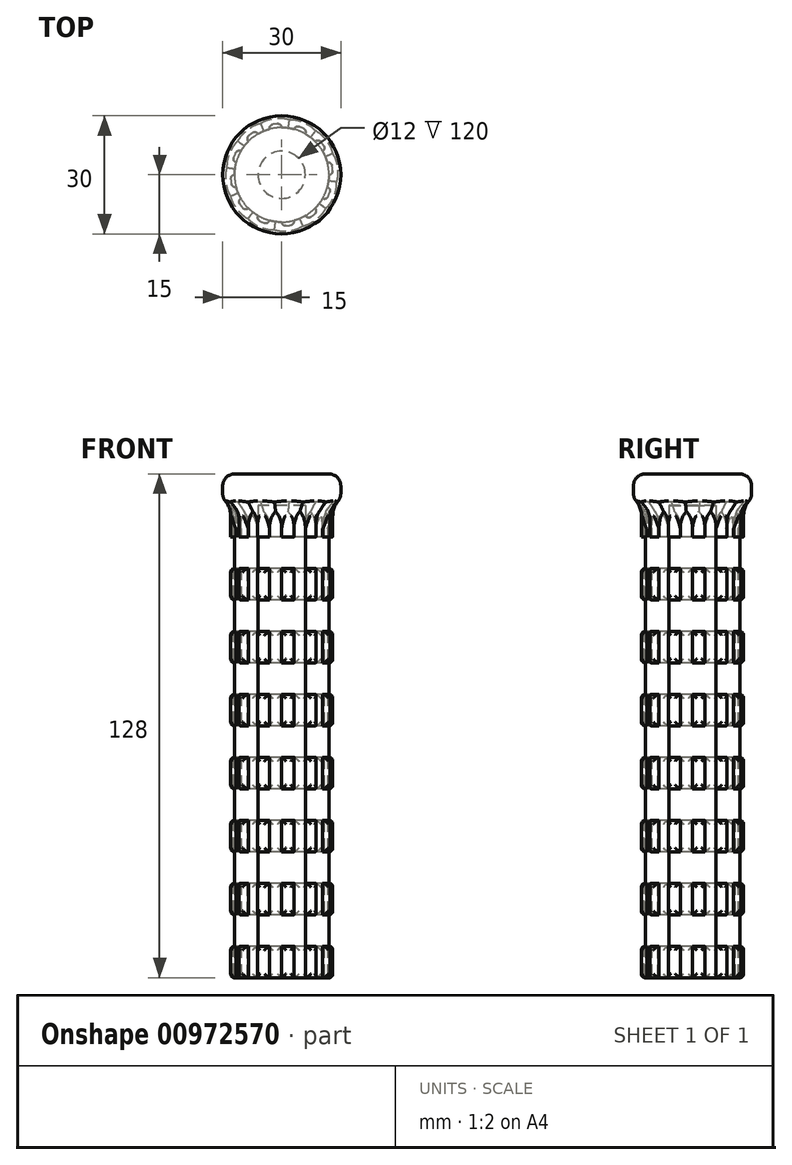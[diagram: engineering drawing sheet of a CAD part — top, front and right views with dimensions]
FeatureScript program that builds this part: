
annotation { "Feature Type Name" : "Feature", "Feature Type Description" : "" }
export const myFeature = defineFeature(function(context is Context, id is Id, definition is map)
    precondition{}
    {
        {
            var Q0;
            Q0=qCreatedBy(makeId("Top.planeOp"),FACE);
            var sketch = newSketch(context, id + "F0", { "sketchPlane" : qUnion([Q0])});
            skCircle(sketch, "E0", {"center": v(0, 0) * mm, "radius": 6 * mm});
            skCircle(sketch, "E1", {"center": v(0, 0) * mm, "radius": 12 * mm});
            skCircle(sketch, "E2", {"center": v(0, 0) * mm, "radius": 13 * mm});
            skLineSegment(sketch, "E3", {"start": v(0, 12) * mm, "end": v(0, 13) * mm});
            skLineSegment(sketch, "E4", {"start": v(-12, 0) * mm, "end": v(-13, 0) * mm, "construction": true});
            skLineSegment(sketch, "E5", {"start": v(-11.6, 3.1) * mm, "end": v(-12.56, 3.36) * mm});
            skLineSegment(sketch, "E6", {"start": v(-10.4, 6) * mm, "end": v(-11.26, 6.5) * mm});
            skLineSegment(sketch, "E7", {"start": v(-8.49, 8.49) * mm, "end": v(-9.2, 9.2) * mm});
            skLineSegment(sketch, "E8", {"start": v(-6, 10.4) * mm, "end": v(-6.5, 11.26) * mm});
            skLineSegment(sketch, "E9", {"start": v(-3.1, 11.6) * mm, "end": v(-3.36, 12.56) * mm});
            skLineSegment(sketch, "E10", {"start": v(-12, 0) * mm, "end": v(-13, 0) * mm});
            skLineSegment(sketch, "E11.MirrorCS", {"start": v(3.1, 11.6) * mm, "end": v(3.36, 12.56) * mm});
            skLineSegment(sketch, "E12.MirrorCS", {"start": v(6, 10.4) * mm, "end": v(6.5, 11.26) * mm});
            skLineSegment(sketch, "E13.MirrorCS", {"start": v(8.49, 8.49) * mm, "end": v(9.2, 9.2) * mm});
            skLineSegment(sketch, "E14.MirrorCS", {"start": v(10.4, 6) * mm, "end": v(11.26, 6.5) * mm});
            skLineSegment(sketch, "E15.MirrorCS", {"start": v(11.6, 3.1) * mm, "end": v(12.56, 3.36) * mm});
            skLineSegment(sketch, "E16.MirrorCS", {"start": v(12, 0) * mm, "end": v(13, 0) * mm, "construction": true});
            skLineSegment(sketch, "E17.MirrorCS", {"start": v(11.6, -3.1) * mm, "end": v(12.56, -3.36) * mm});
            skLineSegment(sketch, "E18.MirrorCS", {"start": v(10.4, -6) * mm, "end": v(11.26, -6.5) * mm});
            skLineSegment(sketch, "E19.MirrorCS", {"start": v(8.49, -8.49) * mm, "end": v(9.2, -9.2) * mm});
            skLineSegment(sketch, "E20.MirrorCS", {"start": v(6, -10.4) * mm, "end": v(6.5, -11.26) * mm});
            skLineSegment(sketch, "E21.MirrorCS", {"start": v(3.1, -11.6) * mm, "end": v(3.36, -12.56) * mm});
            skLineSegment(sketch, "E22.MirrorCS", {"start": v(0, -12) * mm, "end": v(0, -13) * mm});
            skLineSegment(sketch, "E23.MirrorCS", {"start": v(-3.1, -11.6) * mm, "end": v(-3.36, -12.56) * mm});
            skLineSegment(sketch, "E24.MirrorCS", {"start": v(-6, -10.4) * mm, "end": v(-6.5, -11.26) * mm});
            skLineSegment(sketch, "E25.MirrorCS", {"start": v(-8.49, -8.49) * mm, "end": v(-9.2, -9.2) * mm});
            skLineSegment(sketch, "E26.MirrorCS", {"start": v(-10.4, -6) * mm, "end": v(-11.26, -6.5) * mm});
            skLineSegment(sketch, "E27.MirrorCS", {"start": v(-11.6, -3.1) * mm, "end": v(-12.56, -3.36) * mm});
            skLineSegment(sketch, "E28", {"start": v(12, 0) * mm, "end": v(13, 0) * mm});
            skSolve(sketch);
        }
        {
            var Q0;
            Q0=makeQuery(id+"F0.imprint","IMPRINT",FACE,{"disambiguationData":[TD([[makeQuery(id+"F0.imprint","IMPRINT",EDGE,{"derivedFrom":sQuery(id+"F0.wireOp",EDGE,"E0")}),-1.0]])]});
            var Q1;
            {var subQ0=sQuery(id+"F0.wireOp",EDGE,"E3");Q1=makeQuery(id+"F0.imprint","IMPRINT",FACE,{"disambiguationData":[TD([[makeQuery(id+"F0.imprint","IMPRINT",EDGE,{"derivedFrom":subQ0}),1.0]])]});}
            var Q2;
            {var subQ0=sQuery(id+"F0.wireOp",EDGE,"E11.MirrorCS");Q2=makeQuery(id+"F0.imprint","IMPRINT",FACE,{"disambiguationData":[TD([[makeQuery(id+"F0.imprint","IMPRINT",EDGE,{"derivedFrom":subQ0}),-1.0]])]});}
            var Q3;
            {var subQ0=sQuery(id+"F0.wireOp",EDGE,"E13.MirrorCS");Q3=makeQuery(id+"F0.imprint","IMPRINT",FACE,{"disambiguationData":[TD([[makeQuery(id+"F0.imprint","IMPRINT",EDGE,{"derivedFrom":subQ0}),-1.0]])]});}
            var Q4;
            {var subQ0=sQuery(id+"F0.wireOp",EDGE,"E15.MirrorCS");Q4=makeQuery(id+"F0.imprint","IMPRINT",FACE,{"disambiguationData":[TD([[makeQuery(id+"F0.imprint","IMPRINT",EDGE,{"derivedFrom":subQ0}),-1.0]])]});}
            var Q5;
            {var subQ0=sQuery(id+"F0.wireOp",EDGE,"E17.MirrorCS");Q5=makeQuery(id+"F0.imprint","IMPRINT",FACE,{"disambiguationData":[TD([[makeQuery(id+"F0.imprint","IMPRINT",EDGE,{"derivedFrom":subQ0}),-1.0]])]});}
            var Q6;
            {var subQ0=sQuery(id+"F0.wireOp",EDGE,"E19.MirrorCS");Q6=makeQuery(id+"F0.imprint","IMPRINT",FACE,{"disambiguationData":[TD([[makeQuery(id+"F0.imprint","IMPRINT",EDGE,{"derivedFrom":subQ0}),-1.0]])]});}
            var Q7;
            {var subQ0=sQuery(id+"F0.wireOp",EDGE,"E21.MirrorCS");Q7=makeQuery(id+"F0.imprint","IMPRINT",FACE,{"disambiguationData":[TD([[makeQuery(id+"F0.imprint","IMPRINT",EDGE,{"derivedFrom":subQ0}),-1.0]])]});}
            var Q8;
            {var subQ0=sQuery(id+"F0.wireOp",EDGE,"E23.MirrorCS");Q8=makeQuery(id+"F0.imprint","IMPRINT",FACE,{"disambiguationData":[TD([[makeQuery(id+"F0.imprint","IMPRINT",EDGE,{"derivedFrom":subQ0}),-1.0]])]});}
            var Q9;
            {var subQ0=sQuery(id+"F0.wireOp",EDGE,"E25.MirrorCS");Q9=makeQuery(id+"F0.imprint","IMPRINT",FACE,{"disambiguationData":[TD([[makeQuery(id+"F0.imprint","IMPRINT",EDGE,{"derivedFrom":subQ0}),-1.0]])]});}
            var Q10;
            {var subQ0=sQuery(id+"F0.wireOp",EDGE,"E10");Q10=makeQuery(id+"F0.imprint","IMPRINT",FACE,{"disambiguationData":[TD([[makeQuery(id+"F0.imprint","IMPRINT",EDGE,{"derivedFrom":subQ0}),1.0]])]});}
            var Q11;
            {var subQ0=sQuery(id+"F0.wireOp",EDGE,"E5");Q11=makeQuery(id+"F0.imprint","IMPRINT",FACE,{"disambiguationData":[TD([[makeQuery(id+"F0.imprint","IMPRINT",EDGE,{"derivedFrom":subQ0}),-1.0]])]});}
            var Q12;
            {var subQ0=sQuery(id+"F0.wireOp",EDGE,"E7");Q12=makeQuery(id+"F0.imprint","IMPRINT",FACE,{"disambiguationData":[TD([[makeQuery(id+"F0.imprint","IMPRINT",EDGE,{"derivedFrom":subQ0}),-1.0]])]});}
            extrude(context, id + "F1", {"entities" : qUnion([Q0, Q1, Q2, Q3, Q4, Q5, Q6, Q7, Q8, Q9, Q10, Q11, Q12]), "depth" : 120 * mm, "offsetDistance" : 25 * mm});
        }
        {
            var Q0;
            Q0=makeQuery(id+"F1.opExtrude","CAP_FACE",FACE,{"disambiguationData":[OSD([sQuery(id+"F0.wireOp",EDGE,"E0"),sQuery(id+"F0.wireOp",EDGE,"E1"),sQuery(id+"F0.wireOp",EDGE,"E2"),sQuery(id+"F0.wireOp",EDGE,"E3"),sQuery(id+"F0.wireOp",EDGE,"E5"),sQuery(id+"F0.wireOp",EDGE,"E6"),sQuery(id+"F0.wireOp",EDGE,"E7"),sQuery(id+"F0.wireOp",EDGE,"E8"),sQuery(id+"F0.wireOp",EDGE,"E9"),sQuery(id+"F0.wireOp",EDGE,"E10"),sQuery(id+"F0.wireOp",EDGE,"E11.MirrorCS"),sQuery(id+"F0.wireOp",EDGE,"E12.MirrorCS"),sQuery(id+"F0.wireOp",EDGE,"E13.MirrorCS"),sQuery(id+"F0.wireOp",EDGE,"E14.MirrorCS"),sQuery(id+"F0.wireOp",EDGE,"E15.MirrorCS"),sQuery(id+"F0.wireOp",EDGE,"E17.MirrorCS"),sQuery(id+"F0.wireOp",EDGE,"E18.MirrorCS"),sQuery(id+"F0.wireOp",EDGE,"E19.MirrorCS"),sQuery(id+"F0.wireOp",EDGE,"E20.MirrorCS"),sQuery(id+"F0.wireOp",EDGE,"E21.MirrorCS"),sQuery(id+"F0.wireOp",EDGE,"E22.MirrorCS"),sQuery(id+"F0.wireOp",EDGE,"E23.MirrorCS"),sQuery(id+"F0.wireOp",EDGE,"E24.MirrorCS"),sQuery(id+"F0.wireOp",EDGE,"E25.MirrorCS"),sQuery(id+"F0.wireOp",EDGE,"E26.MirrorCS"),sQuery(id+"F0.wireOp",EDGE,"E27.MirrorCS"),sQuery(id+"F0.wireOp",EDGE,"E28")])],"isStart":false});
            var sketch = newSketch(context, id + "F2", { "sketchPlane" : qUnion([Q0])});
            skCircle(sketch, "E29", {"center": v(0, 0) * mm, "radius": 15 * mm});
            skSolve(sketch);
        }
        {
            var Q0;
            Q0 = qSketchRegion(id + "F2", true);
            extrude(context, id + "F3", {"entities" : qUnion([Q0]), "operationType" : NewBodyOperationType.ADD, "depth" : 8 * mm, "offsetDistance" : 25 * mm});
        }
        {
            var Q0;
            Q0=makeQuery(id+"F1.opExtrude","SWEPT_FACE",FACE,{"disambiguationData":[OSD([sQuery(id+"F0.wireOp",EDGE,"E27.MirrorCS")])]});
            var sketch = newSketch(context, id + "F4", { "sketchPlane" : qUnion([Q0])});
            skLineSegment(sketch, "E30", {"start": v(-12, 8) * mm, "end": v(-13, 8) * mm});
            skLineSegment(sketch, "E31", {"start": v(-13, 16) * mm, "end": v(-12, 16) * mm});
            skLineSegment(sketch, "E32.MirrorCS", {"start": v(-12, 24) * mm, "end": v(-13, 24) * mm});
            skLineSegment(sketch, "E33.MirrorCS", {"start": v(-13, 32) * mm, "end": v(-12, 32) * mm});
            skLineSegment(sketch, "E34.MirrorCS", {"start": v(-12, 40) * mm, "end": v(-13, 40) * mm});
            skLineSegment(sketch, "E35.MirrorCS", {"start": v(-13, 48) * mm, "end": v(-12, 48) * mm});
            skLineSegment(sketch, "E36.MirrorCS", {"start": v(-12, 56) * mm, "end": v(-13, 56) * mm});
            skLineSegment(sketch, "E37.MirrorCS", {"start": v(-13, 64) * mm, "end": v(-12, 64) * mm});
            skLineSegment(sketch, "E38.MirrorCS", {"start": v(-12, 72) * mm, "end": v(-13, 72) * mm});
            skLineSegment(sketch, "E39.MirrorCS", {"start": v(-13, 80) * mm, "end": v(-12, 80) * mm});
            skLineSegment(sketch, "E40.MirrorCS", {"start": v(-12, 88) * mm, "end": v(-13, 88) * mm});
            skLineSegment(sketch, "E41.MirrorCS", {"start": v(-13, 96) * mm, "end": v(-12, 96) * mm});
            skLineSegment(sketch, "E42.MirrorCS", {"start": v(-12, 104) * mm, "end": v(-13, 104) * mm});
            skLineSegment(sketch, "E43.MirrorCS", {"start": v(-13, 112) * mm, "end": v(-12, 112) * mm});
            skSolve(sketch);
        }
        {
            var Q0;
            {var subQ0=sQuery(id+"F4.wireOp",EDGE,"E30");Q0=makeQuery(id+"F4.imprint","IMPRINT",FACE,{"disambiguationData":[TD([[makeQuery(id+"F4.imprint","IMPRINT",EDGE,{"derivedFrom":subQ0}),-1.0]])]});}
            var Q1;
            {var subQ0=sQuery(id+"F4.wireOp",EDGE,"E32.MirrorCS");Q1=makeQuery(id+"F4.imprint","IMPRINT",FACE,{"disambiguationData":[TD([[makeQuery(id+"F4.imprint","IMPRINT",EDGE,{"derivedFrom":subQ0}),-1.0]])]});}
            var Q2;
            {var subQ0=sQuery(id+"F4.wireOp",EDGE,"E34.MirrorCS");Q2=makeQuery(id+"F4.imprint","IMPRINT",FACE,{"disambiguationData":[TD([[makeQuery(id+"F4.imprint","IMPRINT",EDGE,{"derivedFrom":subQ0}),-1.0]])]});}
            var Q3;
            {var subQ0=sQuery(id+"F4.wireOp",EDGE,"E36.MirrorCS");Q3=makeQuery(id+"F4.imprint","IMPRINT",FACE,{"disambiguationData":[TD([[makeQuery(id+"F4.imprint","IMPRINT",EDGE,{"derivedFrom":subQ0}),-1.0]])]});}
            var Q4;
            {var subQ0=sQuery(id+"F4.wireOp",EDGE,"E38.MirrorCS");Q4=makeQuery(id+"F4.imprint","IMPRINT",FACE,{"disambiguationData":[TD([[makeQuery(id+"F4.imprint","IMPRINT",EDGE,{"derivedFrom":subQ0}),-1.0]])]});}
            var Q5;
            {var subQ0=sQuery(id+"F4.wireOp",EDGE,"E40.MirrorCS");Q5=makeQuery(id+"F4.imprint","IMPRINT",FACE,{"disambiguationData":[TD([[makeQuery(id+"F4.imprint","IMPRINT",EDGE,{"derivedFrom":subQ0}),-1.0]])]});}
            var Q6;
            {var subQ0=sQuery(id+"F4.wireOp",EDGE,"E42.MirrorCS");Q6=makeQuery(id+"F4.imprint","IMPRINT",FACE,{"disambiguationData":[TD([[makeQuery(id+"F4.imprint","IMPRINT",EDGE,{"derivedFrom":subQ0}),-1.0]])]});}
            var Q7;
            Q7=makeQuery(id+"F1.opExtrude","CAP_EDGE",EDGE,{"disambiguationData":[OSD([sQuery(id+"F0.wireOp",EDGE,"E0")])],"isStart":true});
            sweep(context, id + "F5", {"operationType" : NewBodyOperationType.REMOVE, "profiles" : qUnion([Q0, Q1, Q2, Q3, Q4, Q5, Q6]), "path" : qUnion([Q7])});
        }
        {
            var Q0;
            {var subQ1=sQuery(id+"F0.wireOp",EDGE,"E15.MirrorCS");var subQ2=sQuery(id+"F0.wireOp",EDGE,"E2");var subQ3=sQuery(id+"F0.wireOp",EDGE,"E0");Q0=makeQuery(id+"F5.boolean.opBoolean","SPLIT",FACE,{"disambiguationData":[TD([makeQuery(id+"F5.opSweep","SWEPT_FACE",FACE,{"disambiguationData":[OSD([subQ3,sQuery(id+"F4.wireOp",EDGE,"E30")])]})])],"derivedFrom":makeQuery(id+"F1.opExtrude","SWEPT_FACE",FACE,{"disambiguationData":[OSD([subQ2]),TDD([makeQuery(id+"F0.imprint","IMPRINT",EDGE,{"disambiguationData":[TD([[makeQuery(id+"F0.imprint","INTERSECT",VERTEX,{"derivedFrom":[subQ2,subQ1]}),1.0]])],"derivedFrom":subQ2})])]})});}
            var Q1;
            {var subQ0=sQuery(id+"F0.wireOp",EDGE,"E15.MirrorCS");var subQ2=sQuery(id+"F0.wireOp",EDGE,"E0");var subQ3=sQuery(id+"F0.wireOp",EDGE,"E2");Q1=makeQuery(id+"F5.boolean.opBoolean","SPLIT",FACE,{"disambiguationData":[TD([makeQuery(id+"F5.opSweep","SWEPT_FACE",FACE,{"disambiguationData":[OSD([subQ2,sQuery(id+"F4.wireOp",EDGE,"E31")])]})])],"derivedFrom":makeQuery(id+"F1.opExtrude","SWEPT_FACE",FACE,{"disambiguationData":[OSD([subQ3]),TDD([makeQuery(id+"F0.imprint","IMPRINT",EDGE,{"disambiguationData":[TD([[makeQuery(id+"F0.imprint","INTERSECT",VERTEX,{"derivedFrom":[subQ3,subQ0]}),1.0]])],"derivedFrom":subQ3})])]})});}
            var Q2;
            {var subQ0=sQuery(id+"F0.wireOp",EDGE,"E15.MirrorCS");var subQ2=sQuery(id+"F0.wireOp",EDGE,"E0");var subQ3=sQuery(id+"F0.wireOp",EDGE,"E2");Q2=makeQuery(id+"F5.boolean.opBoolean","SPLIT",FACE,{"disambiguationData":[TD([makeQuery(id+"F5.opSweep","SWEPT_FACE",FACE,{"disambiguationData":[OSD([subQ2,sQuery(id+"F4.wireOp",EDGE,"E33.MirrorCS")])]})])],"derivedFrom":makeQuery(id+"F1.opExtrude","SWEPT_FACE",FACE,{"disambiguationData":[OSD([subQ3]),TDD([makeQuery(id+"F0.imprint","IMPRINT",EDGE,{"disambiguationData":[TD([[makeQuery(id+"F0.imprint","INTERSECT",VERTEX,{"derivedFrom":[subQ3,subQ0]}),1.0]])],"derivedFrom":subQ3})])]})});}
            var Q3;
            {var subQ0=sQuery(id+"F0.wireOp",EDGE,"E15.MirrorCS");var subQ1=sQuery(id+"F0.wireOp",EDGE,"E0");var subQ3=sQuery(id+"F0.wireOp",EDGE,"E2");Q3=makeQuery(id+"F5.boolean.opBoolean","SPLIT",FACE,{"disambiguationData":[TD([makeQuery(id+"F5.opSweep","SWEPT_FACE",FACE,{"disambiguationData":[OSD([subQ1,sQuery(id+"F4.wireOp",EDGE,"E35.MirrorCS")])]})])],"derivedFrom":makeQuery(id+"F1.opExtrude","SWEPT_FACE",FACE,{"disambiguationData":[OSD([subQ3]),TDD([makeQuery(id+"F0.imprint","IMPRINT",EDGE,{"disambiguationData":[TD([[makeQuery(id+"F0.imprint","INTERSECT",VERTEX,{"derivedFrom":[subQ3,subQ0]}),1.0]])],"derivedFrom":subQ3})])]})});}
            var Q4;
            {var subQ0=sQuery(id+"F0.wireOp",EDGE,"E15.MirrorCS");var subQ2=sQuery(id+"F0.wireOp",EDGE,"E0");var subQ3=sQuery(id+"F0.wireOp",EDGE,"E2");Q4=makeQuery(id+"F5.boolean.opBoolean","SPLIT",FACE,{"disambiguationData":[TD([makeQuery(id+"F5.opSweep","SWEPT_FACE",FACE,{"disambiguationData":[OSD([subQ2,sQuery(id+"F4.wireOp",EDGE,"E37.MirrorCS")])]})])],"derivedFrom":makeQuery(id+"F1.opExtrude","SWEPT_FACE",FACE,{"disambiguationData":[OSD([subQ3]),TDD([makeQuery(id+"F0.imprint","IMPRINT",EDGE,{"disambiguationData":[TD([[makeQuery(id+"F0.imprint","INTERSECT",VERTEX,{"derivedFrom":[subQ3,subQ0]}),1.0]])],"derivedFrom":subQ3})])]})});}
            var Q5;
            {var subQ0=sQuery(id+"F0.wireOp",EDGE,"E15.MirrorCS");var subQ1=sQuery(id+"F0.wireOp",EDGE,"E0");var subQ3=sQuery(id+"F0.wireOp",EDGE,"E2");Q5=makeQuery(id+"F5.boolean.opBoolean","SPLIT",FACE,{"disambiguationData":[TD([makeQuery(id+"F5.opSweep","SWEPT_FACE",FACE,{"disambiguationData":[OSD([subQ1,sQuery(id+"F4.wireOp",EDGE,"E39.MirrorCS")])]})])],"derivedFrom":makeQuery(id+"F1.opExtrude","SWEPT_FACE",FACE,{"disambiguationData":[OSD([subQ3]),TDD([makeQuery(id+"F0.imprint","IMPRINT",EDGE,{"disambiguationData":[TD([[makeQuery(id+"F0.imprint","INTERSECT",VERTEX,{"derivedFrom":[subQ3,subQ0]}),1.0]])],"derivedFrom":subQ3})])]})});}
            var Q6;
            {var subQ0=sQuery(id+"F0.wireOp",EDGE,"E15.MirrorCS");var subQ2=sQuery(id+"F0.wireOp",EDGE,"E0");var subQ3=sQuery(id+"F0.wireOp",EDGE,"E2");Q6=makeQuery(id+"F5.boolean.opBoolean","SPLIT",FACE,{"disambiguationData":[TD([makeQuery(id+"F5.opSweep","SWEPT_FACE",FACE,{"disambiguationData":[OSD([subQ2,sQuery(id+"F4.wireOp",EDGE,"E41.MirrorCS")])]})])],"derivedFrom":makeQuery(id+"F1.opExtrude","SWEPT_FACE",FACE,{"disambiguationData":[OSD([subQ3]),TDD([makeQuery(id+"F0.imprint","IMPRINT",EDGE,{"disambiguationData":[TD([[makeQuery(id+"F0.imprint","INTERSECT",VERTEX,{"derivedFrom":[subQ3,subQ0]}),1.0]])],"derivedFrom":subQ3})])]})});}
            var Q7;
            {var subQ0=sQuery(id+"F0.wireOp",EDGE,"E13.MirrorCS");var subQ2=sQuery(id+"F0.wireOp",EDGE,"E0");var subQ3=sQuery(id+"F0.wireOp",EDGE,"E2");Q7=makeQuery(id+"F5.boolean.opBoolean","SPLIT",FACE,{"disambiguationData":[TD([makeQuery(id+"F5.opSweep","SWEPT_FACE",FACE,{"disambiguationData":[OSD([subQ2,sQuery(id+"F4.wireOp",EDGE,"E41.MirrorCS")])]})])],"derivedFrom":makeQuery(id+"F1.opExtrude","SWEPT_FACE",FACE,{"disambiguationData":[OSD([subQ3]),TDD([makeQuery(id+"F0.imprint","IMPRINT",EDGE,{"disambiguationData":[TD([[makeQuery(id+"F0.imprint","INTERSECT",VERTEX,{"derivedFrom":[subQ3,subQ0]}),1.0]])],"derivedFrom":subQ3})])]})});}
            var Q8;
            {var subQ0=sQuery(id+"F0.wireOp",EDGE,"E13.MirrorCS");var subQ2=sQuery(id+"F0.wireOp",EDGE,"E0");var subQ3=sQuery(id+"F0.wireOp",EDGE,"E2");Q8=makeQuery(id+"F5.boolean.opBoolean","SPLIT",FACE,{"disambiguationData":[TD([makeQuery(id+"F5.opSweep","SWEPT_FACE",FACE,{"disambiguationData":[OSD([subQ2,sQuery(id+"F4.wireOp",EDGE,"E39.MirrorCS")])]})])],"derivedFrom":makeQuery(id+"F1.opExtrude","SWEPT_FACE",FACE,{"disambiguationData":[OSD([subQ3]),TDD([makeQuery(id+"F0.imprint","IMPRINT",EDGE,{"disambiguationData":[TD([[makeQuery(id+"F0.imprint","INTERSECT",VERTEX,{"derivedFrom":[subQ3,subQ0]}),1.0]])],"derivedFrom":subQ3})])]})});}
            var Q9;
            {var subQ0=sQuery(id+"F0.wireOp",EDGE,"E13.MirrorCS");var subQ1=sQuery(id+"F0.wireOp",EDGE,"E0");var subQ3=sQuery(id+"F0.wireOp",EDGE,"E2");Q9=makeQuery(id+"F5.boolean.opBoolean","SPLIT",FACE,{"disambiguationData":[TD([makeQuery(id+"F5.opSweep","SWEPT_FACE",FACE,{"disambiguationData":[OSD([subQ1,sQuery(id+"F4.wireOp",EDGE,"E37.MirrorCS")])]})])],"derivedFrom":makeQuery(id+"F1.opExtrude","SWEPT_FACE",FACE,{"disambiguationData":[OSD([subQ3]),TDD([makeQuery(id+"F0.imprint","IMPRINT",EDGE,{"disambiguationData":[TD([[makeQuery(id+"F0.imprint","INTERSECT",VERTEX,{"derivedFrom":[subQ3,subQ0]}),1.0]])],"derivedFrom":subQ3})])]})});}
            var Q10;
            {var subQ0=sQuery(id+"F0.wireOp",EDGE,"E13.MirrorCS");var subQ2=sQuery(id+"F0.wireOp",EDGE,"E0");var subQ3=sQuery(id+"F0.wireOp",EDGE,"E2");Q10=makeQuery(id+"F5.boolean.opBoolean","SPLIT",FACE,{"disambiguationData":[TD([makeQuery(id+"F5.opSweep","SWEPT_FACE",FACE,{"disambiguationData":[OSD([subQ2,sQuery(id+"F4.wireOp",EDGE,"E35.MirrorCS")])]})])],"derivedFrom":makeQuery(id+"F1.opExtrude","SWEPT_FACE",FACE,{"disambiguationData":[OSD([subQ3]),TDD([makeQuery(id+"F0.imprint","IMPRINT",EDGE,{"disambiguationData":[TD([[makeQuery(id+"F0.imprint","INTERSECT",VERTEX,{"derivedFrom":[subQ3,subQ0]}),1.0]])],"derivedFrom":subQ3})])]})});}
            var Q11;
            {var subQ0=sQuery(id+"F0.wireOp",EDGE,"E13.MirrorCS");var subQ1=sQuery(id+"F0.wireOp",EDGE,"E0");var subQ3=sQuery(id+"F0.wireOp",EDGE,"E2");Q11=makeQuery(id+"F5.boolean.opBoolean","SPLIT",FACE,{"disambiguationData":[TD([makeQuery(id+"F5.opSweep","SWEPT_FACE",FACE,{"disambiguationData":[OSD([subQ1,sQuery(id+"F4.wireOp",EDGE,"E33.MirrorCS")])]})])],"derivedFrom":makeQuery(id+"F1.opExtrude","SWEPT_FACE",FACE,{"disambiguationData":[OSD([subQ3]),TDD([makeQuery(id+"F0.imprint","IMPRINT",EDGE,{"disambiguationData":[TD([[makeQuery(id+"F0.imprint","INTERSECT",VERTEX,{"derivedFrom":[subQ3,subQ0]}),1.0]])],"derivedFrom":subQ3})])]})});}
            var Q12;
            {var subQ0=sQuery(id+"F0.wireOp",EDGE,"E13.MirrorCS");var subQ2=sQuery(id+"F0.wireOp",EDGE,"E0");var subQ3=sQuery(id+"F0.wireOp",EDGE,"E2");Q12=makeQuery(id+"F5.boolean.opBoolean","SPLIT",FACE,{"disambiguationData":[TD([makeQuery(id+"F5.opSweep","SWEPT_FACE",FACE,{"disambiguationData":[OSD([subQ2,sQuery(id+"F4.wireOp",EDGE,"E31")])]})])],"derivedFrom":makeQuery(id+"F1.opExtrude","SWEPT_FACE",FACE,{"disambiguationData":[OSD([subQ3]),TDD([makeQuery(id+"F0.imprint","IMPRINT",EDGE,{"disambiguationData":[TD([[makeQuery(id+"F0.imprint","INTERSECT",VERTEX,{"derivedFrom":[subQ3,subQ0]}),1.0]])],"derivedFrom":subQ3})])]})});}
            var Q13;
            {var subQ1=sQuery(id+"F0.wireOp",EDGE,"E13.MirrorCS");var subQ2=sQuery(id+"F0.wireOp",EDGE,"E2");var subQ3=sQuery(id+"F0.wireOp",EDGE,"E0");Q13=makeQuery(id+"F5.boolean.opBoolean","SPLIT",FACE,{"disambiguationData":[TD([makeQuery(id+"F5.opSweep","SWEPT_FACE",FACE,{"disambiguationData":[OSD([subQ3,sQuery(id+"F4.wireOp",EDGE,"E30")])]})])],"derivedFrom":makeQuery(id+"F1.opExtrude","SWEPT_FACE",FACE,{"disambiguationData":[OSD([subQ2]),TDD([makeQuery(id+"F0.imprint","IMPRINT",EDGE,{"disambiguationData":[TD([[makeQuery(id+"F0.imprint","INTERSECT",VERTEX,{"derivedFrom":[subQ2,subQ1]}),1.0]])],"derivedFrom":subQ2})])]})});}
            var Q14;
            {var subQ1=sQuery(id+"F0.wireOp",EDGE,"E11.MirrorCS");var subQ2=sQuery(id+"F0.wireOp",EDGE,"E2");var subQ3=sQuery(id+"F0.wireOp",EDGE,"E0");Q14=makeQuery(id+"F5.boolean.opBoolean","SPLIT",FACE,{"disambiguationData":[TD([makeQuery(id+"F5.opSweep","SWEPT_FACE",FACE,{"disambiguationData":[OSD([subQ3,sQuery(id+"F4.wireOp",EDGE,"E30")])]})])],"derivedFrom":makeQuery(id+"F1.opExtrude","SWEPT_FACE",FACE,{"disambiguationData":[OSD([subQ2]),TDD([makeQuery(id+"F0.imprint","IMPRINT",EDGE,{"disambiguationData":[TD([[makeQuery(id+"F0.imprint","INTERSECT",VERTEX,{"derivedFrom":[subQ2,subQ1]}),1.0]])],"derivedFrom":subQ2})])]})});}
            var Q15;
            {var subQ0=sQuery(id+"F0.wireOp",EDGE,"E11.MirrorCS");var subQ1=sQuery(id+"F0.wireOp",EDGE,"E0");var subQ3=sQuery(id+"F0.wireOp",EDGE,"E2");Q15=makeQuery(id+"F5.boolean.opBoolean","SPLIT",FACE,{"disambiguationData":[TD([makeQuery(id+"F5.opSweep","SWEPT_FACE",FACE,{"disambiguationData":[OSD([subQ1,sQuery(id+"F4.wireOp",EDGE,"E31")])]})])],"derivedFrom":makeQuery(id+"F1.opExtrude","SWEPT_FACE",FACE,{"disambiguationData":[OSD([subQ3]),TDD([makeQuery(id+"F0.imprint","IMPRINT",EDGE,{"disambiguationData":[TD([[makeQuery(id+"F0.imprint","INTERSECT",VERTEX,{"derivedFrom":[subQ3,subQ0]}),1.0]])],"derivedFrom":subQ3})])]})});}
            var Q16;
            {var subQ0=sQuery(id+"F0.wireOp",EDGE,"E11.MirrorCS");var subQ2=sQuery(id+"F0.wireOp",EDGE,"E0");var subQ3=sQuery(id+"F0.wireOp",EDGE,"E2");Q16=makeQuery(id+"F5.boolean.opBoolean","SPLIT",FACE,{"disambiguationData":[TD([makeQuery(id+"F5.opSweep","SWEPT_FACE",FACE,{"disambiguationData":[OSD([subQ2,sQuery(id+"F4.wireOp",EDGE,"E33.MirrorCS")])]})])],"derivedFrom":makeQuery(id+"F1.opExtrude","SWEPT_FACE",FACE,{"disambiguationData":[OSD([subQ3]),TDD([makeQuery(id+"F0.imprint","IMPRINT",EDGE,{"disambiguationData":[TD([[makeQuery(id+"F0.imprint","INTERSECT",VERTEX,{"derivedFrom":[subQ3,subQ0]}),1.0]])],"derivedFrom":subQ3})])]})});}
            var Q17;
            {var subQ0=sQuery(id+"F0.wireOp",EDGE,"E11.MirrorCS");var subQ1=sQuery(id+"F0.wireOp",EDGE,"E0");var subQ3=sQuery(id+"F0.wireOp",EDGE,"E2");Q17=makeQuery(id+"F5.boolean.opBoolean","SPLIT",FACE,{"disambiguationData":[TD([makeQuery(id+"F5.opSweep","SWEPT_FACE",FACE,{"disambiguationData":[OSD([subQ1,sQuery(id+"F4.wireOp",EDGE,"E35.MirrorCS")])]})])],"derivedFrom":makeQuery(id+"F1.opExtrude","SWEPT_FACE",FACE,{"disambiguationData":[OSD([subQ3]),TDD([makeQuery(id+"F0.imprint","IMPRINT",EDGE,{"disambiguationData":[TD([[makeQuery(id+"F0.imprint","INTERSECT",VERTEX,{"derivedFrom":[subQ3,subQ0]}),1.0]])],"derivedFrom":subQ3})])]})});}
            var Q18;
            {var subQ0=sQuery(id+"F0.wireOp",EDGE,"E11.MirrorCS");var subQ2=sQuery(id+"F0.wireOp",EDGE,"E0");var subQ3=sQuery(id+"F0.wireOp",EDGE,"E2");Q18=makeQuery(id+"F5.boolean.opBoolean","SPLIT",FACE,{"disambiguationData":[TD([makeQuery(id+"F5.opSweep","SWEPT_FACE",FACE,{"disambiguationData":[OSD([subQ2,sQuery(id+"F4.wireOp",EDGE,"E37.MirrorCS")])]})])],"derivedFrom":makeQuery(id+"F1.opExtrude","SWEPT_FACE",FACE,{"disambiguationData":[OSD([subQ3]),TDD([makeQuery(id+"F0.imprint","IMPRINT",EDGE,{"disambiguationData":[TD([[makeQuery(id+"F0.imprint","INTERSECT",VERTEX,{"derivedFrom":[subQ3,subQ0]}),1.0]])],"derivedFrom":subQ3})])]})});}
            var Q19;
            {var subQ0=sQuery(id+"F0.wireOp",EDGE,"E11.MirrorCS");var subQ2=sQuery(id+"F0.wireOp",EDGE,"E0");var subQ3=sQuery(id+"F0.wireOp",EDGE,"E2");Q19=makeQuery(id+"F5.boolean.opBoolean","SPLIT",FACE,{"disambiguationData":[TD([makeQuery(id+"F5.opSweep","SWEPT_FACE",FACE,{"disambiguationData":[OSD([subQ2,sQuery(id+"F4.wireOp",EDGE,"E39.MirrorCS")])]})])],"derivedFrom":makeQuery(id+"F1.opExtrude","SWEPT_FACE",FACE,{"disambiguationData":[OSD([subQ3]),TDD([makeQuery(id+"F0.imprint","IMPRINT",EDGE,{"disambiguationData":[TD([[makeQuery(id+"F0.imprint","INTERSECT",VERTEX,{"derivedFrom":[subQ3,subQ0]}),1.0]])],"derivedFrom":subQ3})])]})});}
            var Q20;
            {var subQ0=sQuery(id+"F0.wireOp",EDGE,"E11.MirrorCS");var subQ1=sQuery(id+"F0.wireOp",EDGE,"E0");var subQ3=sQuery(id+"F0.wireOp",EDGE,"E2");Q20=makeQuery(id+"F5.boolean.opBoolean","SPLIT",FACE,{"disambiguationData":[TD([makeQuery(id+"F5.opSweep","SWEPT_FACE",FACE,{"disambiguationData":[OSD([subQ1,sQuery(id+"F4.wireOp",EDGE,"E41.MirrorCS")])]})])],"derivedFrom":makeQuery(id+"F1.opExtrude","SWEPT_FACE",FACE,{"disambiguationData":[OSD([subQ3]),TDD([makeQuery(id+"F0.imprint","IMPRINT",EDGE,{"disambiguationData":[TD([[makeQuery(id+"F0.imprint","INTERSECT",VERTEX,{"derivedFrom":[subQ3,subQ0]}),1.0]])],"derivedFrom":subQ3})])]})});}
            var Q21;
            {var subQ0=sQuery(id+"F0.wireOp",EDGE,"E17.MirrorCS");var subQ1=sQuery(id+"F0.wireOp",EDGE,"E0");var subQ3=sQuery(id+"F0.wireOp",EDGE,"E2");Q21=makeQuery(id+"F5.boolean.opBoolean","SPLIT",FACE,{"disambiguationData":[TD([makeQuery(id+"F5.opSweep","SWEPT_FACE",FACE,{"disambiguationData":[OSD([subQ1,sQuery(id+"F4.wireOp",EDGE,"E41.MirrorCS")])]})])],"derivedFrom":makeQuery(id+"F1.opExtrude","SWEPT_FACE",FACE,{"disambiguationData":[OSD([subQ3]),TDD([makeQuery(id+"F0.imprint","IMPRINT",EDGE,{"disambiguationData":[TD([[makeQuery(id+"F0.imprint","INTERSECT",VERTEX,{"derivedFrom":[subQ3,subQ0]}),1.0]])],"derivedFrom":subQ3})])]})});}
            var Q22;
            {var subQ0=sQuery(id+"F0.wireOp",EDGE,"E17.MirrorCS");var subQ2=sQuery(id+"F0.wireOp",EDGE,"E0");var subQ3=sQuery(id+"F0.wireOp",EDGE,"E2");Q22=makeQuery(id+"F5.boolean.opBoolean","SPLIT",FACE,{"disambiguationData":[TD([makeQuery(id+"F5.opSweep","SWEPT_FACE",FACE,{"disambiguationData":[OSD([subQ2,sQuery(id+"F4.wireOp",EDGE,"E39.MirrorCS")])]})])],"derivedFrom":makeQuery(id+"F1.opExtrude","SWEPT_FACE",FACE,{"disambiguationData":[OSD([subQ3]),TDD([makeQuery(id+"F0.imprint","IMPRINT",EDGE,{"disambiguationData":[TD([[makeQuery(id+"F0.imprint","INTERSECT",VERTEX,{"derivedFrom":[subQ3,subQ0]}),1.0]])],"derivedFrom":subQ3})])]})});}
            var Q23;
            {var subQ0=sQuery(id+"F0.wireOp",EDGE,"E17.MirrorCS");var subQ2=sQuery(id+"F0.wireOp",EDGE,"E0");var subQ3=sQuery(id+"F0.wireOp",EDGE,"E2");Q23=makeQuery(id+"F5.boolean.opBoolean","SPLIT",FACE,{"disambiguationData":[TD([makeQuery(id+"F5.opSweep","SWEPT_FACE",FACE,{"disambiguationData":[OSD([subQ2,sQuery(id+"F4.wireOp",EDGE,"E37.MirrorCS")])]})])],"derivedFrom":makeQuery(id+"F1.opExtrude","SWEPT_FACE",FACE,{"disambiguationData":[OSD([subQ3]),TDD([makeQuery(id+"F0.imprint","IMPRINT",EDGE,{"disambiguationData":[TD([[makeQuery(id+"F0.imprint","INTERSECT",VERTEX,{"derivedFrom":[subQ3,subQ0]}),1.0]])],"derivedFrom":subQ3})])]})});}
            var Q24;
            {var subQ0=sQuery(id+"F0.wireOp",EDGE,"E17.MirrorCS");var subQ1=sQuery(id+"F0.wireOp",EDGE,"E0");var subQ3=sQuery(id+"F0.wireOp",EDGE,"E2");Q24=makeQuery(id+"F5.boolean.opBoolean","SPLIT",FACE,{"disambiguationData":[TD([makeQuery(id+"F5.opSweep","SWEPT_FACE",FACE,{"disambiguationData":[OSD([subQ1,sQuery(id+"F4.wireOp",EDGE,"E35.MirrorCS")])]})])],"derivedFrom":makeQuery(id+"F1.opExtrude","SWEPT_FACE",FACE,{"disambiguationData":[OSD([subQ3]),TDD([makeQuery(id+"F0.imprint","IMPRINT",EDGE,{"disambiguationData":[TD([[makeQuery(id+"F0.imprint","INTERSECT",VERTEX,{"derivedFrom":[subQ3,subQ0]}),1.0]])],"derivedFrom":subQ3})])]})});}
            var Q25;
            {var subQ0=sQuery(id+"F0.wireOp",EDGE,"E17.MirrorCS");var subQ2=sQuery(id+"F0.wireOp",EDGE,"E0");var subQ3=sQuery(id+"F0.wireOp",EDGE,"E2");Q25=makeQuery(id+"F5.boolean.opBoolean","SPLIT",FACE,{"disambiguationData":[TD([makeQuery(id+"F5.opSweep","SWEPT_FACE",FACE,{"disambiguationData":[OSD([subQ2,sQuery(id+"F4.wireOp",EDGE,"E33.MirrorCS")])]})])],"derivedFrom":makeQuery(id+"F1.opExtrude","SWEPT_FACE",FACE,{"disambiguationData":[OSD([subQ3]),TDD([makeQuery(id+"F0.imprint","IMPRINT",EDGE,{"disambiguationData":[TD([[makeQuery(id+"F0.imprint","INTERSECT",VERTEX,{"derivedFrom":[subQ3,subQ0]}),1.0]])],"derivedFrom":subQ3})])]})});}
            var Q26;
            {var subQ0=sQuery(id+"F0.wireOp",EDGE,"E17.MirrorCS");var subQ1=sQuery(id+"F0.wireOp",EDGE,"E0");var subQ3=sQuery(id+"F0.wireOp",EDGE,"E2");Q26=makeQuery(id+"F5.boolean.opBoolean","SPLIT",FACE,{"disambiguationData":[TD([makeQuery(id+"F5.opSweep","SWEPT_FACE",FACE,{"disambiguationData":[OSD([subQ1,sQuery(id+"F4.wireOp",EDGE,"E31")])]})])],"derivedFrom":makeQuery(id+"F1.opExtrude","SWEPT_FACE",FACE,{"disambiguationData":[OSD([subQ3]),TDD([makeQuery(id+"F0.imprint","IMPRINT",EDGE,{"disambiguationData":[TD([[makeQuery(id+"F0.imprint","INTERSECT",VERTEX,{"derivedFrom":[subQ3,subQ0]}),1.0]])],"derivedFrom":subQ3})])]})});}
            var Q27;
            {var subQ1=sQuery(id+"F0.wireOp",EDGE,"E17.MirrorCS");var subQ2=sQuery(id+"F0.wireOp",EDGE,"E2");var subQ3=sQuery(id+"F0.wireOp",EDGE,"E0");Q27=makeQuery(id+"F5.boolean.opBoolean","SPLIT",FACE,{"disambiguationData":[TD([makeQuery(id+"F5.opSweep","SWEPT_FACE",FACE,{"disambiguationData":[OSD([subQ3,sQuery(id+"F4.wireOp",EDGE,"E30")])]})])],"derivedFrom":makeQuery(id+"F1.opExtrude","SWEPT_FACE",FACE,{"disambiguationData":[OSD([subQ2]),TDD([makeQuery(id+"F0.imprint","IMPRINT",EDGE,{"disambiguationData":[TD([[makeQuery(id+"F0.imprint","INTERSECT",VERTEX,{"derivedFrom":[subQ2,subQ1]}),1.0]])],"derivedFrom":subQ2})])]})});}
            var Q28;
            {var subQ1=sQuery(id+"F0.wireOp",EDGE,"E19.MirrorCS");var subQ2=sQuery(id+"F0.wireOp",EDGE,"E2");var subQ3=sQuery(id+"F0.wireOp",EDGE,"E0");Q28=makeQuery(id+"F5.boolean.opBoolean","SPLIT",FACE,{"disambiguationData":[TD([makeQuery(id+"F5.opSweep","SWEPT_FACE",FACE,{"disambiguationData":[OSD([subQ3,sQuery(id+"F4.wireOp",EDGE,"E30")])]})])],"derivedFrom":makeQuery(id+"F1.opExtrude","SWEPT_FACE",FACE,{"disambiguationData":[OSD([subQ2]),TDD([makeQuery(id+"F0.imprint","IMPRINT",EDGE,{"disambiguationData":[TD([[makeQuery(id+"F0.imprint","INTERSECT",VERTEX,{"derivedFrom":[subQ2,subQ1]}),1.0]])],"derivedFrom":subQ2})])]})});}
            var Q29;
            {var subQ0=sQuery(id+"F0.wireOp",EDGE,"E19.MirrorCS");var subQ2=sQuery(id+"F0.wireOp",EDGE,"E0");var subQ3=sQuery(id+"F0.wireOp",EDGE,"E2");Q29=makeQuery(id+"F5.boolean.opBoolean","SPLIT",FACE,{"disambiguationData":[TD([makeQuery(id+"F5.opSweep","SWEPT_FACE",FACE,{"disambiguationData":[OSD([subQ2,sQuery(id+"F4.wireOp",EDGE,"E31")])]})])],"derivedFrom":makeQuery(id+"F1.opExtrude","SWEPT_FACE",FACE,{"disambiguationData":[OSD([subQ3]),TDD([makeQuery(id+"F0.imprint","IMPRINT",EDGE,{"disambiguationData":[TD([[makeQuery(id+"F0.imprint","INTERSECT",VERTEX,{"derivedFrom":[subQ3,subQ0]}),1.0]])],"derivedFrom":subQ3})])]})});}
            var Q30;
            {var subQ0=sQuery(id+"F0.wireOp",EDGE,"E19.MirrorCS");var subQ1=sQuery(id+"F0.wireOp",EDGE,"E0");var subQ3=sQuery(id+"F0.wireOp",EDGE,"E2");Q30=makeQuery(id+"F5.boolean.opBoolean","SPLIT",FACE,{"disambiguationData":[TD([makeQuery(id+"F5.opSweep","SWEPT_FACE",FACE,{"disambiguationData":[OSD([subQ1,sQuery(id+"F4.wireOp",EDGE,"E33.MirrorCS")])]})])],"derivedFrom":makeQuery(id+"F1.opExtrude","SWEPT_FACE",FACE,{"disambiguationData":[OSD([subQ3]),TDD([makeQuery(id+"F0.imprint","IMPRINT",EDGE,{"disambiguationData":[TD([[makeQuery(id+"F0.imprint","INTERSECT",VERTEX,{"derivedFrom":[subQ3,subQ0]}),1.0]])],"derivedFrom":subQ3})])]})});}
            var Q31;
            {var subQ0=sQuery(id+"F0.wireOp",EDGE,"E19.MirrorCS");var subQ2=sQuery(id+"F0.wireOp",EDGE,"E0");var subQ3=sQuery(id+"F0.wireOp",EDGE,"E2");Q31=makeQuery(id+"F5.boolean.opBoolean","SPLIT",FACE,{"disambiguationData":[TD([makeQuery(id+"F5.opSweep","SWEPT_FACE",FACE,{"disambiguationData":[OSD([subQ2,sQuery(id+"F4.wireOp",EDGE,"E35.MirrorCS")])]})])],"derivedFrom":makeQuery(id+"F1.opExtrude","SWEPT_FACE",FACE,{"disambiguationData":[OSD([subQ3]),TDD([makeQuery(id+"F0.imprint","IMPRINT",EDGE,{"disambiguationData":[TD([[makeQuery(id+"F0.imprint","INTERSECT",VERTEX,{"derivedFrom":[subQ3,subQ0]}),1.0]])],"derivedFrom":subQ3})])]})});}
            var Q32;
            {var subQ0=sQuery(id+"F0.wireOp",EDGE,"E19.MirrorCS");var subQ1=sQuery(id+"F0.wireOp",EDGE,"E0");var subQ3=sQuery(id+"F0.wireOp",EDGE,"E2");Q32=makeQuery(id+"F5.boolean.opBoolean","SPLIT",FACE,{"disambiguationData":[TD([makeQuery(id+"F5.opSweep","SWEPT_FACE",FACE,{"disambiguationData":[OSD([subQ1,sQuery(id+"F4.wireOp",EDGE,"E37.MirrorCS")])]})])],"derivedFrom":makeQuery(id+"F1.opExtrude","SWEPT_FACE",FACE,{"disambiguationData":[OSD([subQ3]),TDD([makeQuery(id+"F0.imprint","IMPRINT",EDGE,{"disambiguationData":[TD([[makeQuery(id+"F0.imprint","INTERSECT",VERTEX,{"derivedFrom":[subQ3,subQ0]}),1.0]])],"derivedFrom":subQ3})])]})});}
            var Q33;
            {var subQ0=sQuery(id+"F0.wireOp",EDGE,"E19.MirrorCS");var subQ2=sQuery(id+"F0.wireOp",EDGE,"E0");var subQ3=sQuery(id+"F0.wireOp",EDGE,"E2");Q33=makeQuery(id+"F5.boolean.opBoolean","SPLIT",FACE,{"disambiguationData":[TD([makeQuery(id+"F5.opSweep","SWEPT_FACE",FACE,{"disambiguationData":[OSD([subQ2,sQuery(id+"F4.wireOp",EDGE,"E39.MirrorCS")])]})])],"derivedFrom":makeQuery(id+"F1.opExtrude","SWEPT_FACE",FACE,{"disambiguationData":[OSD([subQ3]),TDD([makeQuery(id+"F0.imprint","IMPRINT",EDGE,{"disambiguationData":[TD([[makeQuery(id+"F0.imprint","INTERSECT",VERTEX,{"derivedFrom":[subQ3,subQ0]}),1.0]])],"derivedFrom":subQ3})])]})});}
            var Q34;
            {var subQ0=sQuery(id+"F0.wireOp",EDGE,"E19.MirrorCS");var subQ2=sQuery(id+"F0.wireOp",EDGE,"E0");var subQ3=sQuery(id+"F0.wireOp",EDGE,"E2");Q34=makeQuery(id+"F5.boolean.opBoolean","SPLIT",FACE,{"disambiguationData":[TD([makeQuery(id+"F5.opSweep","SWEPT_FACE",FACE,{"disambiguationData":[OSD([subQ2,sQuery(id+"F4.wireOp",EDGE,"E41.MirrorCS")])]})])],"derivedFrom":makeQuery(id+"F1.opExtrude","SWEPT_FACE",FACE,{"disambiguationData":[OSD([subQ3]),TDD([makeQuery(id+"F0.imprint","IMPRINT",EDGE,{"disambiguationData":[TD([[makeQuery(id+"F0.imprint","INTERSECT",VERTEX,{"derivedFrom":[subQ3,subQ0]}),1.0]])],"derivedFrom":subQ3})])]})});}
            var Q35;
            {var subQ0=sQuery(id+"F0.wireOp",EDGE,"E21.MirrorCS");var subQ2=sQuery(id+"F0.wireOp",EDGE,"E0");var subQ3=sQuery(id+"F0.wireOp",EDGE,"E2");Q35=makeQuery(id+"F5.boolean.opBoolean","SPLIT",FACE,{"disambiguationData":[TD([makeQuery(id+"F5.opSweep","SWEPT_FACE",FACE,{"disambiguationData":[OSD([subQ2,sQuery(id+"F4.wireOp",EDGE,"E41.MirrorCS")])]})])],"derivedFrom":makeQuery(id+"F1.opExtrude","SWEPT_FACE",FACE,{"disambiguationData":[OSD([subQ3]),TDD([makeQuery(id+"F0.imprint","IMPRINT",EDGE,{"disambiguationData":[TD([[makeQuery(id+"F0.imprint","INTERSECT",VERTEX,{"derivedFrom":[subQ3,subQ0]}),1.0]])],"derivedFrom":subQ3})])]})});}
            var Q36;
            {var subQ0=sQuery(id+"F0.wireOp",EDGE,"E21.MirrorCS");var subQ1=sQuery(id+"F0.wireOp",EDGE,"E0");var subQ3=sQuery(id+"F0.wireOp",EDGE,"E2");Q36=makeQuery(id+"F5.boolean.opBoolean","SPLIT",FACE,{"disambiguationData":[TD([makeQuery(id+"F5.opSweep","SWEPT_FACE",FACE,{"disambiguationData":[OSD([subQ1,sQuery(id+"F4.wireOp",EDGE,"E39.MirrorCS")])]})])],"derivedFrom":makeQuery(id+"F1.opExtrude","SWEPT_FACE",FACE,{"disambiguationData":[OSD([subQ3]),TDD([makeQuery(id+"F0.imprint","IMPRINT",EDGE,{"disambiguationData":[TD([[makeQuery(id+"F0.imprint","INTERSECT",VERTEX,{"derivedFrom":[subQ3,subQ0]}),1.0]])],"derivedFrom":subQ3})])]})});}
            var Q37;
            {var subQ0=sQuery(id+"F0.wireOp",EDGE,"E21.MirrorCS");var subQ2=sQuery(id+"F0.wireOp",EDGE,"E0");var subQ3=sQuery(id+"F0.wireOp",EDGE,"E2");Q37=makeQuery(id+"F5.boolean.opBoolean","SPLIT",FACE,{"disambiguationData":[TD([makeQuery(id+"F5.opSweep","SWEPT_FACE",FACE,{"disambiguationData":[OSD([subQ2,sQuery(id+"F4.wireOp",EDGE,"E37.MirrorCS")])]})])],"derivedFrom":makeQuery(id+"F1.opExtrude","SWEPT_FACE",FACE,{"disambiguationData":[OSD([subQ3]),TDD([makeQuery(id+"F0.imprint","IMPRINT",EDGE,{"disambiguationData":[TD([[makeQuery(id+"F0.imprint","INTERSECT",VERTEX,{"derivedFrom":[subQ3,subQ0]}),1.0]])],"derivedFrom":subQ3})])]})});}
            var Q38;
            {var subQ0=sQuery(id+"F0.wireOp",EDGE,"E21.MirrorCS");var subQ1=sQuery(id+"F0.wireOp",EDGE,"E0");var subQ3=sQuery(id+"F0.wireOp",EDGE,"E2");Q38=makeQuery(id+"F5.boolean.opBoolean","SPLIT",FACE,{"disambiguationData":[TD([makeQuery(id+"F5.opSweep","SWEPT_FACE",FACE,{"disambiguationData":[OSD([subQ1,sQuery(id+"F4.wireOp",EDGE,"E35.MirrorCS")])]})])],"derivedFrom":makeQuery(id+"F1.opExtrude","SWEPT_FACE",FACE,{"disambiguationData":[OSD([subQ3]),TDD([makeQuery(id+"F0.imprint","IMPRINT",EDGE,{"disambiguationData":[TD([[makeQuery(id+"F0.imprint","INTERSECT",VERTEX,{"derivedFrom":[subQ3,subQ0]}),1.0]])],"derivedFrom":subQ3})])]})});}
            var Q39;
            {var subQ0=sQuery(id+"F0.wireOp",EDGE,"E21.MirrorCS");var subQ2=sQuery(id+"F0.wireOp",EDGE,"E0");var subQ3=sQuery(id+"F0.wireOp",EDGE,"E2");Q39=makeQuery(id+"F5.boolean.opBoolean","SPLIT",FACE,{"disambiguationData":[TD([makeQuery(id+"F5.opSweep","SWEPT_FACE",FACE,{"disambiguationData":[OSD([subQ2,sQuery(id+"F4.wireOp",EDGE,"E33.MirrorCS")])]})])],"derivedFrom":makeQuery(id+"F1.opExtrude","SWEPT_FACE",FACE,{"disambiguationData":[OSD([subQ3]),TDD([makeQuery(id+"F0.imprint","IMPRINT",EDGE,{"disambiguationData":[TD([[makeQuery(id+"F0.imprint","INTERSECT",VERTEX,{"derivedFrom":[subQ3,subQ0]}),1.0]])],"derivedFrom":subQ3})])]})});}
            var Q40;
            {var subQ0=sQuery(id+"F0.wireOp",EDGE,"E21.MirrorCS");var subQ2=sQuery(id+"F0.wireOp",EDGE,"E0");var subQ3=sQuery(id+"F0.wireOp",EDGE,"E2");Q40=makeQuery(id+"F5.boolean.opBoolean","SPLIT",FACE,{"disambiguationData":[TD([makeQuery(id+"F5.opSweep","SWEPT_FACE",FACE,{"disambiguationData":[OSD([subQ2,sQuery(id+"F4.wireOp",EDGE,"E31")])]})])],"derivedFrom":makeQuery(id+"F1.opExtrude","SWEPT_FACE",FACE,{"disambiguationData":[OSD([subQ3]),TDD([makeQuery(id+"F0.imprint","IMPRINT",EDGE,{"disambiguationData":[TD([[makeQuery(id+"F0.imprint","INTERSECT",VERTEX,{"derivedFrom":[subQ3,subQ0]}),1.0]])],"derivedFrom":subQ3})])]})});}
            var Q41;
            {var subQ1=sQuery(id+"F0.wireOp",EDGE,"E21.MirrorCS");var subQ2=sQuery(id+"F0.wireOp",EDGE,"E2");var subQ3=sQuery(id+"F0.wireOp",EDGE,"E0");Q41=makeQuery(id+"F5.boolean.opBoolean","SPLIT",FACE,{"disambiguationData":[TD([makeQuery(id+"F5.opSweep","SWEPT_FACE",FACE,{"disambiguationData":[OSD([subQ3,sQuery(id+"F4.wireOp",EDGE,"E30")])]})])],"derivedFrom":makeQuery(id+"F1.opExtrude","SWEPT_FACE",FACE,{"disambiguationData":[OSD([subQ2]),TDD([makeQuery(id+"F0.imprint","IMPRINT",EDGE,{"disambiguationData":[TD([[makeQuery(id+"F0.imprint","INTERSECT",VERTEX,{"derivedFrom":[subQ2,subQ1]}),1.0]])],"derivedFrom":subQ2})])]})});}
            var Q42;
            {var subQ1=sQuery(id+"F0.wireOp",EDGE,"E23.MirrorCS");var subQ2=sQuery(id+"F0.wireOp",EDGE,"E2");var subQ3=sQuery(id+"F0.wireOp",EDGE,"E0");Q42=makeQuery(id+"F5.boolean.opBoolean","SPLIT",FACE,{"disambiguationData":[TD([makeQuery(id+"F5.opSweep","SWEPT_FACE",FACE,{"disambiguationData":[OSD([subQ3,sQuery(id+"F4.wireOp",EDGE,"E30")])]})])],"derivedFrom":makeQuery(id+"F1.opExtrude","SWEPT_FACE",FACE,{"disambiguationData":[OSD([subQ2]),TDD([makeQuery(id+"F0.imprint","IMPRINT",EDGE,{"disambiguationData":[TD([[makeQuery(id+"F0.imprint","INTERSECT",VERTEX,{"derivedFrom":[subQ2,subQ1]}),1.0]])],"derivedFrom":subQ2})])]})});}
            var Q43;
            {var subQ0=sQuery(id+"F0.wireOp",EDGE,"E23.MirrorCS");var subQ1=sQuery(id+"F0.wireOp",EDGE,"E0");var subQ3=sQuery(id+"F0.wireOp",EDGE,"E2");Q43=makeQuery(id+"F5.boolean.opBoolean","SPLIT",FACE,{"disambiguationData":[TD([makeQuery(id+"F5.opSweep","SWEPT_FACE",FACE,{"disambiguationData":[OSD([subQ1,sQuery(id+"F4.wireOp",EDGE,"E31")])]})])],"derivedFrom":makeQuery(id+"F1.opExtrude","SWEPT_FACE",FACE,{"disambiguationData":[OSD([subQ3]),TDD([makeQuery(id+"F0.imprint","IMPRINT",EDGE,{"disambiguationData":[TD([[makeQuery(id+"F0.imprint","INTERSECT",VERTEX,{"derivedFrom":[subQ3,subQ0]}),1.0]])],"derivedFrom":subQ3})])]})});}
            var Q44;
            {var subQ0=sQuery(id+"F0.wireOp",EDGE,"E23.MirrorCS");var subQ2=sQuery(id+"F0.wireOp",EDGE,"E0");var subQ3=sQuery(id+"F0.wireOp",EDGE,"E2");Q44=makeQuery(id+"F5.boolean.opBoolean","SPLIT",FACE,{"disambiguationData":[TD([makeQuery(id+"F5.opSweep","SWEPT_FACE",FACE,{"disambiguationData":[OSD([subQ2,sQuery(id+"F4.wireOp",EDGE,"E33.MirrorCS")])]})])],"derivedFrom":makeQuery(id+"F1.opExtrude","SWEPT_FACE",FACE,{"disambiguationData":[OSD([subQ3]),TDD([makeQuery(id+"F0.imprint","IMPRINT",EDGE,{"disambiguationData":[TD([[makeQuery(id+"F0.imprint","INTERSECT",VERTEX,{"derivedFrom":[subQ3,subQ0]}),1.0]])],"derivedFrom":subQ3})])]})});}
            var Q45;
            {var subQ0=sQuery(id+"F0.wireOp",EDGE,"E23.MirrorCS");var subQ2=sQuery(id+"F0.wireOp",EDGE,"E0");var subQ3=sQuery(id+"F0.wireOp",EDGE,"E2");Q45=makeQuery(id+"F5.boolean.opBoolean","SPLIT",FACE,{"disambiguationData":[TD([makeQuery(id+"F5.opSweep","SWEPT_FACE",FACE,{"disambiguationData":[OSD([subQ2,sQuery(id+"F4.wireOp",EDGE,"E35.MirrorCS")])]})])],"derivedFrom":makeQuery(id+"F1.opExtrude","SWEPT_FACE",FACE,{"disambiguationData":[OSD([subQ3]),TDD([makeQuery(id+"F0.imprint","IMPRINT",EDGE,{"disambiguationData":[TD([[makeQuery(id+"F0.imprint","INTERSECT",VERTEX,{"derivedFrom":[subQ3,subQ0]}),1.0]])],"derivedFrom":subQ3})])]})});}
            var Q46;
            {var subQ0=sQuery(id+"F0.wireOp",EDGE,"E23.MirrorCS");var subQ1=sQuery(id+"F0.wireOp",EDGE,"E0");var subQ3=sQuery(id+"F0.wireOp",EDGE,"E2");Q46=makeQuery(id+"F5.boolean.opBoolean","SPLIT",FACE,{"disambiguationData":[TD([makeQuery(id+"F5.opSweep","SWEPT_FACE",FACE,{"disambiguationData":[OSD([subQ1,sQuery(id+"F4.wireOp",EDGE,"E37.MirrorCS")])]})])],"derivedFrom":makeQuery(id+"F1.opExtrude","SWEPT_FACE",FACE,{"disambiguationData":[OSD([subQ3]),TDD([makeQuery(id+"F0.imprint","IMPRINT",EDGE,{"disambiguationData":[TD([[makeQuery(id+"F0.imprint","INTERSECT",VERTEX,{"derivedFrom":[subQ3,subQ0]}),1.0]])],"derivedFrom":subQ3})])]})});}
            var Q47;
            {var subQ0=sQuery(id+"F0.wireOp",EDGE,"E23.MirrorCS");var subQ2=sQuery(id+"F0.wireOp",EDGE,"E0");var subQ3=sQuery(id+"F0.wireOp",EDGE,"E2");Q47=makeQuery(id+"F5.boolean.opBoolean","SPLIT",FACE,{"disambiguationData":[TD([makeQuery(id+"F5.opSweep","SWEPT_FACE",FACE,{"disambiguationData":[OSD([subQ2,sQuery(id+"F4.wireOp",EDGE,"E39.MirrorCS")])]})])],"derivedFrom":makeQuery(id+"F1.opExtrude","SWEPT_FACE",FACE,{"disambiguationData":[OSD([subQ3]),TDD([makeQuery(id+"F0.imprint","IMPRINT",EDGE,{"disambiguationData":[TD([[makeQuery(id+"F0.imprint","INTERSECT",VERTEX,{"derivedFrom":[subQ3,subQ0]}),1.0]])],"derivedFrom":subQ3})])]})});}
            var Q48;
            {var subQ0=sQuery(id+"F0.wireOp",EDGE,"E23.MirrorCS");var subQ1=sQuery(id+"F0.wireOp",EDGE,"E0");var subQ3=sQuery(id+"F0.wireOp",EDGE,"E2");Q48=makeQuery(id+"F5.boolean.opBoolean","SPLIT",FACE,{"disambiguationData":[TD([makeQuery(id+"F5.opSweep","SWEPT_FACE",FACE,{"disambiguationData":[OSD([subQ1,sQuery(id+"F4.wireOp",EDGE,"E41.MirrorCS")])]})])],"derivedFrom":makeQuery(id+"F1.opExtrude","SWEPT_FACE",FACE,{"disambiguationData":[OSD([subQ3]),TDD([makeQuery(id+"F0.imprint","IMPRINT",EDGE,{"disambiguationData":[TD([[makeQuery(id+"F0.imprint","INTERSECT",VERTEX,{"derivedFrom":[subQ3,subQ0]}),1.0]])],"derivedFrom":subQ3})])]})});}
            var Q49;
            {var subQ0=sQuery(id+"F0.wireOp",EDGE,"E25.MirrorCS");var subQ2=sQuery(id+"F0.wireOp",EDGE,"E0");var subQ3=sQuery(id+"F0.wireOp",EDGE,"E2");Q49=makeQuery(id+"F5.boolean.opBoolean","SPLIT",FACE,{"disambiguationData":[TD([makeQuery(id+"F5.opSweep","SWEPT_FACE",FACE,{"disambiguationData":[OSD([subQ2,sQuery(id+"F4.wireOp",EDGE,"E41.MirrorCS")])]})])],"derivedFrom":makeQuery(id+"F1.opExtrude","SWEPT_FACE",FACE,{"disambiguationData":[OSD([subQ3]),TDD([makeQuery(id+"F0.imprint","IMPRINT",EDGE,{"disambiguationData":[TD([[makeQuery(id+"F0.imprint","INTERSECT",VERTEX,{"derivedFrom":[subQ3,subQ0]}),1.0]])],"derivedFrom":subQ3})])]})});}
            var Q50;
            {var subQ0=sQuery(id+"F0.wireOp",EDGE,"E25.MirrorCS");var subQ1=sQuery(id+"F0.wireOp",EDGE,"E0");var subQ3=sQuery(id+"F0.wireOp",EDGE,"E2");Q50=makeQuery(id+"F5.boolean.opBoolean","SPLIT",FACE,{"disambiguationData":[TD([makeQuery(id+"F5.opSweep","SWEPT_FACE",FACE,{"disambiguationData":[OSD([subQ1,sQuery(id+"F4.wireOp",EDGE,"E39.MirrorCS")])]})])],"derivedFrom":makeQuery(id+"F1.opExtrude","SWEPT_FACE",FACE,{"disambiguationData":[OSD([subQ3]),TDD([makeQuery(id+"F0.imprint","IMPRINT",EDGE,{"disambiguationData":[TD([[makeQuery(id+"F0.imprint","INTERSECT",VERTEX,{"derivedFrom":[subQ3,subQ0]}),1.0]])],"derivedFrom":subQ3})])]})});}
            var Q51;
            {var subQ0=sQuery(id+"F0.wireOp",EDGE,"E25.MirrorCS");var subQ2=sQuery(id+"F0.wireOp",EDGE,"E0");var subQ3=sQuery(id+"F0.wireOp",EDGE,"E2");Q51=makeQuery(id+"F5.boolean.opBoolean","SPLIT",FACE,{"disambiguationData":[TD([makeQuery(id+"F5.opSweep","SWEPT_FACE",FACE,{"disambiguationData":[OSD([subQ2,sQuery(id+"F4.wireOp",EDGE,"E37.MirrorCS")])]})])],"derivedFrom":makeQuery(id+"F1.opExtrude","SWEPT_FACE",FACE,{"disambiguationData":[OSD([subQ3]),TDD([makeQuery(id+"F0.imprint","IMPRINT",EDGE,{"disambiguationData":[TD([[makeQuery(id+"F0.imprint","INTERSECT",VERTEX,{"derivedFrom":[subQ3,subQ0]}),1.0]])],"derivedFrom":subQ3})])]})});}
            var Q52;
            {var subQ0=sQuery(id+"F0.wireOp",EDGE,"E25.MirrorCS");var subQ2=sQuery(id+"F0.wireOp",EDGE,"E0");var subQ3=sQuery(id+"F0.wireOp",EDGE,"E2");Q52=makeQuery(id+"F5.boolean.opBoolean","SPLIT",FACE,{"disambiguationData":[TD([makeQuery(id+"F5.opSweep","SWEPT_FACE",FACE,{"disambiguationData":[OSD([subQ2,sQuery(id+"F4.wireOp",EDGE,"E35.MirrorCS")])]})])],"derivedFrom":makeQuery(id+"F1.opExtrude","SWEPT_FACE",FACE,{"disambiguationData":[OSD([subQ3]),TDD([makeQuery(id+"F0.imprint","IMPRINT",EDGE,{"disambiguationData":[TD([[makeQuery(id+"F0.imprint","INTERSECT",VERTEX,{"derivedFrom":[subQ3,subQ0]}),1.0]])],"derivedFrom":subQ3})])]})});}
            var Q53;
            {var subQ0=sQuery(id+"F0.wireOp",EDGE,"E25.MirrorCS");var subQ1=sQuery(id+"F0.wireOp",EDGE,"E0");var subQ3=sQuery(id+"F0.wireOp",EDGE,"E2");Q53=makeQuery(id+"F5.boolean.opBoolean","SPLIT",FACE,{"disambiguationData":[TD([makeQuery(id+"F5.opSweep","SWEPT_FACE",FACE,{"disambiguationData":[OSD([subQ1,sQuery(id+"F4.wireOp",EDGE,"E33.MirrorCS")])]})])],"derivedFrom":makeQuery(id+"F1.opExtrude","SWEPT_FACE",FACE,{"disambiguationData":[OSD([subQ3]),TDD([makeQuery(id+"F0.imprint","IMPRINT",EDGE,{"disambiguationData":[TD([[makeQuery(id+"F0.imprint","INTERSECT",VERTEX,{"derivedFrom":[subQ3,subQ0]}),1.0]])],"derivedFrom":subQ3})])]})});}
            var Q54;
            {var subQ0=sQuery(id+"F0.wireOp",EDGE,"E25.MirrorCS");var subQ2=sQuery(id+"F0.wireOp",EDGE,"E0");var subQ3=sQuery(id+"F0.wireOp",EDGE,"E2");Q54=makeQuery(id+"F5.boolean.opBoolean","SPLIT",FACE,{"disambiguationData":[TD([makeQuery(id+"F5.opSweep","SWEPT_FACE",FACE,{"disambiguationData":[OSD([subQ2,sQuery(id+"F4.wireOp",EDGE,"E31")])]})])],"derivedFrom":makeQuery(id+"F1.opExtrude","SWEPT_FACE",FACE,{"disambiguationData":[OSD([subQ3]),TDD([makeQuery(id+"F0.imprint","IMPRINT",EDGE,{"disambiguationData":[TD([[makeQuery(id+"F0.imprint","INTERSECT",VERTEX,{"derivedFrom":[subQ3,subQ0]}),1.0]])],"derivedFrom":subQ3})])]})});}
            var Q55;
            {var subQ1=sQuery(id+"F0.wireOp",EDGE,"E25.MirrorCS");var subQ2=sQuery(id+"F0.wireOp",EDGE,"E2");var subQ3=sQuery(id+"F0.wireOp",EDGE,"E0");Q55=makeQuery(id+"F5.boolean.opBoolean","SPLIT",FACE,{"disambiguationData":[TD([makeQuery(id+"F5.opSweep","SWEPT_FACE",FACE,{"disambiguationData":[OSD([subQ3,sQuery(id+"F4.wireOp",EDGE,"E30")])]})])],"derivedFrom":makeQuery(id+"F1.opExtrude","SWEPT_FACE",FACE,{"disambiguationData":[OSD([subQ2]),TDD([makeQuery(id+"F0.imprint","IMPRINT",EDGE,{"disambiguationData":[TD([[makeQuery(id+"F0.imprint","INTERSECT",VERTEX,{"derivedFrom":[subQ2,subQ1]}),1.0]])],"derivedFrom":subQ2})])]})});}
            var Q56;
            {var subQ1=sQuery(id+"F0.wireOp",EDGE,"E10");var subQ2=sQuery(id+"F0.wireOp",EDGE,"E2");var subQ3=sQuery(id+"F0.wireOp",EDGE,"E0");Q56=makeQuery(id+"F5.boolean.opBoolean","SPLIT",FACE,{"disambiguationData":[TD([makeQuery(id+"F5.opSweep","SWEPT_FACE",FACE,{"disambiguationData":[OSD([subQ3,sQuery(id+"F4.wireOp",EDGE,"E30")])]})])],"derivedFrom":makeQuery(id+"F1.opExtrude","SWEPT_FACE",FACE,{"disambiguationData":[OSD([subQ2]),TDD([makeQuery(id+"F0.imprint","IMPRINT",EDGE,{"disambiguationData":[TD([[makeQuery(id+"F0.imprint","INTERSECT",VERTEX,{"derivedFrom":[subQ2,subQ1]}),-1.0]])],"derivedFrom":subQ2})])]})});}
            var Q57;
            {var subQ0=sQuery(id+"F0.wireOp",EDGE,"E10");var subQ2=sQuery(id+"F0.wireOp",EDGE,"E0");var subQ3=sQuery(id+"F0.wireOp",EDGE,"E2");Q57=makeQuery(id+"F5.boolean.opBoolean","SPLIT",FACE,{"disambiguationData":[TD([makeQuery(id+"F5.opSweep","SWEPT_FACE",FACE,{"disambiguationData":[OSD([subQ2,sQuery(id+"F4.wireOp",EDGE,"E31")])]})])],"derivedFrom":makeQuery(id+"F1.opExtrude","SWEPT_FACE",FACE,{"disambiguationData":[OSD([subQ3]),TDD([makeQuery(id+"F0.imprint","IMPRINT",EDGE,{"disambiguationData":[TD([[makeQuery(id+"F0.imprint","INTERSECT",VERTEX,{"derivedFrom":[subQ3,subQ0]}),-1.0]])],"derivedFrom":subQ3})])]})});}
            var Q58;
            {var subQ0=sQuery(id+"F0.wireOp",EDGE,"E10");var subQ2=sQuery(id+"F0.wireOp",EDGE,"E0");var subQ3=sQuery(id+"F0.wireOp",EDGE,"E2");Q58=makeQuery(id+"F5.boolean.opBoolean","SPLIT",FACE,{"disambiguationData":[TD([makeQuery(id+"F5.opSweep","SWEPT_FACE",FACE,{"disambiguationData":[OSD([subQ2,sQuery(id+"F4.wireOp",EDGE,"E33.MirrorCS")])]})])],"derivedFrom":makeQuery(id+"F1.opExtrude","SWEPT_FACE",FACE,{"disambiguationData":[OSD([subQ3]),TDD([makeQuery(id+"F0.imprint","IMPRINT",EDGE,{"disambiguationData":[TD([[makeQuery(id+"F0.imprint","INTERSECT",VERTEX,{"derivedFrom":[subQ3,subQ0]}),-1.0]])],"derivedFrom":subQ3})])]})});}
            var Q59;
            {var subQ0=sQuery(id+"F0.wireOp",EDGE,"E10");var subQ1=sQuery(id+"F0.wireOp",EDGE,"E0");var subQ3=sQuery(id+"F0.wireOp",EDGE,"E2");Q59=makeQuery(id+"F5.boolean.opBoolean","SPLIT",FACE,{"disambiguationData":[TD([makeQuery(id+"F5.opSweep","SWEPT_FACE",FACE,{"disambiguationData":[OSD([subQ1,sQuery(id+"F4.wireOp",EDGE,"E35.MirrorCS")])]})])],"derivedFrom":makeQuery(id+"F1.opExtrude","SWEPT_FACE",FACE,{"disambiguationData":[OSD([subQ3]),TDD([makeQuery(id+"F0.imprint","IMPRINT",EDGE,{"disambiguationData":[TD([[makeQuery(id+"F0.imprint","INTERSECT",VERTEX,{"derivedFrom":[subQ3,subQ0]}),-1.0]])],"derivedFrom":subQ3})])]})});}
            var Q60;
            {var subQ0=sQuery(id+"F0.wireOp",EDGE,"E10");var subQ2=sQuery(id+"F0.wireOp",EDGE,"E0");var subQ3=sQuery(id+"F0.wireOp",EDGE,"E2");Q60=makeQuery(id+"F5.boolean.opBoolean","SPLIT",FACE,{"disambiguationData":[TD([makeQuery(id+"F5.opSweep","SWEPT_FACE",FACE,{"disambiguationData":[OSD([subQ2,sQuery(id+"F4.wireOp",EDGE,"E37.MirrorCS")])]})])],"derivedFrom":makeQuery(id+"F1.opExtrude","SWEPT_FACE",FACE,{"disambiguationData":[OSD([subQ3]),TDD([makeQuery(id+"F0.imprint","IMPRINT",EDGE,{"disambiguationData":[TD([[makeQuery(id+"F0.imprint","INTERSECT",VERTEX,{"derivedFrom":[subQ3,subQ0]}),-1.0]])],"derivedFrom":subQ3})])]})});}
            var Q61;
            {var subQ0=sQuery(id+"F0.wireOp",EDGE,"E10");var subQ1=sQuery(id+"F0.wireOp",EDGE,"E0");var subQ3=sQuery(id+"F0.wireOp",EDGE,"E2");Q61=makeQuery(id+"F5.boolean.opBoolean","SPLIT",FACE,{"disambiguationData":[TD([makeQuery(id+"F5.opSweep","SWEPT_FACE",FACE,{"disambiguationData":[OSD([subQ1,sQuery(id+"F4.wireOp",EDGE,"E39.MirrorCS")])]})])],"derivedFrom":makeQuery(id+"F1.opExtrude","SWEPT_FACE",FACE,{"disambiguationData":[OSD([subQ3]),TDD([makeQuery(id+"F0.imprint","IMPRINT",EDGE,{"disambiguationData":[TD([[makeQuery(id+"F0.imprint","INTERSECT",VERTEX,{"derivedFrom":[subQ3,subQ0]}),-1.0]])],"derivedFrom":subQ3})])]})});}
            var Q62;
            {var subQ0=sQuery(id+"F0.wireOp",EDGE,"E10");var subQ2=sQuery(id+"F0.wireOp",EDGE,"E0");var subQ3=sQuery(id+"F0.wireOp",EDGE,"E2");Q62=makeQuery(id+"F5.boolean.opBoolean","SPLIT",FACE,{"disambiguationData":[TD([makeQuery(id+"F5.opSweep","SWEPT_FACE",FACE,{"disambiguationData":[OSD([subQ2,sQuery(id+"F4.wireOp",EDGE,"E41.MirrorCS")])]})])],"derivedFrom":makeQuery(id+"F1.opExtrude","SWEPT_FACE",FACE,{"disambiguationData":[OSD([subQ3]),TDD([makeQuery(id+"F0.imprint","IMPRINT",EDGE,{"disambiguationData":[TD([[makeQuery(id+"F0.imprint","INTERSECT",VERTEX,{"derivedFrom":[subQ3,subQ0]}),-1.0]])],"derivedFrom":subQ3})])]})});}
            var Q63;
            {var subQ0=sQuery(id+"F0.wireOp",EDGE,"E5");var subQ2=sQuery(id+"F0.wireOp",EDGE,"E0");var subQ3=sQuery(id+"F0.wireOp",EDGE,"E2");Q63=makeQuery(id+"F5.boolean.opBoolean","SPLIT",FACE,{"disambiguationData":[TD([makeQuery(id+"F5.opSweep","SWEPT_FACE",FACE,{"disambiguationData":[OSD([subQ2,sQuery(id+"F4.wireOp",EDGE,"E41.MirrorCS")])]})])],"derivedFrom":makeQuery(id+"F1.opExtrude","SWEPT_FACE",FACE,{"disambiguationData":[OSD([subQ3]),TDD([makeQuery(id+"F0.imprint","IMPRINT",EDGE,{"disambiguationData":[TD([[makeQuery(id+"F0.imprint","INTERSECT",VERTEX,{"derivedFrom":[subQ3,subQ0]}),1.0]])],"derivedFrom":subQ3})])]})});}
            var Q64;
            {var subQ0=sQuery(id+"F0.wireOp",EDGE,"E5");var subQ1=sQuery(id+"F0.wireOp",EDGE,"E0");var subQ3=sQuery(id+"F0.wireOp",EDGE,"E2");Q64=makeQuery(id+"F5.boolean.opBoolean","SPLIT",FACE,{"disambiguationData":[TD([makeQuery(id+"F5.opSweep","SWEPT_FACE",FACE,{"disambiguationData":[OSD([subQ1,sQuery(id+"F4.wireOp",EDGE,"E39.MirrorCS")])]})])],"derivedFrom":makeQuery(id+"F1.opExtrude","SWEPT_FACE",FACE,{"disambiguationData":[OSD([subQ3]),TDD([makeQuery(id+"F0.imprint","IMPRINT",EDGE,{"disambiguationData":[TD([[makeQuery(id+"F0.imprint","INTERSECT",VERTEX,{"derivedFrom":[subQ3,subQ0]}),1.0]])],"derivedFrom":subQ3})])]})});}
            var Q65;
            {var subQ0=sQuery(id+"F0.wireOp",EDGE,"E5");var subQ2=sQuery(id+"F0.wireOp",EDGE,"E0");var subQ3=sQuery(id+"F0.wireOp",EDGE,"E2");Q65=makeQuery(id+"F5.boolean.opBoolean","SPLIT",FACE,{"disambiguationData":[TD([makeQuery(id+"F5.opSweep","SWEPT_FACE",FACE,{"disambiguationData":[OSD([subQ2,sQuery(id+"F4.wireOp",EDGE,"E37.MirrorCS")])]})])],"derivedFrom":makeQuery(id+"F1.opExtrude","SWEPT_FACE",FACE,{"disambiguationData":[OSD([subQ3]),TDD([makeQuery(id+"F0.imprint","IMPRINT",EDGE,{"disambiguationData":[TD([[makeQuery(id+"F0.imprint","INTERSECT",VERTEX,{"derivedFrom":[subQ3,subQ0]}),1.0]])],"derivedFrom":subQ3})])]})});}
            var Q66;
            {var subQ0=sQuery(id+"F0.wireOp",EDGE,"E5");var subQ1=sQuery(id+"F0.wireOp",EDGE,"E0");var subQ3=sQuery(id+"F0.wireOp",EDGE,"E2");Q66=makeQuery(id+"F5.boolean.opBoolean","SPLIT",FACE,{"disambiguationData":[TD([makeQuery(id+"F5.opSweep","SWEPT_FACE",FACE,{"disambiguationData":[OSD([subQ1,sQuery(id+"F4.wireOp",EDGE,"E35.MirrorCS")])]})])],"derivedFrom":makeQuery(id+"F1.opExtrude","SWEPT_FACE",FACE,{"disambiguationData":[OSD([subQ3]),TDD([makeQuery(id+"F0.imprint","IMPRINT",EDGE,{"disambiguationData":[TD([[makeQuery(id+"F0.imprint","INTERSECT",VERTEX,{"derivedFrom":[subQ3,subQ0]}),1.0]])],"derivedFrom":subQ3})])]})});}
            var Q67;
            {var subQ0=sQuery(id+"F0.wireOp",EDGE,"E5");var subQ2=sQuery(id+"F0.wireOp",EDGE,"E0");var subQ3=sQuery(id+"F0.wireOp",EDGE,"E2");Q67=makeQuery(id+"F5.boolean.opBoolean","SPLIT",FACE,{"disambiguationData":[TD([makeQuery(id+"F5.opSweep","SWEPT_FACE",FACE,{"disambiguationData":[OSD([subQ2,sQuery(id+"F4.wireOp",EDGE,"E33.MirrorCS")])]})])],"derivedFrom":makeQuery(id+"F1.opExtrude","SWEPT_FACE",FACE,{"disambiguationData":[OSD([subQ3]),TDD([makeQuery(id+"F0.imprint","IMPRINT",EDGE,{"disambiguationData":[TD([[makeQuery(id+"F0.imprint","INTERSECT",VERTEX,{"derivedFrom":[subQ3,subQ0]}),1.0]])],"derivedFrom":subQ3})])]})});}
            var Q68;
            {var subQ0=sQuery(id+"F0.wireOp",EDGE,"E5");var subQ2=sQuery(id+"F0.wireOp",EDGE,"E0");var subQ3=sQuery(id+"F0.wireOp",EDGE,"E2");Q68=makeQuery(id+"F5.boolean.opBoolean","SPLIT",FACE,{"disambiguationData":[TD([makeQuery(id+"F5.opSweep","SWEPT_FACE",FACE,{"disambiguationData":[OSD([subQ2,sQuery(id+"F4.wireOp",EDGE,"E31")])]})])],"derivedFrom":makeQuery(id+"F1.opExtrude","SWEPT_FACE",FACE,{"disambiguationData":[OSD([subQ3]),TDD([makeQuery(id+"F0.imprint","IMPRINT",EDGE,{"disambiguationData":[TD([[makeQuery(id+"F0.imprint","INTERSECT",VERTEX,{"derivedFrom":[subQ3,subQ0]}),1.0]])],"derivedFrom":subQ3})])]})});}
            var Q69;
            {var subQ1=sQuery(id+"F0.wireOp",EDGE,"E5");var subQ2=sQuery(id+"F0.wireOp",EDGE,"E2");var subQ3=sQuery(id+"F0.wireOp",EDGE,"E0");Q69=makeQuery(id+"F5.boolean.opBoolean","SPLIT",FACE,{"disambiguationData":[TD([makeQuery(id+"F5.opSweep","SWEPT_FACE",FACE,{"disambiguationData":[OSD([subQ3,sQuery(id+"F4.wireOp",EDGE,"E30")])]})])],"derivedFrom":makeQuery(id+"F1.opExtrude","SWEPT_FACE",FACE,{"disambiguationData":[OSD([subQ2]),TDD([makeQuery(id+"F0.imprint","IMPRINT",EDGE,{"disambiguationData":[TD([[makeQuery(id+"F0.imprint","INTERSECT",VERTEX,{"derivedFrom":[subQ2,subQ1]}),1.0]])],"derivedFrom":subQ2})])]})});}
            var Q70;
            {var subQ1=sQuery(id+"F0.wireOp",EDGE,"E7");var subQ2=sQuery(id+"F0.wireOp",EDGE,"E2");var subQ3=sQuery(id+"F0.wireOp",EDGE,"E0");Q70=makeQuery(id+"F5.boolean.opBoolean","SPLIT",FACE,{"disambiguationData":[TD([makeQuery(id+"F5.opSweep","SWEPT_FACE",FACE,{"disambiguationData":[OSD([subQ3,sQuery(id+"F4.wireOp",EDGE,"E30")])]})])],"derivedFrom":makeQuery(id+"F1.opExtrude","SWEPT_FACE",FACE,{"disambiguationData":[OSD([subQ2]),TDD([makeQuery(id+"F0.imprint","IMPRINT",EDGE,{"disambiguationData":[TD([[makeQuery(id+"F0.imprint","INTERSECT",VERTEX,{"derivedFrom":[subQ2,subQ1]}),1.0]])],"derivedFrom":subQ2})])]})});}
            var Q71;
            {var subQ0=sQuery(id+"F0.wireOp",EDGE,"E7");var subQ1=sQuery(id+"F0.wireOp",EDGE,"E0");var subQ3=sQuery(id+"F0.wireOp",EDGE,"E2");Q71=makeQuery(id+"F5.boolean.opBoolean","SPLIT",FACE,{"disambiguationData":[TD([makeQuery(id+"F5.opSweep","SWEPT_FACE",FACE,{"disambiguationData":[OSD([subQ1,sQuery(id+"F4.wireOp",EDGE,"E31")])]})])],"derivedFrom":makeQuery(id+"F1.opExtrude","SWEPT_FACE",FACE,{"disambiguationData":[OSD([subQ3]),TDD([makeQuery(id+"F0.imprint","IMPRINT",EDGE,{"disambiguationData":[TD([[makeQuery(id+"F0.imprint","INTERSECT",VERTEX,{"derivedFrom":[subQ3,subQ0]}),1.0]])],"derivedFrom":subQ3})])]})});}
            var Q72;
            {var subQ0=sQuery(id+"F0.wireOp",EDGE,"E7");var subQ2=sQuery(id+"F0.wireOp",EDGE,"E0");var subQ3=sQuery(id+"F0.wireOp",EDGE,"E2");Q72=makeQuery(id+"F5.boolean.opBoolean","SPLIT",FACE,{"disambiguationData":[TD([makeQuery(id+"F5.opSweep","SWEPT_FACE",FACE,{"disambiguationData":[OSD([subQ2,sQuery(id+"F4.wireOp",EDGE,"E33.MirrorCS")])]})])],"derivedFrom":makeQuery(id+"F1.opExtrude","SWEPT_FACE",FACE,{"disambiguationData":[OSD([subQ3]),TDD([makeQuery(id+"F0.imprint","IMPRINT",EDGE,{"disambiguationData":[TD([[makeQuery(id+"F0.imprint","INTERSECT",VERTEX,{"derivedFrom":[subQ3,subQ0]}),1.0]])],"derivedFrom":subQ3})])]})});}
            var Q73;
            {var subQ0=sQuery(id+"F0.wireOp",EDGE,"E7");var subQ2=sQuery(id+"F0.wireOp",EDGE,"E0");var subQ3=sQuery(id+"F0.wireOp",EDGE,"E2");Q73=makeQuery(id+"F5.boolean.opBoolean","SPLIT",FACE,{"disambiguationData":[TD([makeQuery(id+"F5.opSweep","SWEPT_FACE",FACE,{"disambiguationData":[OSD([subQ2,sQuery(id+"F4.wireOp",EDGE,"E35.MirrorCS")])]})])],"derivedFrom":makeQuery(id+"F1.opExtrude","SWEPT_FACE",FACE,{"disambiguationData":[OSD([subQ3]),TDD([makeQuery(id+"F0.imprint","IMPRINT",EDGE,{"disambiguationData":[TD([[makeQuery(id+"F0.imprint","INTERSECT",VERTEX,{"derivedFrom":[subQ3,subQ0]}),1.0]])],"derivedFrom":subQ3})])]})});}
            var Q74;
            {var subQ0=sQuery(id+"F0.wireOp",EDGE,"E7");var subQ1=sQuery(id+"F0.wireOp",EDGE,"E0");var subQ3=sQuery(id+"F0.wireOp",EDGE,"E2");Q74=makeQuery(id+"F5.boolean.opBoolean","SPLIT",FACE,{"disambiguationData":[TD([makeQuery(id+"F5.opSweep","SWEPT_FACE",FACE,{"disambiguationData":[OSD([subQ1,sQuery(id+"F4.wireOp",EDGE,"E37.MirrorCS")])]})])],"derivedFrom":makeQuery(id+"F1.opExtrude","SWEPT_FACE",FACE,{"disambiguationData":[OSD([subQ3]),TDD([makeQuery(id+"F0.imprint","IMPRINT",EDGE,{"disambiguationData":[TD([[makeQuery(id+"F0.imprint","INTERSECT",VERTEX,{"derivedFrom":[subQ3,subQ0]}),1.0]])],"derivedFrom":subQ3})])]})});}
            var Q75;
            {var subQ0=sQuery(id+"F0.wireOp",EDGE,"E7");var subQ2=sQuery(id+"F0.wireOp",EDGE,"E0");var subQ3=sQuery(id+"F0.wireOp",EDGE,"E2");Q75=makeQuery(id+"F5.boolean.opBoolean","SPLIT",FACE,{"disambiguationData":[TD([makeQuery(id+"F5.opSweep","SWEPT_FACE",FACE,{"disambiguationData":[OSD([subQ2,sQuery(id+"F4.wireOp",EDGE,"E39.MirrorCS")])]})])],"derivedFrom":makeQuery(id+"F1.opExtrude","SWEPT_FACE",FACE,{"disambiguationData":[OSD([subQ3]),TDD([makeQuery(id+"F0.imprint","IMPRINT",EDGE,{"disambiguationData":[TD([[makeQuery(id+"F0.imprint","INTERSECT",VERTEX,{"derivedFrom":[subQ3,subQ0]}),1.0]])],"derivedFrom":subQ3})])]})});}
            var Q76;
            {var subQ0=sQuery(id+"F0.wireOp",EDGE,"E7");var subQ1=sQuery(id+"F0.wireOp",EDGE,"E0");var subQ3=sQuery(id+"F0.wireOp",EDGE,"E2");Q76=makeQuery(id+"F5.boolean.opBoolean","SPLIT",FACE,{"disambiguationData":[TD([makeQuery(id+"F5.opSweep","SWEPT_FACE",FACE,{"disambiguationData":[OSD([subQ1,sQuery(id+"F4.wireOp",EDGE,"E41.MirrorCS")])]})])],"derivedFrom":makeQuery(id+"F1.opExtrude","SWEPT_FACE",FACE,{"disambiguationData":[OSD([subQ3]),TDD([makeQuery(id+"F0.imprint","IMPRINT",EDGE,{"disambiguationData":[TD([[makeQuery(id+"F0.imprint","INTERSECT",VERTEX,{"derivedFrom":[subQ3,subQ0]}),1.0]])],"derivedFrom":subQ3})])]})});}
            var Q77;
            {var subQ0=sQuery(id+"F0.wireOp",EDGE,"E3");var subQ2=sQuery(id+"F0.wireOp",EDGE,"E0");var subQ3=sQuery(id+"F0.wireOp",EDGE,"E2");Q77=makeQuery(id+"F5.boolean.opBoolean","SPLIT",FACE,{"disambiguationData":[TD([makeQuery(id+"F5.opSweep","SWEPT_FACE",FACE,{"disambiguationData":[OSD([subQ2,sQuery(id+"F4.wireOp",EDGE,"E41.MirrorCS")])]})])],"derivedFrom":makeQuery(id+"F1.opExtrude","SWEPT_FACE",FACE,{"disambiguationData":[OSD([subQ3]),TDD([makeQuery(id+"F0.imprint","IMPRINT",EDGE,{"disambiguationData":[TD([[makeQuery(id+"F0.imprint","INTERSECT",VERTEX,{"derivedFrom":[subQ3,subQ0]}),-1.0]])],"derivedFrom":subQ3})])]})});}
            var Q78;
            {var subQ0=sQuery(id+"F0.wireOp",EDGE,"E3");var subQ2=sQuery(id+"F0.wireOp",EDGE,"E0");var subQ3=sQuery(id+"F0.wireOp",EDGE,"E2");Q78=makeQuery(id+"F5.boolean.opBoolean","SPLIT",FACE,{"disambiguationData":[TD([makeQuery(id+"F5.opSweep","SWEPT_FACE",FACE,{"disambiguationData":[OSD([subQ2,sQuery(id+"F4.wireOp",EDGE,"E39.MirrorCS")])]})])],"derivedFrom":makeQuery(id+"F1.opExtrude","SWEPT_FACE",FACE,{"disambiguationData":[OSD([subQ3]),TDD([makeQuery(id+"F0.imprint","IMPRINT",EDGE,{"disambiguationData":[TD([[makeQuery(id+"F0.imprint","INTERSECT",VERTEX,{"derivedFrom":[subQ3,subQ0]}),-1.0]])],"derivedFrom":subQ3})])]})});}
            var Q79;
            {var subQ0=sQuery(id+"F0.wireOp",EDGE,"E3");var subQ2=sQuery(id+"F0.wireOp",EDGE,"E0");var subQ3=sQuery(id+"F0.wireOp",EDGE,"E2");Q79=makeQuery(id+"F5.boolean.opBoolean","SPLIT",FACE,{"disambiguationData":[TD([makeQuery(id+"F5.opSweep","SWEPT_FACE",FACE,{"disambiguationData":[OSD([subQ2,sQuery(id+"F4.wireOp",EDGE,"E37.MirrorCS")])]})])],"derivedFrom":makeQuery(id+"F1.opExtrude","SWEPT_FACE",FACE,{"disambiguationData":[OSD([subQ3]),TDD([makeQuery(id+"F0.imprint","IMPRINT",EDGE,{"disambiguationData":[TD([[makeQuery(id+"F0.imprint","INTERSECT",VERTEX,{"derivedFrom":[subQ3,subQ0]}),-1.0]])],"derivedFrom":subQ3})])]})});}
            var Q80;
            {var subQ0=sQuery(id+"F0.wireOp",EDGE,"E3");var subQ2=sQuery(id+"F0.wireOp",EDGE,"E0");var subQ3=sQuery(id+"F0.wireOp",EDGE,"E2");Q80=makeQuery(id+"F5.boolean.opBoolean","SPLIT",FACE,{"disambiguationData":[TD([makeQuery(id+"F5.opSweep","SWEPT_FACE",FACE,{"disambiguationData":[OSD([subQ2,sQuery(id+"F4.wireOp",EDGE,"E35.MirrorCS")])]})])],"derivedFrom":makeQuery(id+"F1.opExtrude","SWEPT_FACE",FACE,{"disambiguationData":[OSD([subQ3]),TDD([makeQuery(id+"F0.imprint","IMPRINT",EDGE,{"disambiguationData":[TD([[makeQuery(id+"F0.imprint","INTERSECT",VERTEX,{"derivedFrom":[subQ3,subQ0]}),-1.0]])],"derivedFrom":subQ3})])]})});}
            var Q81;
            {var subQ0=sQuery(id+"F0.wireOp",EDGE,"E3");var subQ2=sQuery(id+"F0.wireOp",EDGE,"E0");var subQ3=sQuery(id+"F0.wireOp",EDGE,"E2");Q81=makeQuery(id+"F5.boolean.opBoolean","SPLIT",FACE,{"disambiguationData":[TD([makeQuery(id+"F5.opSweep","SWEPT_FACE",FACE,{"disambiguationData":[OSD([subQ2,sQuery(id+"F4.wireOp",EDGE,"E33.MirrorCS")])]})])],"derivedFrom":makeQuery(id+"F1.opExtrude","SWEPT_FACE",FACE,{"disambiguationData":[OSD([subQ3]),TDD([makeQuery(id+"F0.imprint","IMPRINT",EDGE,{"disambiguationData":[TD([[makeQuery(id+"F0.imprint","INTERSECT",VERTEX,{"derivedFrom":[subQ3,subQ0]}),-1.0]])],"derivedFrom":subQ3})])]})});}
            var Q82;
            {var subQ0=sQuery(id+"F0.wireOp",EDGE,"E3");var subQ2=sQuery(id+"F0.wireOp",EDGE,"E0");var subQ3=sQuery(id+"F0.wireOp",EDGE,"E2");Q82=makeQuery(id+"F5.boolean.opBoolean","SPLIT",FACE,{"disambiguationData":[TD([makeQuery(id+"F5.opSweep","SWEPT_FACE",FACE,{"disambiguationData":[OSD([subQ2,sQuery(id+"F4.wireOp",EDGE,"E31")])]})])],"derivedFrom":makeQuery(id+"F1.opExtrude","SWEPT_FACE",FACE,{"disambiguationData":[OSD([subQ3]),TDD([makeQuery(id+"F0.imprint","IMPRINT",EDGE,{"disambiguationData":[TD([[makeQuery(id+"F0.imprint","INTERSECT",VERTEX,{"derivedFrom":[subQ3,subQ0]}),-1.0]])],"derivedFrom":subQ3})])]})});}
            var Q83;
            {var subQ1=sQuery(id+"F0.wireOp",EDGE,"E3");var subQ2=sQuery(id+"F0.wireOp",EDGE,"E2");var subQ3=sQuery(id+"F0.wireOp",EDGE,"E0");Q83=makeQuery(id+"F5.boolean.opBoolean","SPLIT",FACE,{"disambiguationData":[TD([makeQuery(id+"F5.opSweep","SWEPT_FACE",FACE,{"disambiguationData":[OSD([subQ3,sQuery(id+"F4.wireOp",EDGE,"E30")])]})])],"derivedFrom":makeQuery(id+"F1.opExtrude","SWEPT_FACE",FACE,{"disambiguationData":[OSD([subQ2]),TDD([makeQuery(id+"F0.imprint","IMPRINT",EDGE,{"disambiguationData":[TD([[makeQuery(id+"F0.imprint","INTERSECT",VERTEX,{"derivedFrom":[subQ2,subQ1]}),-1.0]])],"derivedFrom":subQ2})])]})});}
            fillet(context, id + "F6", {"entities" : qUnion([Q0, Q1, Q2, Q3, Q4, Q5, Q6, Q7, Q8, Q9, Q10, Q11, Q12, Q13, Q14, Q15, Q16, Q17, Q18, Q19, Q20, Q21, Q22, Q23, Q24, Q25, Q26, Q27, Q28, Q29, Q30, Q31, Q32, Q33, Q34, Q35, Q36, Q37, Q38, Q39, Q40, Q41, Q42, Q43, Q44, Q45, Q46, Q47, Q48, Q49, Q50, Q51, Q52, Q53, Q54, Q55, Q56, Q57, Q58, Q59, Q60, Q61, Q62, Q63, Q64, Q65, Q66, Q67, Q68, Q69, Q70, Q71, Q72, Q73, Q74, Q75, Q76, Q77, Q78, Q79, Q80, Q81, Q82, Q83]), "radius" : 1 * mm, "tangentPropagation" : true, "allowEdgeOverflow" : false});
        }
        {
            var Q0;
            {var subQ0=sQuery(id+"F0.wireOp",EDGE,"E2");var subQ1=sQuery(id+"F0.wireOp",EDGE,"E9");Q0=makeQuery(id+"F5.boolean.opBoolean","SPLIT",EDGE,{"disambiguationData":[TD([makeQuery(id+"F3.opExtrude","CAP_FACE",FACE,{"disambiguationData":[OSD([sQuery(id+"F2.wireOp",EDGE,"E29")])],"isStart":true})])],"derivedFrom":makeQuery(id+"F1.opExtrude","SWEPT_EDGE",EDGE,{"disambiguationData":[OSD([subQ0,subQ1])]})});}
            var Q1;
            {var subQ0=sQuery(id+"F0.wireOp",EDGE,"E2");var subQ1=sQuery(id+"F4.wireOp",EDGE,"E43.MirrorCS");var subQ2=sQuery(id+"F0.wireOp",EDGE,"E0");Q1=makeQuery(id+"F5.boolean.opBoolean","COPY",EDGE,{"disambiguationData":[topologyDisambiguationEdgeConnected([makeQuery(id+"F1.opExtrude","SWEPT_FACE",FACE,{"disambiguationData":[OSD([subQ0]),TDD([makeQuery(id+"F0.imprint","IMPRINT",EDGE,{"disambiguationData":[TD([[makeQuery(id+"F0.imprint","INTERSECT",VERTEX,{"derivedFrom":[subQ0,sQuery(id+"F0.wireOp",EDGE,"E3")]}),-1.0]])],"derivedFrom":subQ0})])]})])],"derivedFrom":makeQuery(id+"F5.opSweep","SWEPT_EDGE",EDGE,{"disambiguationData":[OSD([subQ2,subQ0,sQuery(id+"F0.wireOp",EDGE,"E27.MirrorCS"),subQ1])]})});}
            var Q2;
            {var subQ0=sQuery(id+"F0.wireOp",EDGE,"E3");var subQ1=sQuery(id+"F0.wireOp",EDGE,"E2");Q2=makeQuery(id+"F5.boolean.opBoolean","SPLIT",EDGE,{"disambiguationData":[TD([makeQuery(id+"F3.opExtrude","CAP_FACE",FACE,{"disambiguationData":[OSD([sQuery(id+"F2.wireOp",EDGE,"E29")])],"isStart":true})])],"derivedFrom":makeQuery(id+"F1.opExtrude","SWEPT_EDGE",EDGE,{"disambiguationData":[OSD([subQ1,subQ0])]})});}
            var Q3;
            {var subQ0=sQuery(id+"F0.wireOp",EDGE,"E2");var subQ1=sQuery(id+"F0.wireOp",EDGE,"E8");Q3=makeQuery(id+"F5.boolean.opBoolean","SPLIT",EDGE,{"disambiguationData":[TD([makeQuery(id+"F3.opExtrude","CAP_FACE",FACE,{"disambiguationData":[OSD([sQuery(id+"F2.wireOp",EDGE,"E29")])],"isStart":true})])],"derivedFrom":makeQuery(id+"F1.opExtrude","SWEPT_EDGE",EDGE,{"disambiguationData":[OSD([subQ0,subQ1])]})});}
            var Q4;
            {var subQ0=sQuery(id+"F0.wireOp",EDGE,"E2");var subQ1=sQuery(id+"F4.wireOp",EDGE,"E43.MirrorCS");var subQ2=sQuery(id+"F0.wireOp",EDGE,"E0");Q4=makeQuery(id+"F5.boolean.opBoolean","COPY",EDGE,{"disambiguationData":[topologyDisambiguationEdgeConnected([makeQuery(id+"F1.opExtrude","SWEPT_FACE",FACE,{"disambiguationData":[OSD([subQ0]),TDD([makeQuery(id+"F0.imprint","IMPRINT",EDGE,{"disambiguationData":[TD([[makeQuery(id+"F0.imprint","INTERSECT",VERTEX,{"derivedFrom":[subQ0,sQuery(id+"F0.wireOp",EDGE,"E7")]}),1.0]])],"derivedFrom":subQ0})])]})])],"derivedFrom":makeQuery(id+"F5.opSweep","SWEPT_EDGE",EDGE,{"disambiguationData":[OSD([subQ2,subQ0,sQuery(id+"F0.wireOp",EDGE,"E27.MirrorCS"),subQ1])]})});}
            var Q5;
            {var subQ0=sQuery(id+"F0.wireOp",EDGE,"E7");var subQ1=sQuery(id+"F0.wireOp",EDGE,"E2");Q5=makeQuery(id+"F5.boolean.opBoolean","SPLIT",EDGE,{"disambiguationData":[TD([makeQuery(id+"F3.opExtrude","CAP_FACE",FACE,{"disambiguationData":[OSD([sQuery(id+"F2.wireOp",EDGE,"E29")])],"isStart":true})])],"derivedFrom":makeQuery(id+"F1.opExtrude","SWEPT_EDGE",EDGE,{"disambiguationData":[OSD([subQ1,subQ0])]})});}
            var Q6;
            {var subQ0=sQuery(id+"F0.wireOp",EDGE,"E2");var subQ1=sQuery(id+"F0.wireOp",EDGE,"E6");Q6=makeQuery(id+"F5.boolean.opBoolean","SPLIT",EDGE,{"disambiguationData":[TD([makeQuery(id+"F3.opExtrude","CAP_FACE",FACE,{"disambiguationData":[OSD([sQuery(id+"F2.wireOp",EDGE,"E29")])],"isStart":true})])],"derivedFrom":makeQuery(id+"F1.opExtrude","SWEPT_EDGE",EDGE,{"disambiguationData":[OSD([subQ0,subQ1])]})});}
            var Q7;
            {var subQ0=sQuery(id+"F0.wireOp",EDGE,"E2");var subQ1=sQuery(id+"F4.wireOp",EDGE,"E43.MirrorCS");var subQ2=sQuery(id+"F0.wireOp",EDGE,"E0");Q7=makeQuery(id+"F5.boolean.opBoolean","COPY",EDGE,{"disambiguationData":[topologyDisambiguationEdgeConnected([makeQuery(id+"F1.opExtrude","SWEPT_FACE",FACE,{"disambiguationData":[OSD([subQ0]),TDD([makeQuery(id+"F0.imprint","IMPRINT",EDGE,{"disambiguationData":[TD([[makeQuery(id+"F0.imprint","INTERSECT",VERTEX,{"derivedFrom":[subQ0,sQuery(id+"F0.wireOp",EDGE,"E5")]}),1.0]])],"derivedFrom":subQ0})])]})])],"derivedFrom":makeQuery(id+"F5.opSweep","SWEPT_EDGE",EDGE,{"disambiguationData":[OSD([subQ2,subQ0,sQuery(id+"F0.wireOp",EDGE,"E27.MirrorCS"),subQ1])]})});}
            var Q8;
            {var subQ0=sQuery(id+"F0.wireOp",EDGE,"E5");var subQ1=sQuery(id+"F0.wireOp",EDGE,"E2");Q8=makeQuery(id+"F5.boolean.opBoolean","SPLIT",EDGE,{"disambiguationData":[TD([makeQuery(id+"F3.opExtrude","CAP_FACE",FACE,{"disambiguationData":[OSD([sQuery(id+"F2.wireOp",EDGE,"E29")])],"isStart":true})])],"derivedFrom":makeQuery(id+"F1.opExtrude","SWEPT_EDGE",EDGE,{"disambiguationData":[OSD([subQ1,subQ0])]})});}
            var Q9;
            {var subQ0=sQuery(id+"F0.wireOp",EDGE,"E10");var subQ1=sQuery(id+"F0.wireOp",EDGE,"E2");Q9=makeQuery(id+"F5.boolean.opBoolean","SPLIT",EDGE,{"disambiguationData":[TD([makeQuery(id+"F3.opExtrude","CAP_FACE",FACE,{"disambiguationData":[OSD([sQuery(id+"F2.wireOp",EDGE,"E29")])],"isStart":true})])],"derivedFrom":makeQuery(id+"F1.opExtrude","SWEPT_EDGE",EDGE,{"disambiguationData":[OSD([subQ1,subQ0])]})});}
            var Q10;
            {var subQ0=sQuery(id+"F0.wireOp",EDGE,"E2");var subQ1=sQuery(id+"F0.wireOp",EDGE,"E27.MirrorCS");Q10=makeQuery(id+"F5.boolean.opBoolean","SPLIT",EDGE,{"disambiguationData":[TD([makeQuery(id+"F3.opExtrude","CAP_FACE",FACE,{"disambiguationData":[OSD([sQuery(id+"F2.wireOp",EDGE,"E29")])],"isStart":true})])],"derivedFrom":makeQuery(id+"F1.opExtrude","SWEPT_EDGE",EDGE,{"disambiguationData":[OSD([subQ0,subQ1])]})});}
            var Q11;
            {var subQ0=sQuery(id+"F0.wireOp",EDGE,"E2");var subQ1=sQuery(id+"F0.wireOp",EDGE,"E27.MirrorCS");var subQ2=sQuery(id+"F4.wireOp",EDGE,"E43.MirrorCS");var subQ3=sQuery(id+"F0.wireOp",EDGE,"E0");Q11=makeQuery(id+"F5.boolean.opBoolean","COPY",EDGE,{"disambiguationData":[topologyDisambiguationEdgeConnected([makeQuery(id+"F1.opExtrude","SWEPT_FACE",FACE,{"disambiguationData":[OSD([subQ0]),TDD([makeQuery(id+"F0.imprint","IMPRINT",EDGE,{"disambiguationData":[TD([[makeQuery(id+"F0.imprint","INTERSECT",VERTEX,{"derivedFrom":[subQ0,sQuery(id+"F0.wireOp",EDGE,"E10")]}),-1.0]])],"derivedFrom":subQ0})])]})])],"derivedFrom":makeQuery(id+"F5.opSweep","SWEPT_EDGE",EDGE,{"disambiguationData":[OSD([subQ3,subQ0,subQ1,subQ2])]})});}
            var Q12;
            {var subQ0=sQuery(id+"F0.wireOp",EDGE,"E2");var subQ1=sQuery(id+"F0.wireOp",EDGE,"E26.MirrorCS");Q12=makeQuery(id+"F5.boolean.opBoolean","SPLIT",EDGE,{"disambiguationData":[TD([makeQuery(id+"F3.opExtrude","CAP_FACE",FACE,{"disambiguationData":[OSD([sQuery(id+"F2.wireOp",EDGE,"E29")])],"isStart":true})])],"derivedFrom":makeQuery(id+"F1.opExtrude","SWEPT_EDGE",EDGE,{"disambiguationData":[OSD([subQ0,subQ1])]})});}
            var Q13;
            {var subQ0=sQuery(id+"F0.wireOp",EDGE,"E2");var subQ1=sQuery(id+"F4.wireOp",EDGE,"E43.MirrorCS");var subQ2=sQuery(id+"F0.wireOp",EDGE,"E0");Q13=makeQuery(id+"F5.boolean.opBoolean","COPY",EDGE,{"disambiguationData":[topologyDisambiguationEdgeConnected([makeQuery(id+"F1.opExtrude","SWEPT_FACE",FACE,{"disambiguationData":[OSD([subQ0]),TDD([makeQuery(id+"F0.imprint","IMPRINT",EDGE,{"disambiguationData":[TD([[makeQuery(id+"F0.imprint","INTERSECT",VERTEX,{"derivedFrom":[subQ0,sQuery(id+"F0.wireOp",EDGE,"E25.MirrorCS")]}),1.0]])],"derivedFrom":subQ0})])]})])],"derivedFrom":makeQuery(id+"F5.opSweep","SWEPT_EDGE",EDGE,{"disambiguationData":[OSD([subQ2,subQ0,sQuery(id+"F0.wireOp",EDGE,"E27.MirrorCS"),subQ1])]})});}
            var Q14;
            {var subQ0=sQuery(id+"F0.wireOp",EDGE,"E25.MirrorCS");var subQ1=sQuery(id+"F0.wireOp",EDGE,"E2");Q14=makeQuery(id+"F5.boolean.opBoolean","SPLIT",EDGE,{"disambiguationData":[TD([makeQuery(id+"F3.opExtrude","CAP_FACE",FACE,{"disambiguationData":[OSD([sQuery(id+"F2.wireOp",EDGE,"E29")])],"isStart":true})])],"derivedFrom":makeQuery(id+"F1.opExtrude","SWEPT_EDGE",EDGE,{"disambiguationData":[OSD([subQ1,subQ0])]})});}
            var Q15;
            {var subQ0=sQuery(id+"F0.wireOp",EDGE,"E2");var subQ1=sQuery(id+"F0.wireOp",EDGE,"E24.MirrorCS");Q15=makeQuery(id+"F5.boolean.opBoolean","SPLIT",EDGE,{"disambiguationData":[TD([makeQuery(id+"F3.opExtrude","CAP_FACE",FACE,{"disambiguationData":[OSD([sQuery(id+"F2.wireOp",EDGE,"E29")])],"isStart":true})])],"derivedFrom":makeQuery(id+"F1.opExtrude","SWEPT_EDGE",EDGE,{"disambiguationData":[OSD([subQ0,subQ1])]})});}
            var Q16;
            {var subQ0=sQuery(id+"F0.wireOp",EDGE,"E2");var subQ1=sQuery(id+"F4.wireOp",EDGE,"E43.MirrorCS");var subQ2=sQuery(id+"F0.wireOp",EDGE,"E0");Q16=makeQuery(id+"F5.boolean.opBoolean","COPY",EDGE,{"disambiguationData":[topologyDisambiguationEdgeConnected([makeQuery(id+"F1.opExtrude","SWEPT_FACE",FACE,{"disambiguationData":[OSD([subQ0]),TDD([makeQuery(id+"F0.imprint","IMPRINT",EDGE,{"disambiguationData":[TD([[makeQuery(id+"F0.imprint","INTERSECT",VERTEX,{"derivedFrom":[subQ0,sQuery(id+"F0.wireOp",EDGE,"E23.MirrorCS")]}),1.0]])],"derivedFrom":subQ0})])]})])],"derivedFrom":makeQuery(id+"F5.opSweep","SWEPT_EDGE",EDGE,{"disambiguationData":[OSD([subQ2,subQ0,sQuery(id+"F0.wireOp",EDGE,"E27.MirrorCS"),subQ1])]})});}
            var Q17;
            {var subQ0=sQuery(id+"F0.wireOp",EDGE,"E23.MirrorCS");var subQ1=sQuery(id+"F0.wireOp",EDGE,"E2");Q17=makeQuery(id+"F5.boolean.opBoolean","SPLIT",EDGE,{"disambiguationData":[TD([makeQuery(id+"F3.opExtrude","CAP_FACE",FACE,{"disambiguationData":[OSD([sQuery(id+"F2.wireOp",EDGE,"E29")])],"isStart":true})])],"derivedFrom":makeQuery(id+"F1.opExtrude","SWEPT_EDGE",EDGE,{"disambiguationData":[OSD([subQ1,subQ0])]})});}
            var Q18;
            {var subQ0=sQuery(id+"F0.wireOp",EDGE,"E2");var subQ1=sQuery(id+"F0.wireOp",EDGE,"E22.MirrorCS");Q18=makeQuery(id+"F5.boolean.opBoolean","SPLIT",EDGE,{"disambiguationData":[TD([makeQuery(id+"F3.opExtrude","CAP_FACE",FACE,{"disambiguationData":[OSD([sQuery(id+"F2.wireOp",EDGE,"E29")])],"isStart":true})])],"derivedFrom":makeQuery(id+"F1.opExtrude","SWEPT_EDGE",EDGE,{"disambiguationData":[OSD([subQ0,subQ1])]})});}
            var Q19;
            {var subQ0=sQuery(id+"F0.wireOp",EDGE,"E2");var subQ1=sQuery(id+"F4.wireOp",EDGE,"E43.MirrorCS");var subQ2=sQuery(id+"F0.wireOp",EDGE,"E0");Q19=makeQuery(id+"F5.boolean.opBoolean","COPY",EDGE,{"disambiguationData":[topologyDisambiguationEdgeConnected([makeQuery(id+"F1.opExtrude","SWEPT_FACE",FACE,{"disambiguationData":[OSD([subQ0]),TDD([makeQuery(id+"F0.imprint","IMPRINT",EDGE,{"disambiguationData":[TD([[makeQuery(id+"F0.imprint","INTERSECT",VERTEX,{"derivedFrom":[subQ0,sQuery(id+"F0.wireOp",EDGE,"E21.MirrorCS")]}),1.0]])],"derivedFrom":subQ0})])]})])],"derivedFrom":makeQuery(id+"F5.opSweep","SWEPT_EDGE",EDGE,{"disambiguationData":[OSD([subQ2,subQ0,sQuery(id+"F0.wireOp",EDGE,"E27.MirrorCS"),subQ1])]})});}
            var Q20;
            {var subQ0=sQuery(id+"F0.wireOp",EDGE,"E21.MirrorCS");var subQ1=sQuery(id+"F0.wireOp",EDGE,"E2");Q20=makeQuery(id+"F5.boolean.opBoolean","SPLIT",EDGE,{"disambiguationData":[TD([makeQuery(id+"F3.opExtrude","CAP_FACE",FACE,{"disambiguationData":[OSD([sQuery(id+"F2.wireOp",EDGE,"E29")])],"isStart":true})])],"derivedFrom":makeQuery(id+"F1.opExtrude","SWEPT_EDGE",EDGE,{"disambiguationData":[OSD([subQ1,subQ0])]})});}
            var Q21;
            {var subQ0=sQuery(id+"F0.wireOp",EDGE,"E2");var subQ1=sQuery(id+"F0.wireOp",EDGE,"E20.MirrorCS");Q21=makeQuery(id+"F5.boolean.opBoolean","SPLIT",EDGE,{"disambiguationData":[TD([makeQuery(id+"F3.opExtrude","CAP_FACE",FACE,{"disambiguationData":[OSD([sQuery(id+"F2.wireOp",EDGE,"E29")])],"isStart":true})])],"derivedFrom":makeQuery(id+"F1.opExtrude","SWEPT_EDGE",EDGE,{"disambiguationData":[OSD([subQ0,subQ1])]})});}
            var Q22;
            {var subQ0=sQuery(id+"F0.wireOp",EDGE,"E2");var subQ1=sQuery(id+"F4.wireOp",EDGE,"E43.MirrorCS");var subQ2=sQuery(id+"F0.wireOp",EDGE,"E0");Q22=makeQuery(id+"F5.boolean.opBoolean","COPY",EDGE,{"disambiguationData":[topologyDisambiguationEdgeConnected([makeQuery(id+"F1.opExtrude","SWEPT_FACE",FACE,{"disambiguationData":[OSD([subQ0]),TDD([makeQuery(id+"F0.imprint","IMPRINT",EDGE,{"disambiguationData":[TD([[makeQuery(id+"F0.imprint","INTERSECT",VERTEX,{"derivedFrom":[subQ0,sQuery(id+"F0.wireOp",EDGE,"E19.MirrorCS")]}),1.0]])],"derivedFrom":subQ0})])]})])],"derivedFrom":makeQuery(id+"F5.opSweep","SWEPT_EDGE",EDGE,{"disambiguationData":[OSD([subQ2,subQ0,sQuery(id+"F0.wireOp",EDGE,"E27.MirrorCS"),subQ1])]})});}
            var Q23;
            {var subQ0=sQuery(id+"F0.wireOp",EDGE,"E19.MirrorCS");var subQ1=sQuery(id+"F0.wireOp",EDGE,"E2");Q23=makeQuery(id+"F5.boolean.opBoolean","SPLIT",EDGE,{"disambiguationData":[TD([makeQuery(id+"F3.opExtrude","CAP_FACE",FACE,{"disambiguationData":[OSD([sQuery(id+"F2.wireOp",EDGE,"E29")])],"isStart":true})])],"derivedFrom":makeQuery(id+"F1.opExtrude","SWEPT_EDGE",EDGE,{"disambiguationData":[OSD([subQ1,subQ0])]})});}
            var Q24;
            {var subQ0=sQuery(id+"F0.wireOp",EDGE,"E2");var subQ1=sQuery(id+"F0.wireOp",EDGE,"E18.MirrorCS");Q24=makeQuery(id+"F5.boolean.opBoolean","SPLIT",EDGE,{"disambiguationData":[TD([makeQuery(id+"F3.opExtrude","CAP_FACE",FACE,{"disambiguationData":[OSD([sQuery(id+"F2.wireOp",EDGE,"E29")])],"isStart":true})])],"derivedFrom":makeQuery(id+"F1.opExtrude","SWEPT_EDGE",EDGE,{"disambiguationData":[OSD([subQ0,subQ1])]})});}
            var Q25;
            {var subQ0=sQuery(id+"F0.wireOp",EDGE,"E2");var subQ1=sQuery(id+"F4.wireOp",EDGE,"E43.MirrorCS");var subQ2=sQuery(id+"F0.wireOp",EDGE,"E0");Q25=makeQuery(id+"F5.boolean.opBoolean","COPY",EDGE,{"disambiguationData":[topologyDisambiguationEdgeConnected([makeQuery(id+"F1.opExtrude","SWEPT_FACE",FACE,{"disambiguationData":[OSD([subQ0]),TDD([makeQuery(id+"F0.imprint","IMPRINT",EDGE,{"disambiguationData":[TD([[makeQuery(id+"F0.imprint","INTERSECT",VERTEX,{"derivedFrom":[subQ0,sQuery(id+"F0.wireOp",EDGE,"E17.MirrorCS")]}),1.0]])],"derivedFrom":subQ0})])]})])],"derivedFrom":makeQuery(id+"F5.opSweep","SWEPT_EDGE",EDGE,{"disambiguationData":[OSD([subQ2,subQ0,sQuery(id+"F0.wireOp",EDGE,"E27.MirrorCS"),subQ1])]})});}
            var Q26;
            {var subQ0=sQuery(id+"F0.wireOp",EDGE,"E17.MirrorCS");var subQ1=sQuery(id+"F0.wireOp",EDGE,"E2");Q26=makeQuery(id+"F5.boolean.opBoolean","SPLIT",EDGE,{"disambiguationData":[TD([makeQuery(id+"F3.opExtrude","CAP_FACE",FACE,{"disambiguationData":[OSD([sQuery(id+"F2.wireOp",EDGE,"E29")])],"isStart":true})])],"derivedFrom":makeQuery(id+"F1.opExtrude","SWEPT_EDGE",EDGE,{"disambiguationData":[OSD([subQ1,subQ0])]})});}
            var Q27;
            {var subQ0=sQuery(id+"F0.wireOp",EDGE,"E2");var subQ1=sQuery(id+"F0.wireOp",EDGE,"E28");Q27=makeQuery(id+"F5.boolean.opBoolean","SPLIT",EDGE,{"disambiguationData":[TD([makeQuery(id+"F3.opExtrude","CAP_FACE",FACE,{"disambiguationData":[OSD([sQuery(id+"F2.wireOp",EDGE,"E29")])],"isStart":true})])],"derivedFrom":makeQuery(id+"F1.opExtrude","SWEPT_EDGE",EDGE,{"disambiguationData":[OSD([subQ0,subQ1])]})});}
            var Q28;
            {var subQ0=sQuery(id+"F0.wireOp",EDGE,"E2");var subQ1=sQuery(id+"F4.wireOp",EDGE,"E43.MirrorCS");var subQ2=sQuery(id+"F0.wireOp",EDGE,"E0");Q28=makeQuery(id+"F5.boolean.opBoolean","COPY",EDGE,{"disambiguationData":[topologyDisambiguationEdgeConnected([makeQuery(id+"F1.opExtrude","SWEPT_FACE",FACE,{"disambiguationData":[OSD([subQ0]),TDD([makeQuery(id+"F0.imprint","IMPRINT",EDGE,{"disambiguationData":[TD([[makeQuery(id+"F0.imprint","INTERSECT",VERTEX,{"derivedFrom":[subQ0,sQuery(id+"F0.wireOp",EDGE,"E15.MirrorCS")]}),1.0]])],"derivedFrom":subQ0})])]})])],"derivedFrom":makeQuery(id+"F5.opSweep","SWEPT_EDGE",EDGE,{"disambiguationData":[OSD([subQ2,subQ0,sQuery(id+"F0.wireOp",EDGE,"E27.MirrorCS"),subQ1])]})});}
            var Q29;
            {var subQ0=sQuery(id+"F0.wireOp",EDGE,"E15.MirrorCS");var subQ1=sQuery(id+"F0.wireOp",EDGE,"E2");Q29=makeQuery(id+"F5.boolean.opBoolean","SPLIT",EDGE,{"disambiguationData":[TD([makeQuery(id+"F3.opExtrude","CAP_FACE",FACE,{"disambiguationData":[OSD([sQuery(id+"F2.wireOp",EDGE,"E29")])],"isStart":true})])],"derivedFrom":makeQuery(id+"F1.opExtrude","SWEPT_EDGE",EDGE,{"disambiguationData":[OSD([subQ1,subQ0])]})});}
            var Q30;
            {var subQ0=sQuery(id+"F0.wireOp",EDGE,"E2");var subQ1=sQuery(id+"F0.wireOp",EDGE,"E14.MirrorCS");Q30=makeQuery(id+"F5.boolean.opBoolean","SPLIT",EDGE,{"disambiguationData":[TD([makeQuery(id+"F3.opExtrude","CAP_FACE",FACE,{"disambiguationData":[OSD([sQuery(id+"F2.wireOp",EDGE,"E29")])],"isStart":true})])],"derivedFrom":makeQuery(id+"F1.opExtrude","SWEPT_EDGE",EDGE,{"disambiguationData":[OSD([subQ0,subQ1])]})});}
            var Q31;
            {var subQ0=sQuery(id+"F0.wireOp",EDGE,"E2");var subQ1=sQuery(id+"F4.wireOp",EDGE,"E43.MirrorCS");var subQ2=sQuery(id+"F0.wireOp",EDGE,"E0");Q31=makeQuery(id+"F5.boolean.opBoolean","COPY",EDGE,{"disambiguationData":[topologyDisambiguationEdgeConnected([makeQuery(id+"F1.opExtrude","SWEPT_FACE",FACE,{"disambiguationData":[OSD([subQ0]),TDD([makeQuery(id+"F0.imprint","IMPRINT",EDGE,{"disambiguationData":[TD([[makeQuery(id+"F0.imprint","INTERSECT",VERTEX,{"derivedFrom":[subQ0,sQuery(id+"F0.wireOp",EDGE,"E13.MirrorCS")]}),1.0]])],"derivedFrom":subQ0})])]})])],"derivedFrom":makeQuery(id+"F5.opSweep","SWEPT_EDGE",EDGE,{"disambiguationData":[OSD([subQ2,subQ0,sQuery(id+"F0.wireOp",EDGE,"E27.MirrorCS"),subQ1])]})});}
            var Q32;
            {var subQ0=sQuery(id+"F0.wireOp",EDGE,"E13.MirrorCS");var subQ1=sQuery(id+"F0.wireOp",EDGE,"E2");Q32=makeQuery(id+"F5.boolean.opBoolean","SPLIT",EDGE,{"disambiguationData":[TD([makeQuery(id+"F3.opExtrude","CAP_FACE",FACE,{"disambiguationData":[OSD([sQuery(id+"F2.wireOp",EDGE,"E29")])],"isStart":true})])],"derivedFrom":makeQuery(id+"F1.opExtrude","SWEPT_EDGE",EDGE,{"disambiguationData":[OSD([subQ1,subQ0])]})});}
            var Q33;
            {var subQ0=sQuery(id+"F0.wireOp",EDGE,"E2");var subQ1=sQuery(id+"F0.wireOp",EDGE,"E12.MirrorCS");Q33=makeQuery(id+"F5.boolean.opBoolean","SPLIT",EDGE,{"disambiguationData":[TD([makeQuery(id+"F3.opExtrude","CAP_FACE",FACE,{"disambiguationData":[OSD([sQuery(id+"F2.wireOp",EDGE,"E29")])],"isStart":true})])],"derivedFrom":makeQuery(id+"F1.opExtrude","SWEPT_EDGE",EDGE,{"disambiguationData":[OSD([subQ0,subQ1])]})});}
            var Q34;
            {var subQ0=sQuery(id+"F0.wireOp",EDGE,"E2");var subQ1=sQuery(id+"F4.wireOp",EDGE,"E43.MirrorCS");var subQ2=sQuery(id+"F0.wireOp",EDGE,"E0");Q34=makeQuery(id+"F5.boolean.opBoolean","COPY",EDGE,{"disambiguationData":[topologyDisambiguationEdgeConnected([makeQuery(id+"F1.opExtrude","SWEPT_FACE",FACE,{"disambiguationData":[OSD([subQ0]),TDD([makeQuery(id+"F0.imprint","IMPRINT",EDGE,{"disambiguationData":[TD([[makeQuery(id+"F0.imprint","INTERSECT",VERTEX,{"derivedFrom":[subQ0,sQuery(id+"F0.wireOp",EDGE,"E11.MirrorCS")]}),1.0]])],"derivedFrom":subQ0})])]})])],"derivedFrom":makeQuery(id+"F5.opSweep","SWEPT_EDGE",EDGE,{"disambiguationData":[OSD([subQ2,subQ0,sQuery(id+"F0.wireOp",EDGE,"E27.MirrorCS"),subQ1])]})});}
            var Q35;
            {var subQ0=sQuery(id+"F0.wireOp",EDGE,"E11.MirrorCS");var subQ1=sQuery(id+"F0.wireOp",EDGE,"E2");Q35=makeQuery(id+"F5.boolean.opBoolean","SPLIT",EDGE,{"disambiguationData":[TD([makeQuery(id+"F3.opExtrude","CAP_FACE",FACE,{"disambiguationData":[OSD([sQuery(id+"F2.wireOp",EDGE,"E29")])],"isStart":true})])],"derivedFrom":makeQuery(id+"F1.opExtrude","SWEPT_EDGE",EDGE,{"disambiguationData":[OSD([subQ1,subQ0])]})});}
            fillet(context, id + "F7", {"entities" : qUnion([Q0, Q1, Q2, Q3, Q4, Q5, Q6, Q7, Q8, Q9, Q10, Q11, Q12, Q13, Q14, Q15, Q16, Q17, Q18, Q19, Q20, Q21, Q22, Q23, Q24, Q25, Q26, Q27, Q28, Q29, Q30, Q31, Q32, Q33, Q34, Q35]), "radius" : 1 * mm, "tangentPropagation" : true, "allowEdgeOverflow" : false});
        }
        {
            var Q0;
            Q0=makeQuery(id+"F3.opExtrude","CAP_EDGE",EDGE,{"disambiguationData":[OSD([sQuery(id+"F2.wireOp",EDGE,"E29")])],"isStart":false});
            var Q1;
            Q1=makeQuery(id+"F3.opExtrude","CAP_EDGE",EDGE,{"disambiguationData":[OSD([sQuery(id+"F2.wireOp",EDGE,"E29")])],"isStart":true});
            fillet(context, id + "F8", {"entities" : qUnion([Q0, Q1]), "radius" : 3 * mm, "tangentPropagation" : true, "allowEdgeOverflow" : false});
        }
        {
            var Q0;
            {var subQ0=sQuery(id+"F0.wireOp",EDGE,"E27.MirrorCS");var subQ1=sQuery(id+"F0.wireOp",EDGE,"E1");var subQ2=makeQuery(id+"F1.opExtrude","SWEPT_EDGE",EDGE,{"disambiguationData":[OSD([subQ1,subQ0])]});var subQ3=sQuery(id+"F0.wireOp",EDGE,"E0");var subQ4=makeQuery(id+"F1.opExtrude","CAP_EDGE",EDGE,{"disambiguationData":[OSD([subQ3])],"isStart":true});Q0=makeQuery(id+"F8.opFillet","BLEND_EDGE",EDGE,{"disambiguationData":[OD(5.0)],"blendedFrom":[makeQuery(id+"F3.opExtrude","CAP_EDGE",EDGE,{"disambiguationData":[OSD([sQuery(id+"F2.wireOp",EDGE,"E29")])],"isStart":true}),makeQuery(id+"F5.boolean.opBoolean","MERGE",FACE,{"derivedFrom":[makeQuery(id+"F1.opExtrude","SWEPT_FACE",FACE,{"disambiguationData":[OSD([subQ1]),TDD([makeQuery(id+"F0.imprint","IMPRINT",EDGE,{"disambiguationData":[TD([[makeQuery(id+"F0.imprint","INTERSECT",VERTEX,{"derivedFrom":[subQ1,sQuery(id+"F0.wireOp",EDGE,"E14.MirrorCS")]}),1.0]])],"derivedFrom":subQ1})])]}),makeQuery(id+"F1.opExtrude","SWEPT_FACE",FACE,{"disambiguationData":[OSD([subQ1]),TDD([makeQuery(id+"F0.imprint","IMPRINT",EDGE,{"disambiguationData":[TD([[makeQuery(id+"F0.imprint","INTERSECT",VERTEX,{"derivedFrom":[subQ1,sQuery(id+"F0.wireOp",EDGE,"E12.MirrorCS")]}),1.0]])],"derivedFrom":subQ1})])]}),makeQuery(id+"F1.opExtrude","SWEPT_FACE",FACE,{"disambiguationData":[OSD([subQ1]),TDD([makeQuery(id+"F0.imprint","IMPRINT",EDGE,{"disambiguationData":[TD([[makeQuery(id+"F0.imprint","INTERSECT",VERTEX,{"derivedFrom":[subQ1,sQuery(id+"F0.wireOp",EDGE,"E3")]}),1.0]])],"derivedFrom":subQ1})])]}),makeQuery(id+"F1.opExtrude","SWEPT_FACE",FACE,{"disambiguationData":[OSD([subQ1]),TDD([makeQuery(id+"F0.imprint","IMPRINT",EDGE,{"disambiguationData":[TD([[makeQuery(id+"F0.imprint","INTERSECT",VERTEX,{"derivedFrom":[subQ1,sQuery(id+"F0.wireOp",EDGE,"E8")]}),1.0]])],"derivedFrom":subQ1})])]}),makeQuery(id+"F1.opExtrude","SWEPT_FACE",FACE,{"disambiguationData":[OSD([subQ1]),TDD([makeQuery(id+"F0.imprint","IMPRINT",EDGE,{"disambiguationData":[TD([[makeQuery(id+"F0.imprint","INTERSECT",VERTEX,{"derivedFrom":[subQ1,sQuery(id+"F0.wireOp",EDGE,"E6")]}),1.0]])],"derivedFrom":subQ1})])]}),makeQuery(id+"F1.opExtrude","SWEPT_FACE",FACE,{"disambiguationData":[OSD([subQ1]),TDD([makeQuery(id+"F0.imprint","IMPRINT",EDGE,{"disambiguationData":[TD([[makeQuery(id+"F0.imprint","INTERSECT",VERTEX,{"derivedFrom":[subQ1,sQuery(id+"F0.wireOp",EDGE,"E5")]}),-1.0]])],"derivedFrom":subQ1})])]}),makeQuery(id+"F1.opExtrude","SWEPT_FACE",FACE,{"disambiguationData":[OSD([subQ1]),TDD([makeQuery(id+"F0.imprint","IMPRINT",EDGE,{"disambiguationData":[TD([[makeQuery(id+"F0.imprint","INTERSECT",VERTEX,{"derivedFrom":[subQ1,sQuery(id+"F0.wireOp",EDGE,"E26.MirrorCS")]}),1.0]])],"derivedFrom":subQ1})])]}),makeQuery(id+"F1.opExtrude","SWEPT_FACE",FACE,{"disambiguationData":[OSD([subQ1]),TDD([makeQuery(id+"F0.imprint","IMPRINT",EDGE,{"disambiguationData":[TD([[makeQuery(id+"F0.imprint","INTERSECT",VERTEX,{"derivedFrom":[subQ1,sQuery(id+"F0.wireOp",EDGE,"E24.MirrorCS")]}),1.0]])],"derivedFrom":subQ1})])]}),makeQuery(id+"F1.opExtrude","SWEPT_FACE",FACE,{"disambiguationData":[OSD([subQ1]),TDD([makeQuery(id+"F0.imprint","IMPRINT",EDGE,{"disambiguationData":[TD([[makeQuery(id+"F0.imprint","INTERSECT",VERTEX,{"derivedFrom":[subQ1,sQuery(id+"F0.wireOp",EDGE,"E22.MirrorCS")]}),1.0]])],"derivedFrom":subQ1})])]}),makeQuery(id+"F1.opExtrude","SWEPT_FACE",FACE,{"disambiguationData":[OSD([subQ1]),TDD([makeQuery(id+"F0.imprint","IMPRINT",EDGE,{"disambiguationData":[TD([[makeQuery(id+"F0.imprint","INTERSECT",VERTEX,{"derivedFrom":[subQ1,sQuery(id+"F0.wireOp",EDGE,"E20.MirrorCS")]}),1.0]])],"derivedFrom":subQ1})])]}),makeQuery(id+"F1.opExtrude","SWEPT_FACE",FACE,{"disambiguationData":[OSD([subQ1]),TDD([makeQuery(id+"F0.imprint","IMPRINT",EDGE,{"disambiguationData":[TD([[makeQuery(id+"F0.imprint","INTERSECT",VERTEX,{"derivedFrom":[subQ1,sQuery(id+"F0.wireOp",EDGE,"E18.MirrorCS")]}),1.0]])],"derivedFrom":subQ1})])]}),makeQuery(id+"F1.opExtrude","SWEPT_FACE",FACE,{"disambiguationData":[OSD([subQ1]),TDD([makeQuery(id+"F0.imprint","IMPRINT",EDGE,{"disambiguationData":[TD([[makeQuery(id+"F0.imprint","INTERSECT",VERTEX,{"derivedFrom":[subQ1,sQuery(id+"F0.wireOp",EDGE,"E17.MirrorCS")]}),-1.0]])],"derivedFrom":subQ1})])]})],"fromTools":[makeQuery(id+"F5.opSweep","SWEPT_FACE",FACE,{"disambiguationData":[OSD([subQ3,subQ1,subQ0]),TDD([subQ4,makeQuery(id+"F4.imprint","IMPRINT",EDGE,{"disambiguationData":[TD([[makeQuery(id+"F4.imprint","INTERSECT",VERTEX,{"derivedFrom":[subQ2,sQuery(id+"F4.wireOp",EDGE,"E30")]}),1.0]])],"derivedFrom":subQ2})])]}),makeQuery(id+"F5.opSweep","SWEPT_FACE",FACE,{"disambiguationData":[OSD([subQ3,subQ1,subQ0]),TDD([subQ4,makeQuery(id+"F4.imprint","IMPRINT",EDGE,{"disambiguationData":[TD([[makeQuery(id+"F4.imprint","INTERSECT",VERTEX,{"derivedFrom":[subQ2,sQuery(id+"F4.wireOp",EDGE,"E32.MirrorCS")]}),1.0]])],"derivedFrom":subQ2})])]}),makeQuery(id+"F5.opSweep","SWEPT_FACE",FACE,{"disambiguationData":[OSD([subQ3,subQ1,subQ0]),TDD([subQ4,makeQuery(id+"F4.imprint","IMPRINT",EDGE,{"disambiguationData":[TD([[makeQuery(id+"F4.imprint","INTERSECT",VERTEX,{"derivedFrom":[subQ2,sQuery(id+"F4.wireOp",EDGE,"E34.MirrorCS")]}),1.0]])],"derivedFrom":subQ2})])]}),makeQuery(id+"F5.opSweep","SWEPT_FACE",FACE,{"disambiguationData":[OSD([subQ3,subQ1,subQ0]),TDD([subQ4,makeQuery(id+"F4.imprint","IMPRINT",EDGE,{"disambiguationData":[TD([[makeQuery(id+"F4.imprint","INTERSECT",VERTEX,{"derivedFrom":[subQ2,sQuery(id+"F4.wireOp",EDGE,"E36.MirrorCS")]}),1.0]])],"derivedFrom":subQ2})])]}),makeQuery(id+"F5.opSweep","SWEPT_FACE",FACE,{"disambiguationData":[OSD([subQ3,subQ1,subQ0]),TDD([subQ4,makeQuery(id+"F4.imprint","IMPRINT",EDGE,{"disambiguationData":[TD([[makeQuery(id+"F4.imprint","INTERSECT",VERTEX,{"derivedFrom":[subQ2,sQuery(id+"F4.wireOp",EDGE,"E38.MirrorCS")]}),1.0]])],"derivedFrom":subQ2})])]}),makeQuery(id+"F5.opSweep","SWEPT_FACE",FACE,{"disambiguationData":[OSD([subQ3,subQ1,subQ0]),TDD([subQ4,makeQuery(id+"F4.imprint","IMPRINT",EDGE,{"disambiguationData":[TD([[makeQuery(id+"F4.imprint","INTERSECT",VERTEX,{"derivedFrom":[subQ2,sQuery(id+"F4.wireOp",EDGE,"E40.MirrorCS")]}),1.0]])],"derivedFrom":subQ2})])]}),makeQuery(id+"F5.opSweep","SWEPT_FACE",FACE,{"disambiguationData":[OSD([subQ3,subQ1,subQ0]),TDD([subQ4,makeQuery(id+"F4.imprint","IMPRINT",EDGE,{"disambiguationData":[TD([[makeQuery(id+"F4.imprint","INTERSECT",VERTEX,{"derivedFrom":[subQ2,sQuery(id+"F4.wireOp",EDGE,"E42.MirrorCS")]}),1.0]])],"derivedFrom":subQ2})])]})]})],"blendedInto":[makeQuery(id+"F5.boolean.opBoolean","MERGE",FACE,{"derivedFrom":[makeQuery(id+"F1.opExtrude","SWEPT_FACE",FACE,{"disambiguationData":[OSD([subQ1]),TDD([makeQuery(id+"F0.imprint","IMPRINT",EDGE,{"disambiguationData":[TD([[makeQuery(id+"F0.imprint","INTERSECT",VERTEX,{"derivedFrom":[subQ1,sQuery(id+"F0.wireOp",EDGE,"E14.MirrorCS")]}),1.0]])],"derivedFrom":subQ1})])]}),makeQuery(id+"F1.opExtrude","SWEPT_FACE",FACE,{"disambiguationData":[OSD([subQ1]),TDD([makeQuery(id+"F0.imprint","IMPRINT",EDGE,{"disambiguationData":[TD([[makeQuery(id+"F0.imprint","INTERSECT",VERTEX,{"derivedFrom":[subQ1,sQuery(id+"F0.wireOp",EDGE,"E12.MirrorCS")]}),1.0]])],"derivedFrom":subQ1})])]}),makeQuery(id+"F1.opExtrude","SWEPT_FACE",FACE,{"disambiguationData":[OSD([subQ1]),TDD([makeQuery(id+"F0.imprint","IMPRINT",EDGE,{"disambiguationData":[TD([[makeQuery(id+"F0.imprint","INTERSECT",VERTEX,{"derivedFrom":[subQ1,sQuery(id+"F0.wireOp",EDGE,"E3")]}),1.0]])],"derivedFrom":subQ1})])]}),makeQuery(id+"F1.opExtrude","SWEPT_FACE",FACE,{"disambiguationData":[OSD([subQ1]),TDD([makeQuery(id+"F0.imprint","IMPRINT",EDGE,{"disambiguationData":[TD([[makeQuery(id+"F0.imprint","INTERSECT",VERTEX,{"derivedFrom":[subQ1,sQuery(id+"F0.wireOp",EDGE,"E8")]}),1.0]])],"derivedFrom":subQ1})])]}),makeQuery(id+"F1.opExtrude","SWEPT_FACE",FACE,{"disambiguationData":[OSD([subQ1]),TDD([makeQuery(id+"F0.imprint","IMPRINT",EDGE,{"disambiguationData":[TD([[makeQuery(id+"F0.imprint","INTERSECT",VERTEX,{"derivedFrom":[subQ1,sQuery(id+"F0.wireOp",EDGE,"E6")]}),1.0]])],"derivedFrom":subQ1})])]}),makeQuery(id+"F1.opExtrude","SWEPT_FACE",FACE,{"disambiguationData":[OSD([subQ1]),TDD([makeQuery(id+"F0.imprint","IMPRINT",EDGE,{"disambiguationData":[TD([[makeQuery(id+"F0.imprint","INTERSECT",VERTEX,{"derivedFrom":[subQ1,sQuery(id+"F0.wireOp",EDGE,"E5")]}),-1.0]])],"derivedFrom":subQ1})])]}),makeQuery(id+"F1.opExtrude","SWEPT_FACE",FACE,{"disambiguationData":[OSD([subQ1]),TDD([makeQuery(id+"F0.imprint","IMPRINT",EDGE,{"disambiguationData":[TD([[makeQuery(id+"F0.imprint","INTERSECT",VERTEX,{"derivedFrom":[subQ1,sQuery(id+"F0.wireOp",EDGE,"E26.MirrorCS")]}),1.0]])],"derivedFrom":subQ1})])]}),makeQuery(id+"F1.opExtrude","SWEPT_FACE",FACE,{"disambiguationData":[OSD([subQ1]),TDD([makeQuery(id+"F0.imprint","IMPRINT",EDGE,{"disambiguationData":[TD([[makeQuery(id+"F0.imprint","INTERSECT",VERTEX,{"derivedFrom":[subQ1,sQuery(id+"F0.wireOp",EDGE,"E24.MirrorCS")]}),1.0]])],"derivedFrom":subQ1})])]}),makeQuery(id+"F1.opExtrude","SWEPT_FACE",FACE,{"disambiguationData":[OSD([subQ1]),TDD([makeQuery(id+"F0.imprint","IMPRINT",EDGE,{"disambiguationData":[TD([[makeQuery(id+"F0.imprint","INTERSECT",VERTEX,{"derivedFrom":[subQ1,sQuery(id+"F0.wireOp",EDGE,"E22.MirrorCS")]}),1.0]])],"derivedFrom":subQ1})])]}),makeQuery(id+"F1.opExtrude","SWEPT_FACE",FACE,{"disambiguationData":[OSD([subQ1]),TDD([makeQuery(id+"F0.imprint","IMPRINT",EDGE,{"disambiguationData":[TD([[makeQuery(id+"F0.imprint","INTERSECT",VERTEX,{"derivedFrom":[subQ1,sQuery(id+"F0.wireOp",EDGE,"E20.MirrorCS")]}),1.0]])],"derivedFrom":subQ1})])]}),makeQuery(id+"F1.opExtrude","SWEPT_FACE",FACE,{"disambiguationData":[OSD([subQ1]),TDD([makeQuery(id+"F0.imprint","IMPRINT",EDGE,{"disambiguationData":[TD([[makeQuery(id+"F0.imprint","INTERSECT",VERTEX,{"derivedFrom":[subQ1,sQuery(id+"F0.wireOp",EDGE,"E18.MirrorCS")]}),1.0]])],"derivedFrom":subQ1})])]}),makeQuery(id+"F1.opExtrude","SWEPT_FACE",FACE,{"disambiguationData":[OSD([subQ1]),TDD([makeQuery(id+"F0.imprint","IMPRINT",EDGE,{"disambiguationData":[TD([[makeQuery(id+"F0.imprint","INTERSECT",VERTEX,{"derivedFrom":[subQ1,sQuery(id+"F0.wireOp",EDGE,"E17.MirrorCS")]}),-1.0]])],"derivedFrom":subQ1})])]})],"fromTools":[makeQuery(id+"F5.opSweep","SWEPT_FACE",FACE,{"disambiguationData":[OSD([subQ3,subQ1,subQ0]),TDD([subQ4,makeQuery(id+"F4.imprint","IMPRINT",EDGE,{"disambiguationData":[TD([[makeQuery(id+"F4.imprint","INTERSECT",VERTEX,{"derivedFrom":[subQ2,sQuery(id+"F4.wireOp",EDGE,"E30")]}),1.0]])],"derivedFrom":subQ2})])]}),makeQuery(id+"F5.opSweep","SWEPT_FACE",FACE,{"disambiguationData":[OSD([subQ3,subQ1,subQ0]),TDD([subQ4,makeQuery(id+"F4.imprint","IMPRINT",EDGE,{"disambiguationData":[TD([[makeQuery(id+"F4.imprint","INTERSECT",VERTEX,{"derivedFrom":[subQ2,sQuery(id+"F4.wireOp",EDGE,"E32.MirrorCS")]}),1.0]])],"derivedFrom":subQ2})])]}),makeQuery(id+"F5.opSweep","SWEPT_FACE",FACE,{"disambiguationData":[OSD([subQ3,subQ1,subQ0]),TDD([subQ4,makeQuery(id+"F4.imprint","IMPRINT",EDGE,{"disambiguationData":[TD([[makeQuery(id+"F4.imprint","INTERSECT",VERTEX,{"derivedFrom":[subQ2,sQuery(id+"F4.wireOp",EDGE,"E34.MirrorCS")]}),1.0]])],"derivedFrom":subQ2})])]}),makeQuery(id+"F5.opSweep","SWEPT_FACE",FACE,{"disambiguationData":[OSD([subQ3,subQ1,subQ0]),TDD([subQ4,makeQuery(id+"F4.imprint","IMPRINT",EDGE,{"disambiguationData":[TD([[makeQuery(id+"F4.imprint","INTERSECT",VERTEX,{"derivedFrom":[subQ2,sQuery(id+"F4.wireOp",EDGE,"E36.MirrorCS")]}),1.0]])],"derivedFrom":subQ2})])]}),makeQuery(id+"F5.opSweep","SWEPT_FACE",FACE,{"disambiguationData":[OSD([subQ3,subQ1,subQ0]),TDD([subQ4,makeQuery(id+"F4.imprint","IMPRINT",EDGE,{"disambiguationData":[TD([[makeQuery(id+"F4.imprint","INTERSECT",VERTEX,{"derivedFrom":[subQ2,sQuery(id+"F4.wireOp",EDGE,"E38.MirrorCS")]}),1.0]])],"derivedFrom":subQ2})])]}),makeQuery(id+"F5.opSweep","SWEPT_FACE",FACE,{"disambiguationData":[OSD([subQ3,subQ1,subQ0]),TDD([subQ4,makeQuery(id+"F4.imprint","IMPRINT",EDGE,{"disambiguationData":[TD([[makeQuery(id+"F4.imprint","INTERSECT",VERTEX,{"derivedFrom":[subQ2,sQuery(id+"F4.wireOp",EDGE,"E40.MirrorCS")]}),1.0]])],"derivedFrom":subQ2})])]}),makeQuery(id+"F5.opSweep","SWEPT_FACE",FACE,{"disambiguationData":[OSD([subQ3,subQ1,subQ0]),TDD([subQ4,makeQuery(id+"F4.imprint","IMPRINT",EDGE,{"disambiguationData":[TD([[makeQuery(id+"F4.imprint","INTERSECT",VERTEX,{"derivedFrom":[subQ2,sQuery(id+"F4.wireOp",EDGE,"E42.MirrorCS")]}),1.0]])],"derivedFrom":subQ2})])]})]})]});}
            var Q1;
            Q1=makeQuery(id+"F8.opFillet","BLEND_EDGE",EDGE,{"blendedFrom":[makeQuery(id+"F3.opExtrude","CAP_EDGE",EDGE,{"disambiguationData":[OSD([sQuery(id+"F2.wireOp",EDGE,"E29")])],"isStart":true}),makeQuery(id+"F7.opFillet","BLEND_FACE",FACE,{"disambiguationData":[OSD([sQuery(id+"F0.wireOp",EDGE,"E2"),sQuery(id+"F0.wireOp",EDGE,"E14.MirrorCS")])]})],"blendedInto":[makeQuery(id+"F7.opFillet","BLEND_FACE",FACE,{"disambiguationData":[OSD([sQuery(id+"F0.wireOp",EDGE,"E2"),sQuery(id+"F0.wireOp",EDGE,"E14.MirrorCS")])]})]});
            var Q2;
            {var subQ0=sQuery(id+"F0.wireOp",EDGE,"E13.MirrorCS");var subQ2=sQuery(id+"F2.wireOp",EDGE,"E29");var subQ3=sQuery(id+"F0.wireOp",EDGE,"E2");Q2=makeQuery(id+"F8.opFillet","BLEND_EDGE",EDGE,{"blendedFrom":[makeQuery(id+"F3.opExtrude","CAP_EDGE",EDGE,{"disambiguationData":[OSD([subQ2])],"isStart":true}),makeQuery(id+"F5.boolean.opBoolean","SPLIT",FACE,{"disambiguationData":[TD([makeQuery(id+"F3.opExtrude","CAP_FACE",FACE,{"disambiguationData":[OSD([subQ2])],"isStart":true})])],"derivedFrom":makeQuery(id+"F1.opExtrude","SWEPT_FACE",FACE,{"disambiguationData":[OSD([subQ3]),TDD([makeQuery(id+"F0.imprint","IMPRINT",EDGE,{"disambiguationData":[TD([[makeQuery(id+"F0.imprint","INTERSECT",VERTEX,{"derivedFrom":[subQ3,subQ0]}),1.0]])],"derivedFrom":subQ3})])]})})],"blendedInto":[makeQuery(id+"F5.boolean.opBoolean","SPLIT",FACE,{"disambiguationData":[TD([makeQuery(id+"F3.opExtrude","CAP_FACE",FACE,{"disambiguationData":[OSD([subQ2])],"isStart":true})])],"derivedFrom":makeQuery(id+"F1.opExtrude","SWEPT_FACE",FACE,{"disambiguationData":[OSD([subQ3]),TDD([makeQuery(id+"F0.imprint","IMPRINT",EDGE,{"disambiguationData":[TD([[makeQuery(id+"F0.imprint","INTERSECT",VERTEX,{"derivedFrom":[subQ3,subQ0]}),1.0]])],"derivedFrom":subQ3})])]})})]});}
            var Q3;
            Q3=makeQuery(id+"F8.opFillet","BLEND_EDGE",EDGE,{"blendedFrom":[makeQuery(id+"F3.opExtrude","CAP_EDGE",EDGE,{"disambiguationData":[OSD([sQuery(id+"F2.wireOp",EDGE,"E29")])],"isStart":true}),makeQuery(id+"F7.opFillet","BLEND_FACE",FACE,{"disambiguationData":[OSD([sQuery(id+"F0.wireOp",EDGE,"E2"),sQuery(id+"F0.wireOp",EDGE,"E13.MirrorCS")])]})],"blendedInto":[makeQuery(id+"F7.opFillet","BLEND_FACE",FACE,{"disambiguationData":[OSD([sQuery(id+"F0.wireOp",EDGE,"E2"),sQuery(id+"F0.wireOp",EDGE,"E13.MirrorCS")])]})]});
            var Q4;
            Q4=makeQuery(id+"F8.opFillet","BLEND_EDGE",EDGE,{"blendedFrom":[makeQuery(id+"F3.opExtrude","CAP_EDGE",EDGE,{"disambiguationData":[OSD([sQuery(id+"F2.wireOp",EDGE,"E29")])],"isStart":true}),makeQuery(id+"F7.opFillet","BLEND_FACE",FACE,{"disambiguationData":[OSD([sQuery(id+"F0.wireOp",EDGE,"E2"),sQuery(id+"F0.wireOp",EDGE,"E15.MirrorCS")])]})],"blendedInto":[makeQuery(id+"F7.opFillet","BLEND_FACE",FACE,{"disambiguationData":[OSD([sQuery(id+"F0.wireOp",EDGE,"E2"),sQuery(id+"F0.wireOp",EDGE,"E15.MirrorCS")])]})]});
            var Q5;
            {var subQ0=sQuery(id+"F0.wireOp",EDGE,"E15.MirrorCS");var subQ2=sQuery(id+"F2.wireOp",EDGE,"E29");var subQ3=sQuery(id+"F0.wireOp",EDGE,"E2");Q5=makeQuery(id+"F8.opFillet","BLEND_EDGE",EDGE,{"blendedFrom":[makeQuery(id+"F3.opExtrude","CAP_EDGE",EDGE,{"disambiguationData":[OSD([subQ2])],"isStart":true}),makeQuery(id+"F5.boolean.opBoolean","SPLIT",FACE,{"disambiguationData":[TD([makeQuery(id+"F3.opExtrude","CAP_FACE",FACE,{"disambiguationData":[OSD([subQ2])],"isStart":true})])],"derivedFrom":makeQuery(id+"F1.opExtrude","SWEPT_FACE",FACE,{"disambiguationData":[OSD([subQ3]),TDD([makeQuery(id+"F0.imprint","IMPRINT",EDGE,{"disambiguationData":[TD([[makeQuery(id+"F0.imprint","INTERSECT",VERTEX,{"derivedFrom":[subQ3,subQ0]}),1.0]])],"derivedFrom":subQ3})])]})})],"blendedInto":[makeQuery(id+"F5.boolean.opBoolean","SPLIT",FACE,{"disambiguationData":[TD([makeQuery(id+"F3.opExtrude","CAP_FACE",FACE,{"disambiguationData":[OSD([subQ2])],"isStart":true})])],"derivedFrom":makeQuery(id+"F1.opExtrude","SWEPT_FACE",FACE,{"disambiguationData":[OSD([subQ3]),TDD([makeQuery(id+"F0.imprint","IMPRINT",EDGE,{"disambiguationData":[TD([[makeQuery(id+"F0.imprint","INTERSECT",VERTEX,{"derivedFrom":[subQ3,subQ0]}),1.0]])],"derivedFrom":subQ3})])]})})]});}
            var Q6;
            {var subQ0=sQuery(id+"F0.wireOp",EDGE,"E27.MirrorCS");var subQ1=sQuery(id+"F0.wireOp",EDGE,"E1");var subQ2=makeQuery(id+"F1.opExtrude","SWEPT_EDGE",EDGE,{"disambiguationData":[OSD([subQ1,subQ0])]});var subQ3=sQuery(id+"F0.wireOp",EDGE,"E0");var subQ4=makeQuery(id+"F1.opExtrude","CAP_EDGE",EDGE,{"disambiguationData":[OSD([subQ3])],"isStart":true});Q6=makeQuery(id+"F8.opFillet","BLEND_EDGE",EDGE,{"disambiguationData":[OD(4.0)],"blendedFrom":[makeQuery(id+"F3.opExtrude","CAP_EDGE",EDGE,{"disambiguationData":[OSD([sQuery(id+"F2.wireOp",EDGE,"E29")])],"isStart":true}),makeQuery(id+"F5.boolean.opBoolean","MERGE",FACE,{"derivedFrom":[makeQuery(id+"F1.opExtrude","SWEPT_FACE",FACE,{"disambiguationData":[OSD([subQ1]),TDD([makeQuery(id+"F0.imprint","IMPRINT",EDGE,{"disambiguationData":[TD([[makeQuery(id+"F0.imprint","INTERSECT",VERTEX,{"derivedFrom":[subQ1,sQuery(id+"F0.wireOp",EDGE,"E14.MirrorCS")]}),1.0]])],"derivedFrom":subQ1})])]}),makeQuery(id+"F1.opExtrude","SWEPT_FACE",FACE,{"disambiguationData":[OSD([subQ1]),TDD([makeQuery(id+"F0.imprint","IMPRINT",EDGE,{"disambiguationData":[TD([[makeQuery(id+"F0.imprint","INTERSECT",VERTEX,{"derivedFrom":[subQ1,sQuery(id+"F0.wireOp",EDGE,"E12.MirrorCS")]}),1.0]])],"derivedFrom":subQ1})])]}),makeQuery(id+"F1.opExtrude","SWEPT_FACE",FACE,{"disambiguationData":[OSD([subQ1]),TDD([makeQuery(id+"F0.imprint","IMPRINT",EDGE,{"disambiguationData":[TD([[makeQuery(id+"F0.imprint","INTERSECT",VERTEX,{"derivedFrom":[subQ1,sQuery(id+"F0.wireOp",EDGE,"E3")]}),1.0]])],"derivedFrom":subQ1})])]}),makeQuery(id+"F1.opExtrude","SWEPT_FACE",FACE,{"disambiguationData":[OSD([subQ1]),TDD([makeQuery(id+"F0.imprint","IMPRINT",EDGE,{"disambiguationData":[TD([[makeQuery(id+"F0.imprint","INTERSECT",VERTEX,{"derivedFrom":[subQ1,sQuery(id+"F0.wireOp",EDGE,"E8")]}),1.0]])],"derivedFrom":subQ1})])]}),makeQuery(id+"F1.opExtrude","SWEPT_FACE",FACE,{"disambiguationData":[OSD([subQ1]),TDD([makeQuery(id+"F0.imprint","IMPRINT",EDGE,{"disambiguationData":[TD([[makeQuery(id+"F0.imprint","INTERSECT",VERTEX,{"derivedFrom":[subQ1,sQuery(id+"F0.wireOp",EDGE,"E6")]}),1.0]])],"derivedFrom":subQ1})])]}),makeQuery(id+"F1.opExtrude","SWEPT_FACE",FACE,{"disambiguationData":[OSD([subQ1]),TDD([makeQuery(id+"F0.imprint","IMPRINT",EDGE,{"disambiguationData":[TD([[makeQuery(id+"F0.imprint","INTERSECT",VERTEX,{"derivedFrom":[subQ1,sQuery(id+"F0.wireOp",EDGE,"E5")]}),-1.0]])],"derivedFrom":subQ1})])]}),makeQuery(id+"F1.opExtrude","SWEPT_FACE",FACE,{"disambiguationData":[OSD([subQ1]),TDD([makeQuery(id+"F0.imprint","IMPRINT",EDGE,{"disambiguationData":[TD([[makeQuery(id+"F0.imprint","INTERSECT",VERTEX,{"derivedFrom":[subQ1,sQuery(id+"F0.wireOp",EDGE,"E26.MirrorCS")]}),1.0]])],"derivedFrom":subQ1})])]}),makeQuery(id+"F1.opExtrude","SWEPT_FACE",FACE,{"disambiguationData":[OSD([subQ1]),TDD([makeQuery(id+"F0.imprint","IMPRINT",EDGE,{"disambiguationData":[TD([[makeQuery(id+"F0.imprint","INTERSECT",VERTEX,{"derivedFrom":[subQ1,sQuery(id+"F0.wireOp",EDGE,"E24.MirrorCS")]}),1.0]])],"derivedFrom":subQ1})])]}),makeQuery(id+"F1.opExtrude","SWEPT_FACE",FACE,{"disambiguationData":[OSD([subQ1]),TDD([makeQuery(id+"F0.imprint","IMPRINT",EDGE,{"disambiguationData":[TD([[makeQuery(id+"F0.imprint","INTERSECT",VERTEX,{"derivedFrom":[subQ1,sQuery(id+"F0.wireOp",EDGE,"E22.MirrorCS")]}),1.0]])],"derivedFrom":subQ1})])]}),makeQuery(id+"F1.opExtrude","SWEPT_FACE",FACE,{"disambiguationData":[OSD([subQ1]),TDD([makeQuery(id+"F0.imprint","IMPRINT",EDGE,{"disambiguationData":[TD([[makeQuery(id+"F0.imprint","INTERSECT",VERTEX,{"derivedFrom":[subQ1,sQuery(id+"F0.wireOp",EDGE,"E20.MirrorCS")]}),1.0]])],"derivedFrom":subQ1})])]}),makeQuery(id+"F1.opExtrude","SWEPT_FACE",FACE,{"disambiguationData":[OSD([subQ1]),TDD([makeQuery(id+"F0.imprint","IMPRINT",EDGE,{"disambiguationData":[TD([[makeQuery(id+"F0.imprint","INTERSECT",VERTEX,{"derivedFrom":[subQ1,sQuery(id+"F0.wireOp",EDGE,"E18.MirrorCS")]}),1.0]])],"derivedFrom":subQ1})])]}),makeQuery(id+"F1.opExtrude","SWEPT_FACE",FACE,{"disambiguationData":[OSD([subQ1]),TDD([makeQuery(id+"F0.imprint","IMPRINT",EDGE,{"disambiguationData":[TD([[makeQuery(id+"F0.imprint","INTERSECT",VERTEX,{"derivedFrom":[subQ1,sQuery(id+"F0.wireOp",EDGE,"E17.MirrorCS")]}),-1.0]])],"derivedFrom":subQ1})])]})],"fromTools":[makeQuery(id+"F5.opSweep","SWEPT_FACE",FACE,{"disambiguationData":[OSD([subQ3,subQ1,subQ0]),TDD([subQ4,makeQuery(id+"F4.imprint","IMPRINT",EDGE,{"disambiguationData":[TD([[makeQuery(id+"F4.imprint","INTERSECT",VERTEX,{"derivedFrom":[subQ2,sQuery(id+"F4.wireOp",EDGE,"E30")]}),1.0]])],"derivedFrom":subQ2})])]}),makeQuery(id+"F5.opSweep","SWEPT_FACE",FACE,{"disambiguationData":[OSD([subQ3,subQ1,subQ0]),TDD([subQ4,makeQuery(id+"F4.imprint","IMPRINT",EDGE,{"disambiguationData":[TD([[makeQuery(id+"F4.imprint","INTERSECT",VERTEX,{"derivedFrom":[subQ2,sQuery(id+"F4.wireOp",EDGE,"E32.MirrorCS")]}),1.0]])],"derivedFrom":subQ2})])]}),makeQuery(id+"F5.opSweep","SWEPT_FACE",FACE,{"disambiguationData":[OSD([subQ3,subQ1,subQ0]),TDD([subQ4,makeQuery(id+"F4.imprint","IMPRINT",EDGE,{"disambiguationData":[TD([[makeQuery(id+"F4.imprint","INTERSECT",VERTEX,{"derivedFrom":[subQ2,sQuery(id+"F4.wireOp",EDGE,"E34.MirrorCS")]}),1.0]])],"derivedFrom":subQ2})])]}),makeQuery(id+"F5.opSweep","SWEPT_FACE",FACE,{"disambiguationData":[OSD([subQ3,subQ1,subQ0]),TDD([subQ4,makeQuery(id+"F4.imprint","IMPRINT",EDGE,{"disambiguationData":[TD([[makeQuery(id+"F4.imprint","INTERSECT",VERTEX,{"derivedFrom":[subQ2,sQuery(id+"F4.wireOp",EDGE,"E36.MirrorCS")]}),1.0]])],"derivedFrom":subQ2})])]}),makeQuery(id+"F5.opSweep","SWEPT_FACE",FACE,{"disambiguationData":[OSD([subQ3,subQ1,subQ0]),TDD([subQ4,makeQuery(id+"F4.imprint","IMPRINT",EDGE,{"disambiguationData":[TD([[makeQuery(id+"F4.imprint","INTERSECT",VERTEX,{"derivedFrom":[subQ2,sQuery(id+"F4.wireOp",EDGE,"E38.MirrorCS")]}),1.0]])],"derivedFrom":subQ2})])]}),makeQuery(id+"F5.opSweep","SWEPT_FACE",FACE,{"disambiguationData":[OSD([subQ3,subQ1,subQ0]),TDD([subQ4,makeQuery(id+"F4.imprint","IMPRINT",EDGE,{"disambiguationData":[TD([[makeQuery(id+"F4.imprint","INTERSECT",VERTEX,{"derivedFrom":[subQ2,sQuery(id+"F4.wireOp",EDGE,"E40.MirrorCS")]}),1.0]])],"derivedFrom":subQ2})])]}),makeQuery(id+"F5.opSweep","SWEPT_FACE",FACE,{"disambiguationData":[OSD([subQ3,subQ1,subQ0]),TDD([subQ4,makeQuery(id+"F4.imprint","IMPRINT",EDGE,{"disambiguationData":[TD([[makeQuery(id+"F4.imprint","INTERSECT",VERTEX,{"derivedFrom":[subQ2,sQuery(id+"F4.wireOp",EDGE,"E42.MirrorCS")]}),1.0]])],"derivedFrom":subQ2})])]})]})],"blendedInto":[makeQuery(id+"F5.boolean.opBoolean","MERGE",FACE,{"derivedFrom":[makeQuery(id+"F1.opExtrude","SWEPT_FACE",FACE,{"disambiguationData":[OSD([subQ1]),TDD([makeQuery(id+"F0.imprint","IMPRINT",EDGE,{"disambiguationData":[TD([[makeQuery(id+"F0.imprint","INTERSECT",VERTEX,{"derivedFrom":[subQ1,sQuery(id+"F0.wireOp",EDGE,"E14.MirrorCS")]}),1.0]])],"derivedFrom":subQ1})])]}),makeQuery(id+"F1.opExtrude","SWEPT_FACE",FACE,{"disambiguationData":[OSD([subQ1]),TDD([makeQuery(id+"F0.imprint","IMPRINT",EDGE,{"disambiguationData":[TD([[makeQuery(id+"F0.imprint","INTERSECT",VERTEX,{"derivedFrom":[subQ1,sQuery(id+"F0.wireOp",EDGE,"E12.MirrorCS")]}),1.0]])],"derivedFrom":subQ1})])]}),makeQuery(id+"F1.opExtrude","SWEPT_FACE",FACE,{"disambiguationData":[OSD([subQ1]),TDD([makeQuery(id+"F0.imprint","IMPRINT",EDGE,{"disambiguationData":[TD([[makeQuery(id+"F0.imprint","INTERSECT",VERTEX,{"derivedFrom":[subQ1,sQuery(id+"F0.wireOp",EDGE,"E3")]}),1.0]])],"derivedFrom":subQ1})])]}),makeQuery(id+"F1.opExtrude","SWEPT_FACE",FACE,{"disambiguationData":[OSD([subQ1]),TDD([makeQuery(id+"F0.imprint","IMPRINT",EDGE,{"disambiguationData":[TD([[makeQuery(id+"F0.imprint","INTERSECT",VERTEX,{"derivedFrom":[subQ1,sQuery(id+"F0.wireOp",EDGE,"E8")]}),1.0]])],"derivedFrom":subQ1})])]}),makeQuery(id+"F1.opExtrude","SWEPT_FACE",FACE,{"disambiguationData":[OSD([subQ1]),TDD([makeQuery(id+"F0.imprint","IMPRINT",EDGE,{"disambiguationData":[TD([[makeQuery(id+"F0.imprint","INTERSECT",VERTEX,{"derivedFrom":[subQ1,sQuery(id+"F0.wireOp",EDGE,"E6")]}),1.0]])],"derivedFrom":subQ1})])]}),makeQuery(id+"F1.opExtrude","SWEPT_FACE",FACE,{"disambiguationData":[OSD([subQ1]),TDD([makeQuery(id+"F0.imprint","IMPRINT",EDGE,{"disambiguationData":[TD([[makeQuery(id+"F0.imprint","INTERSECT",VERTEX,{"derivedFrom":[subQ1,sQuery(id+"F0.wireOp",EDGE,"E5")]}),-1.0]])],"derivedFrom":subQ1})])]}),makeQuery(id+"F1.opExtrude","SWEPT_FACE",FACE,{"disambiguationData":[OSD([subQ1]),TDD([makeQuery(id+"F0.imprint","IMPRINT",EDGE,{"disambiguationData":[TD([[makeQuery(id+"F0.imprint","INTERSECT",VERTEX,{"derivedFrom":[subQ1,sQuery(id+"F0.wireOp",EDGE,"E26.MirrorCS")]}),1.0]])],"derivedFrom":subQ1})])]}),makeQuery(id+"F1.opExtrude","SWEPT_FACE",FACE,{"disambiguationData":[OSD([subQ1]),TDD([makeQuery(id+"F0.imprint","IMPRINT",EDGE,{"disambiguationData":[TD([[makeQuery(id+"F0.imprint","INTERSECT",VERTEX,{"derivedFrom":[subQ1,sQuery(id+"F0.wireOp",EDGE,"E24.MirrorCS")]}),1.0]])],"derivedFrom":subQ1})])]}),makeQuery(id+"F1.opExtrude","SWEPT_FACE",FACE,{"disambiguationData":[OSD([subQ1]),TDD([makeQuery(id+"F0.imprint","IMPRINT",EDGE,{"disambiguationData":[TD([[makeQuery(id+"F0.imprint","INTERSECT",VERTEX,{"derivedFrom":[subQ1,sQuery(id+"F0.wireOp",EDGE,"E22.MirrorCS")]}),1.0]])],"derivedFrom":subQ1})])]}),makeQuery(id+"F1.opExtrude","SWEPT_FACE",FACE,{"disambiguationData":[OSD([subQ1]),TDD([makeQuery(id+"F0.imprint","IMPRINT",EDGE,{"disambiguationData":[TD([[makeQuery(id+"F0.imprint","INTERSECT",VERTEX,{"derivedFrom":[subQ1,sQuery(id+"F0.wireOp",EDGE,"E20.MirrorCS")]}),1.0]])],"derivedFrom":subQ1})])]}),makeQuery(id+"F1.opExtrude","SWEPT_FACE",FACE,{"disambiguationData":[OSD([subQ1]),TDD([makeQuery(id+"F0.imprint","IMPRINT",EDGE,{"disambiguationData":[TD([[makeQuery(id+"F0.imprint","INTERSECT",VERTEX,{"derivedFrom":[subQ1,sQuery(id+"F0.wireOp",EDGE,"E18.MirrorCS")]}),1.0]])],"derivedFrom":subQ1})])]}),makeQuery(id+"F1.opExtrude","SWEPT_FACE",FACE,{"disambiguationData":[OSD([subQ1]),TDD([makeQuery(id+"F0.imprint","IMPRINT",EDGE,{"disambiguationData":[TD([[makeQuery(id+"F0.imprint","INTERSECT",VERTEX,{"derivedFrom":[subQ1,sQuery(id+"F0.wireOp",EDGE,"E17.MirrorCS")]}),-1.0]])],"derivedFrom":subQ1})])]})],"fromTools":[makeQuery(id+"F5.opSweep","SWEPT_FACE",FACE,{"disambiguationData":[OSD([subQ3,subQ1,subQ0]),TDD([subQ4,makeQuery(id+"F4.imprint","IMPRINT",EDGE,{"disambiguationData":[TD([[makeQuery(id+"F4.imprint","INTERSECT",VERTEX,{"derivedFrom":[subQ2,sQuery(id+"F4.wireOp",EDGE,"E30")]}),1.0]])],"derivedFrom":subQ2})])]}),makeQuery(id+"F5.opSweep","SWEPT_FACE",FACE,{"disambiguationData":[OSD([subQ3,subQ1,subQ0]),TDD([subQ4,makeQuery(id+"F4.imprint","IMPRINT",EDGE,{"disambiguationData":[TD([[makeQuery(id+"F4.imprint","INTERSECT",VERTEX,{"derivedFrom":[subQ2,sQuery(id+"F4.wireOp",EDGE,"E32.MirrorCS")]}),1.0]])],"derivedFrom":subQ2})])]}),makeQuery(id+"F5.opSweep","SWEPT_FACE",FACE,{"disambiguationData":[OSD([subQ3,subQ1,subQ0]),TDD([subQ4,makeQuery(id+"F4.imprint","IMPRINT",EDGE,{"disambiguationData":[TD([[makeQuery(id+"F4.imprint","INTERSECT",VERTEX,{"derivedFrom":[subQ2,sQuery(id+"F4.wireOp",EDGE,"E34.MirrorCS")]}),1.0]])],"derivedFrom":subQ2})])]}),makeQuery(id+"F5.opSweep","SWEPT_FACE",FACE,{"disambiguationData":[OSD([subQ3,subQ1,subQ0]),TDD([subQ4,makeQuery(id+"F4.imprint","IMPRINT",EDGE,{"disambiguationData":[TD([[makeQuery(id+"F4.imprint","INTERSECT",VERTEX,{"derivedFrom":[subQ2,sQuery(id+"F4.wireOp",EDGE,"E36.MirrorCS")]}),1.0]])],"derivedFrom":subQ2})])]}),makeQuery(id+"F5.opSweep","SWEPT_FACE",FACE,{"disambiguationData":[OSD([subQ3,subQ1,subQ0]),TDD([subQ4,makeQuery(id+"F4.imprint","IMPRINT",EDGE,{"disambiguationData":[TD([[makeQuery(id+"F4.imprint","INTERSECT",VERTEX,{"derivedFrom":[subQ2,sQuery(id+"F4.wireOp",EDGE,"E38.MirrorCS")]}),1.0]])],"derivedFrom":subQ2})])]}),makeQuery(id+"F5.opSweep","SWEPT_FACE",FACE,{"disambiguationData":[OSD([subQ3,subQ1,subQ0]),TDD([subQ4,makeQuery(id+"F4.imprint","IMPRINT",EDGE,{"disambiguationData":[TD([[makeQuery(id+"F4.imprint","INTERSECT",VERTEX,{"derivedFrom":[subQ2,sQuery(id+"F4.wireOp",EDGE,"E40.MirrorCS")]}),1.0]])],"derivedFrom":subQ2})])]}),makeQuery(id+"F5.opSweep","SWEPT_FACE",FACE,{"disambiguationData":[OSD([subQ3,subQ1,subQ0]),TDD([subQ4,makeQuery(id+"F4.imprint","IMPRINT",EDGE,{"disambiguationData":[TD([[makeQuery(id+"F4.imprint","INTERSECT",VERTEX,{"derivedFrom":[subQ2,sQuery(id+"F4.wireOp",EDGE,"E42.MirrorCS")]}),1.0]])],"derivedFrom":subQ2})])]})]})]});}
            var Q7;
            Q7=makeQuery(id+"F8.opFillet","BLEND_EDGE",EDGE,{"blendedFrom":[makeQuery(id+"F3.opExtrude","CAP_EDGE",EDGE,{"disambiguationData":[OSD([sQuery(id+"F2.wireOp",EDGE,"E29")])],"isStart":true}),makeQuery(id+"F7.opFillet","BLEND_FACE",FACE,{"disambiguationData":[OSD([sQuery(id+"F0.wireOp",EDGE,"E2"),sQuery(id+"F0.wireOp",EDGE,"E12.MirrorCS")])]})],"blendedInto":[makeQuery(id+"F7.opFillet","BLEND_FACE",FACE,{"disambiguationData":[OSD([sQuery(id+"F0.wireOp",EDGE,"E2"),sQuery(id+"F0.wireOp",EDGE,"E12.MirrorCS")])]})]});
            var Q8;
            {var subQ0=sQuery(id+"F0.wireOp",EDGE,"E11.MirrorCS");var subQ1=sQuery(id+"F2.wireOp",EDGE,"E29");var subQ3=sQuery(id+"F0.wireOp",EDGE,"E2");Q8=makeQuery(id+"F8.opFillet","BLEND_EDGE",EDGE,{"blendedFrom":[makeQuery(id+"F3.opExtrude","CAP_EDGE",EDGE,{"disambiguationData":[OSD([subQ1])],"isStart":true}),makeQuery(id+"F5.boolean.opBoolean","SPLIT",FACE,{"disambiguationData":[TD([makeQuery(id+"F3.opExtrude","CAP_FACE",FACE,{"disambiguationData":[OSD([subQ1])],"isStart":true})])],"derivedFrom":makeQuery(id+"F1.opExtrude","SWEPT_FACE",FACE,{"disambiguationData":[OSD([subQ3]),TDD([makeQuery(id+"F0.imprint","IMPRINT",EDGE,{"disambiguationData":[TD([[makeQuery(id+"F0.imprint","INTERSECT",VERTEX,{"derivedFrom":[subQ3,subQ0]}),1.0]])],"derivedFrom":subQ3})])]})})],"blendedInto":[makeQuery(id+"F5.boolean.opBoolean","SPLIT",FACE,{"disambiguationData":[TD([makeQuery(id+"F3.opExtrude","CAP_FACE",FACE,{"disambiguationData":[OSD([subQ1])],"isStart":true})])],"derivedFrom":makeQuery(id+"F1.opExtrude","SWEPT_FACE",FACE,{"disambiguationData":[OSD([subQ3]),TDD([makeQuery(id+"F0.imprint","IMPRINT",EDGE,{"disambiguationData":[TD([[makeQuery(id+"F0.imprint","INTERSECT",VERTEX,{"derivedFrom":[subQ3,subQ0]}),1.0]])],"derivedFrom":subQ3})])]})})]});}
            var Q9;
            {var subQ0=sQuery(id+"F0.wireOp",EDGE,"E27.MirrorCS");var subQ1=sQuery(id+"F0.wireOp",EDGE,"E1");var subQ2=makeQuery(id+"F1.opExtrude","SWEPT_EDGE",EDGE,{"disambiguationData":[OSD([subQ1,subQ0])]});var subQ3=sQuery(id+"F0.wireOp",EDGE,"E0");var subQ4=makeQuery(id+"F1.opExtrude","CAP_EDGE",EDGE,{"disambiguationData":[OSD([subQ3])],"isStart":true});Q9=makeQuery(id+"F8.opFillet","BLEND_EDGE",EDGE,{"disambiguationData":[OD(0.0)],"blendedFrom":[makeQuery(id+"F3.opExtrude","CAP_EDGE",EDGE,{"disambiguationData":[OSD([sQuery(id+"F2.wireOp",EDGE,"E29")])],"isStart":true}),makeQuery(id+"F5.boolean.opBoolean","MERGE",FACE,{"derivedFrom":[makeQuery(id+"F1.opExtrude","SWEPT_FACE",FACE,{"disambiguationData":[OSD([subQ1]),TDD([makeQuery(id+"F0.imprint","IMPRINT",EDGE,{"disambiguationData":[TD([[makeQuery(id+"F0.imprint","INTERSECT",VERTEX,{"derivedFrom":[subQ1,sQuery(id+"F0.wireOp",EDGE,"E14.MirrorCS")]}),1.0]])],"derivedFrom":subQ1})])]}),makeQuery(id+"F1.opExtrude","SWEPT_FACE",FACE,{"disambiguationData":[OSD([subQ1]),TDD([makeQuery(id+"F0.imprint","IMPRINT",EDGE,{"disambiguationData":[TD([[makeQuery(id+"F0.imprint","INTERSECT",VERTEX,{"derivedFrom":[subQ1,sQuery(id+"F0.wireOp",EDGE,"E12.MirrorCS")]}),1.0]])],"derivedFrom":subQ1})])]}),makeQuery(id+"F1.opExtrude","SWEPT_FACE",FACE,{"disambiguationData":[OSD([subQ1]),TDD([makeQuery(id+"F0.imprint","IMPRINT",EDGE,{"disambiguationData":[TD([[makeQuery(id+"F0.imprint","INTERSECT",VERTEX,{"derivedFrom":[subQ1,sQuery(id+"F0.wireOp",EDGE,"E3")]}),1.0]])],"derivedFrom":subQ1})])]}),makeQuery(id+"F1.opExtrude","SWEPT_FACE",FACE,{"disambiguationData":[OSD([subQ1]),TDD([makeQuery(id+"F0.imprint","IMPRINT",EDGE,{"disambiguationData":[TD([[makeQuery(id+"F0.imprint","INTERSECT",VERTEX,{"derivedFrom":[subQ1,sQuery(id+"F0.wireOp",EDGE,"E8")]}),1.0]])],"derivedFrom":subQ1})])]}),makeQuery(id+"F1.opExtrude","SWEPT_FACE",FACE,{"disambiguationData":[OSD([subQ1]),TDD([makeQuery(id+"F0.imprint","IMPRINT",EDGE,{"disambiguationData":[TD([[makeQuery(id+"F0.imprint","INTERSECT",VERTEX,{"derivedFrom":[subQ1,sQuery(id+"F0.wireOp",EDGE,"E6")]}),1.0]])],"derivedFrom":subQ1})])]}),makeQuery(id+"F1.opExtrude","SWEPT_FACE",FACE,{"disambiguationData":[OSD([subQ1]),TDD([makeQuery(id+"F0.imprint","IMPRINT",EDGE,{"disambiguationData":[TD([[makeQuery(id+"F0.imprint","INTERSECT",VERTEX,{"derivedFrom":[subQ1,sQuery(id+"F0.wireOp",EDGE,"E5")]}),-1.0]])],"derivedFrom":subQ1})])]}),makeQuery(id+"F1.opExtrude","SWEPT_FACE",FACE,{"disambiguationData":[OSD([subQ1]),TDD([makeQuery(id+"F0.imprint","IMPRINT",EDGE,{"disambiguationData":[TD([[makeQuery(id+"F0.imprint","INTERSECT",VERTEX,{"derivedFrom":[subQ1,sQuery(id+"F0.wireOp",EDGE,"E26.MirrorCS")]}),1.0]])],"derivedFrom":subQ1})])]}),makeQuery(id+"F1.opExtrude","SWEPT_FACE",FACE,{"disambiguationData":[OSD([subQ1]),TDD([makeQuery(id+"F0.imprint","IMPRINT",EDGE,{"disambiguationData":[TD([[makeQuery(id+"F0.imprint","INTERSECT",VERTEX,{"derivedFrom":[subQ1,sQuery(id+"F0.wireOp",EDGE,"E24.MirrorCS")]}),1.0]])],"derivedFrom":subQ1})])]}),makeQuery(id+"F1.opExtrude","SWEPT_FACE",FACE,{"disambiguationData":[OSD([subQ1]),TDD([makeQuery(id+"F0.imprint","IMPRINT",EDGE,{"disambiguationData":[TD([[makeQuery(id+"F0.imprint","INTERSECT",VERTEX,{"derivedFrom":[subQ1,sQuery(id+"F0.wireOp",EDGE,"E22.MirrorCS")]}),1.0]])],"derivedFrom":subQ1})])]}),makeQuery(id+"F1.opExtrude","SWEPT_FACE",FACE,{"disambiguationData":[OSD([subQ1]),TDD([makeQuery(id+"F0.imprint","IMPRINT",EDGE,{"disambiguationData":[TD([[makeQuery(id+"F0.imprint","INTERSECT",VERTEX,{"derivedFrom":[subQ1,sQuery(id+"F0.wireOp",EDGE,"E20.MirrorCS")]}),1.0]])],"derivedFrom":subQ1})])]}),makeQuery(id+"F1.opExtrude","SWEPT_FACE",FACE,{"disambiguationData":[OSD([subQ1]),TDD([makeQuery(id+"F0.imprint","IMPRINT",EDGE,{"disambiguationData":[TD([[makeQuery(id+"F0.imprint","INTERSECT",VERTEX,{"derivedFrom":[subQ1,sQuery(id+"F0.wireOp",EDGE,"E18.MirrorCS")]}),1.0]])],"derivedFrom":subQ1})])]}),makeQuery(id+"F1.opExtrude","SWEPT_FACE",FACE,{"disambiguationData":[OSD([subQ1]),TDD([makeQuery(id+"F0.imprint","IMPRINT",EDGE,{"disambiguationData":[TD([[makeQuery(id+"F0.imprint","INTERSECT",VERTEX,{"derivedFrom":[subQ1,sQuery(id+"F0.wireOp",EDGE,"E17.MirrorCS")]}),-1.0]])],"derivedFrom":subQ1})])]})],"fromTools":[makeQuery(id+"F5.opSweep","SWEPT_FACE",FACE,{"disambiguationData":[OSD([subQ3,subQ1,subQ0]),TDD([subQ4,makeQuery(id+"F4.imprint","IMPRINT",EDGE,{"disambiguationData":[TD([[makeQuery(id+"F4.imprint","INTERSECT",VERTEX,{"derivedFrom":[subQ2,sQuery(id+"F4.wireOp",EDGE,"E30")]}),1.0]])],"derivedFrom":subQ2})])]}),makeQuery(id+"F5.opSweep","SWEPT_FACE",FACE,{"disambiguationData":[OSD([subQ3,subQ1,subQ0]),TDD([subQ4,makeQuery(id+"F4.imprint","IMPRINT",EDGE,{"disambiguationData":[TD([[makeQuery(id+"F4.imprint","INTERSECT",VERTEX,{"derivedFrom":[subQ2,sQuery(id+"F4.wireOp",EDGE,"E32.MirrorCS")]}),1.0]])],"derivedFrom":subQ2})])]}),makeQuery(id+"F5.opSweep","SWEPT_FACE",FACE,{"disambiguationData":[OSD([subQ3,subQ1,subQ0]),TDD([subQ4,makeQuery(id+"F4.imprint","IMPRINT",EDGE,{"disambiguationData":[TD([[makeQuery(id+"F4.imprint","INTERSECT",VERTEX,{"derivedFrom":[subQ2,sQuery(id+"F4.wireOp",EDGE,"E34.MirrorCS")]}),1.0]])],"derivedFrom":subQ2})])]}),makeQuery(id+"F5.opSweep","SWEPT_FACE",FACE,{"disambiguationData":[OSD([subQ3,subQ1,subQ0]),TDD([subQ4,makeQuery(id+"F4.imprint","IMPRINT",EDGE,{"disambiguationData":[TD([[makeQuery(id+"F4.imprint","INTERSECT",VERTEX,{"derivedFrom":[subQ2,sQuery(id+"F4.wireOp",EDGE,"E36.MirrorCS")]}),1.0]])],"derivedFrom":subQ2})])]}),makeQuery(id+"F5.opSweep","SWEPT_FACE",FACE,{"disambiguationData":[OSD([subQ3,subQ1,subQ0]),TDD([subQ4,makeQuery(id+"F4.imprint","IMPRINT",EDGE,{"disambiguationData":[TD([[makeQuery(id+"F4.imprint","INTERSECT",VERTEX,{"derivedFrom":[subQ2,sQuery(id+"F4.wireOp",EDGE,"E38.MirrorCS")]}),1.0]])],"derivedFrom":subQ2})])]}),makeQuery(id+"F5.opSweep","SWEPT_FACE",FACE,{"disambiguationData":[OSD([subQ3,subQ1,subQ0]),TDD([subQ4,makeQuery(id+"F4.imprint","IMPRINT",EDGE,{"disambiguationData":[TD([[makeQuery(id+"F4.imprint","INTERSECT",VERTEX,{"derivedFrom":[subQ2,sQuery(id+"F4.wireOp",EDGE,"E40.MirrorCS")]}),1.0]])],"derivedFrom":subQ2})])]}),makeQuery(id+"F5.opSweep","SWEPT_FACE",FACE,{"disambiguationData":[OSD([subQ3,subQ1,subQ0]),TDD([subQ4,makeQuery(id+"F4.imprint","IMPRINT",EDGE,{"disambiguationData":[TD([[makeQuery(id+"F4.imprint","INTERSECT",VERTEX,{"derivedFrom":[subQ2,sQuery(id+"F4.wireOp",EDGE,"E42.MirrorCS")]}),1.0]])],"derivedFrom":subQ2})])]})]})],"blendedInto":[makeQuery(id+"F5.boolean.opBoolean","MERGE",FACE,{"derivedFrom":[makeQuery(id+"F1.opExtrude","SWEPT_FACE",FACE,{"disambiguationData":[OSD([subQ1]),TDD([makeQuery(id+"F0.imprint","IMPRINT",EDGE,{"disambiguationData":[TD([[makeQuery(id+"F0.imprint","INTERSECT",VERTEX,{"derivedFrom":[subQ1,sQuery(id+"F0.wireOp",EDGE,"E14.MirrorCS")]}),1.0]])],"derivedFrom":subQ1})])]}),makeQuery(id+"F1.opExtrude","SWEPT_FACE",FACE,{"disambiguationData":[OSD([subQ1]),TDD([makeQuery(id+"F0.imprint","IMPRINT",EDGE,{"disambiguationData":[TD([[makeQuery(id+"F0.imprint","INTERSECT",VERTEX,{"derivedFrom":[subQ1,sQuery(id+"F0.wireOp",EDGE,"E12.MirrorCS")]}),1.0]])],"derivedFrom":subQ1})])]}),makeQuery(id+"F1.opExtrude","SWEPT_FACE",FACE,{"disambiguationData":[OSD([subQ1]),TDD([makeQuery(id+"F0.imprint","IMPRINT",EDGE,{"disambiguationData":[TD([[makeQuery(id+"F0.imprint","INTERSECT",VERTEX,{"derivedFrom":[subQ1,sQuery(id+"F0.wireOp",EDGE,"E3")]}),1.0]])],"derivedFrom":subQ1})])]}),makeQuery(id+"F1.opExtrude","SWEPT_FACE",FACE,{"disambiguationData":[OSD([subQ1]),TDD([makeQuery(id+"F0.imprint","IMPRINT",EDGE,{"disambiguationData":[TD([[makeQuery(id+"F0.imprint","INTERSECT",VERTEX,{"derivedFrom":[subQ1,sQuery(id+"F0.wireOp",EDGE,"E8")]}),1.0]])],"derivedFrom":subQ1})])]}),makeQuery(id+"F1.opExtrude","SWEPT_FACE",FACE,{"disambiguationData":[OSD([subQ1]),TDD([makeQuery(id+"F0.imprint","IMPRINT",EDGE,{"disambiguationData":[TD([[makeQuery(id+"F0.imprint","INTERSECT",VERTEX,{"derivedFrom":[subQ1,sQuery(id+"F0.wireOp",EDGE,"E6")]}),1.0]])],"derivedFrom":subQ1})])]}),makeQuery(id+"F1.opExtrude","SWEPT_FACE",FACE,{"disambiguationData":[OSD([subQ1]),TDD([makeQuery(id+"F0.imprint","IMPRINT",EDGE,{"disambiguationData":[TD([[makeQuery(id+"F0.imprint","INTERSECT",VERTEX,{"derivedFrom":[subQ1,sQuery(id+"F0.wireOp",EDGE,"E5")]}),-1.0]])],"derivedFrom":subQ1})])]}),makeQuery(id+"F1.opExtrude","SWEPT_FACE",FACE,{"disambiguationData":[OSD([subQ1]),TDD([makeQuery(id+"F0.imprint","IMPRINT",EDGE,{"disambiguationData":[TD([[makeQuery(id+"F0.imprint","INTERSECT",VERTEX,{"derivedFrom":[subQ1,sQuery(id+"F0.wireOp",EDGE,"E26.MirrorCS")]}),1.0]])],"derivedFrom":subQ1})])]}),makeQuery(id+"F1.opExtrude","SWEPT_FACE",FACE,{"disambiguationData":[OSD([subQ1]),TDD([makeQuery(id+"F0.imprint","IMPRINT",EDGE,{"disambiguationData":[TD([[makeQuery(id+"F0.imprint","INTERSECT",VERTEX,{"derivedFrom":[subQ1,sQuery(id+"F0.wireOp",EDGE,"E24.MirrorCS")]}),1.0]])],"derivedFrom":subQ1})])]}),makeQuery(id+"F1.opExtrude","SWEPT_FACE",FACE,{"disambiguationData":[OSD([subQ1]),TDD([makeQuery(id+"F0.imprint","IMPRINT",EDGE,{"disambiguationData":[TD([[makeQuery(id+"F0.imprint","INTERSECT",VERTEX,{"derivedFrom":[subQ1,sQuery(id+"F0.wireOp",EDGE,"E22.MirrorCS")]}),1.0]])],"derivedFrom":subQ1})])]}),makeQuery(id+"F1.opExtrude","SWEPT_FACE",FACE,{"disambiguationData":[OSD([subQ1]),TDD([makeQuery(id+"F0.imprint","IMPRINT",EDGE,{"disambiguationData":[TD([[makeQuery(id+"F0.imprint","INTERSECT",VERTEX,{"derivedFrom":[subQ1,sQuery(id+"F0.wireOp",EDGE,"E20.MirrorCS")]}),1.0]])],"derivedFrom":subQ1})])]}),makeQuery(id+"F1.opExtrude","SWEPT_FACE",FACE,{"disambiguationData":[OSD([subQ1]),TDD([makeQuery(id+"F0.imprint","IMPRINT",EDGE,{"disambiguationData":[TD([[makeQuery(id+"F0.imprint","INTERSECT",VERTEX,{"derivedFrom":[subQ1,sQuery(id+"F0.wireOp",EDGE,"E18.MirrorCS")]}),1.0]])],"derivedFrom":subQ1})])]}),makeQuery(id+"F1.opExtrude","SWEPT_FACE",FACE,{"disambiguationData":[OSD([subQ1]),TDD([makeQuery(id+"F0.imprint","IMPRINT",EDGE,{"disambiguationData":[TD([[makeQuery(id+"F0.imprint","INTERSECT",VERTEX,{"derivedFrom":[subQ1,sQuery(id+"F0.wireOp",EDGE,"E17.MirrorCS")]}),-1.0]])],"derivedFrom":subQ1})])]})],"fromTools":[makeQuery(id+"F5.opSweep","SWEPT_FACE",FACE,{"disambiguationData":[OSD([subQ3,subQ1,subQ0]),TDD([subQ4,makeQuery(id+"F4.imprint","IMPRINT",EDGE,{"disambiguationData":[TD([[makeQuery(id+"F4.imprint","INTERSECT",VERTEX,{"derivedFrom":[subQ2,sQuery(id+"F4.wireOp",EDGE,"E30")]}),1.0]])],"derivedFrom":subQ2})])]}),makeQuery(id+"F5.opSweep","SWEPT_FACE",FACE,{"disambiguationData":[OSD([subQ3,subQ1,subQ0]),TDD([subQ4,makeQuery(id+"F4.imprint","IMPRINT",EDGE,{"disambiguationData":[TD([[makeQuery(id+"F4.imprint","INTERSECT",VERTEX,{"derivedFrom":[subQ2,sQuery(id+"F4.wireOp",EDGE,"E32.MirrorCS")]}),1.0]])],"derivedFrom":subQ2})])]}),makeQuery(id+"F5.opSweep","SWEPT_FACE",FACE,{"disambiguationData":[OSD([subQ3,subQ1,subQ0]),TDD([subQ4,makeQuery(id+"F4.imprint","IMPRINT",EDGE,{"disambiguationData":[TD([[makeQuery(id+"F4.imprint","INTERSECT",VERTEX,{"derivedFrom":[subQ2,sQuery(id+"F4.wireOp",EDGE,"E34.MirrorCS")]}),1.0]])],"derivedFrom":subQ2})])]}),makeQuery(id+"F5.opSweep","SWEPT_FACE",FACE,{"disambiguationData":[OSD([subQ3,subQ1,subQ0]),TDD([subQ4,makeQuery(id+"F4.imprint","IMPRINT",EDGE,{"disambiguationData":[TD([[makeQuery(id+"F4.imprint","INTERSECT",VERTEX,{"derivedFrom":[subQ2,sQuery(id+"F4.wireOp",EDGE,"E36.MirrorCS")]}),1.0]])],"derivedFrom":subQ2})])]}),makeQuery(id+"F5.opSweep","SWEPT_FACE",FACE,{"disambiguationData":[OSD([subQ3,subQ1,subQ0]),TDD([subQ4,makeQuery(id+"F4.imprint","IMPRINT",EDGE,{"disambiguationData":[TD([[makeQuery(id+"F4.imprint","INTERSECT",VERTEX,{"derivedFrom":[subQ2,sQuery(id+"F4.wireOp",EDGE,"E38.MirrorCS")]}),1.0]])],"derivedFrom":subQ2})])]}),makeQuery(id+"F5.opSweep","SWEPT_FACE",FACE,{"disambiguationData":[OSD([subQ3,subQ1,subQ0]),TDD([subQ4,makeQuery(id+"F4.imprint","IMPRINT",EDGE,{"disambiguationData":[TD([[makeQuery(id+"F4.imprint","INTERSECT",VERTEX,{"derivedFrom":[subQ2,sQuery(id+"F4.wireOp",EDGE,"E40.MirrorCS")]}),1.0]])],"derivedFrom":subQ2})])]}),makeQuery(id+"F5.opSweep","SWEPT_FACE",FACE,{"disambiguationData":[OSD([subQ3,subQ1,subQ0]),TDD([subQ4,makeQuery(id+"F4.imprint","IMPRINT",EDGE,{"disambiguationData":[TD([[makeQuery(id+"F4.imprint","INTERSECT",VERTEX,{"derivedFrom":[subQ2,sQuery(id+"F4.wireOp",EDGE,"E42.MirrorCS")]}),1.0]])],"derivedFrom":subQ2})])]})]})]});}
            var Q10;
            {var subQ0=sQuery(id+"F0.wireOp",EDGE,"E3");var subQ2=sQuery(id+"F2.wireOp",EDGE,"E29");var subQ3=sQuery(id+"F0.wireOp",EDGE,"E2");Q10=makeQuery(id+"F8.opFillet","BLEND_EDGE",EDGE,{"blendedFrom":[makeQuery(id+"F3.opExtrude","CAP_EDGE",EDGE,{"disambiguationData":[OSD([subQ2])],"isStart":true}),makeQuery(id+"F5.boolean.opBoolean","SPLIT",FACE,{"disambiguationData":[TD([makeQuery(id+"F3.opExtrude","CAP_FACE",FACE,{"disambiguationData":[OSD([subQ2])],"isStart":true})])],"derivedFrom":makeQuery(id+"F1.opExtrude","SWEPT_FACE",FACE,{"disambiguationData":[OSD([subQ3]),TDD([makeQuery(id+"F0.imprint","IMPRINT",EDGE,{"disambiguationData":[TD([[makeQuery(id+"F0.imprint","INTERSECT",VERTEX,{"derivedFrom":[subQ3,subQ0]}),-1.0]])],"derivedFrom":subQ3})])]})})],"blendedInto":[makeQuery(id+"F5.boolean.opBoolean","SPLIT",FACE,{"disambiguationData":[TD([makeQuery(id+"F3.opExtrude","CAP_FACE",FACE,{"disambiguationData":[OSD([subQ2])],"isStart":true})])],"derivedFrom":makeQuery(id+"F1.opExtrude","SWEPT_FACE",FACE,{"disambiguationData":[OSD([subQ3]),TDD([makeQuery(id+"F0.imprint","IMPRINT",EDGE,{"disambiguationData":[TD([[makeQuery(id+"F0.imprint","INTERSECT",VERTEX,{"derivedFrom":[subQ3,subQ0]}),-1.0]])],"derivedFrom":subQ3})])]})})]});}
            var Q11;
            {var subQ0=sQuery(id+"F0.wireOp",EDGE,"E27.MirrorCS");var subQ1=sQuery(id+"F0.wireOp",EDGE,"E1");var subQ2=makeQuery(id+"F1.opExtrude","SWEPT_EDGE",EDGE,{"disambiguationData":[OSD([subQ1,subQ0])]});var subQ3=sQuery(id+"F0.wireOp",EDGE,"E0");var subQ4=makeQuery(id+"F1.opExtrude","CAP_EDGE",EDGE,{"disambiguationData":[OSD([subQ3])],"isStart":true});Q11=makeQuery(id+"F8.opFillet","BLEND_EDGE",EDGE,{"disambiguationData":[OD(3.0)],"blendedFrom":[makeQuery(id+"F3.opExtrude","CAP_EDGE",EDGE,{"disambiguationData":[OSD([sQuery(id+"F2.wireOp",EDGE,"E29")])],"isStart":true}),makeQuery(id+"F5.boolean.opBoolean","MERGE",FACE,{"derivedFrom":[makeQuery(id+"F1.opExtrude","SWEPT_FACE",FACE,{"disambiguationData":[OSD([subQ1]),TDD([makeQuery(id+"F0.imprint","IMPRINT",EDGE,{"disambiguationData":[TD([[makeQuery(id+"F0.imprint","INTERSECT",VERTEX,{"derivedFrom":[subQ1,sQuery(id+"F0.wireOp",EDGE,"E14.MirrorCS")]}),1.0]])],"derivedFrom":subQ1})])]}),makeQuery(id+"F1.opExtrude","SWEPT_FACE",FACE,{"disambiguationData":[OSD([subQ1]),TDD([makeQuery(id+"F0.imprint","IMPRINT",EDGE,{"disambiguationData":[TD([[makeQuery(id+"F0.imprint","INTERSECT",VERTEX,{"derivedFrom":[subQ1,sQuery(id+"F0.wireOp",EDGE,"E12.MirrorCS")]}),1.0]])],"derivedFrom":subQ1})])]}),makeQuery(id+"F1.opExtrude","SWEPT_FACE",FACE,{"disambiguationData":[OSD([subQ1]),TDD([makeQuery(id+"F0.imprint","IMPRINT",EDGE,{"disambiguationData":[TD([[makeQuery(id+"F0.imprint","INTERSECT",VERTEX,{"derivedFrom":[subQ1,sQuery(id+"F0.wireOp",EDGE,"E3")]}),1.0]])],"derivedFrom":subQ1})])]}),makeQuery(id+"F1.opExtrude","SWEPT_FACE",FACE,{"disambiguationData":[OSD([subQ1]),TDD([makeQuery(id+"F0.imprint","IMPRINT",EDGE,{"disambiguationData":[TD([[makeQuery(id+"F0.imprint","INTERSECT",VERTEX,{"derivedFrom":[subQ1,sQuery(id+"F0.wireOp",EDGE,"E8")]}),1.0]])],"derivedFrom":subQ1})])]}),makeQuery(id+"F1.opExtrude","SWEPT_FACE",FACE,{"disambiguationData":[OSD([subQ1]),TDD([makeQuery(id+"F0.imprint","IMPRINT",EDGE,{"disambiguationData":[TD([[makeQuery(id+"F0.imprint","INTERSECT",VERTEX,{"derivedFrom":[subQ1,sQuery(id+"F0.wireOp",EDGE,"E6")]}),1.0]])],"derivedFrom":subQ1})])]}),makeQuery(id+"F1.opExtrude","SWEPT_FACE",FACE,{"disambiguationData":[OSD([subQ1]),TDD([makeQuery(id+"F0.imprint","IMPRINT",EDGE,{"disambiguationData":[TD([[makeQuery(id+"F0.imprint","INTERSECT",VERTEX,{"derivedFrom":[subQ1,sQuery(id+"F0.wireOp",EDGE,"E5")]}),-1.0]])],"derivedFrom":subQ1})])]}),makeQuery(id+"F1.opExtrude","SWEPT_FACE",FACE,{"disambiguationData":[OSD([subQ1]),TDD([makeQuery(id+"F0.imprint","IMPRINT",EDGE,{"disambiguationData":[TD([[makeQuery(id+"F0.imprint","INTERSECT",VERTEX,{"derivedFrom":[subQ1,sQuery(id+"F0.wireOp",EDGE,"E26.MirrorCS")]}),1.0]])],"derivedFrom":subQ1})])]}),makeQuery(id+"F1.opExtrude","SWEPT_FACE",FACE,{"disambiguationData":[OSD([subQ1]),TDD([makeQuery(id+"F0.imprint","IMPRINT",EDGE,{"disambiguationData":[TD([[makeQuery(id+"F0.imprint","INTERSECT",VERTEX,{"derivedFrom":[subQ1,sQuery(id+"F0.wireOp",EDGE,"E24.MirrorCS")]}),1.0]])],"derivedFrom":subQ1})])]}),makeQuery(id+"F1.opExtrude","SWEPT_FACE",FACE,{"disambiguationData":[OSD([subQ1]),TDD([makeQuery(id+"F0.imprint","IMPRINT",EDGE,{"disambiguationData":[TD([[makeQuery(id+"F0.imprint","INTERSECT",VERTEX,{"derivedFrom":[subQ1,sQuery(id+"F0.wireOp",EDGE,"E22.MirrorCS")]}),1.0]])],"derivedFrom":subQ1})])]}),makeQuery(id+"F1.opExtrude","SWEPT_FACE",FACE,{"disambiguationData":[OSD([subQ1]),TDD([makeQuery(id+"F0.imprint","IMPRINT",EDGE,{"disambiguationData":[TD([[makeQuery(id+"F0.imprint","INTERSECT",VERTEX,{"derivedFrom":[subQ1,sQuery(id+"F0.wireOp",EDGE,"E20.MirrorCS")]}),1.0]])],"derivedFrom":subQ1})])]}),makeQuery(id+"F1.opExtrude","SWEPT_FACE",FACE,{"disambiguationData":[OSD([subQ1]),TDD([makeQuery(id+"F0.imprint","IMPRINT",EDGE,{"disambiguationData":[TD([[makeQuery(id+"F0.imprint","INTERSECT",VERTEX,{"derivedFrom":[subQ1,sQuery(id+"F0.wireOp",EDGE,"E18.MirrorCS")]}),1.0]])],"derivedFrom":subQ1})])]}),makeQuery(id+"F1.opExtrude","SWEPT_FACE",FACE,{"disambiguationData":[OSD([subQ1]),TDD([makeQuery(id+"F0.imprint","IMPRINT",EDGE,{"disambiguationData":[TD([[makeQuery(id+"F0.imprint","INTERSECT",VERTEX,{"derivedFrom":[subQ1,sQuery(id+"F0.wireOp",EDGE,"E17.MirrorCS")]}),-1.0]])],"derivedFrom":subQ1})])]})],"fromTools":[makeQuery(id+"F5.opSweep","SWEPT_FACE",FACE,{"disambiguationData":[OSD([subQ3,subQ1,subQ0]),TDD([subQ4,makeQuery(id+"F4.imprint","IMPRINT",EDGE,{"disambiguationData":[TD([[makeQuery(id+"F4.imprint","INTERSECT",VERTEX,{"derivedFrom":[subQ2,sQuery(id+"F4.wireOp",EDGE,"E30")]}),1.0]])],"derivedFrom":subQ2})])]}),makeQuery(id+"F5.opSweep","SWEPT_FACE",FACE,{"disambiguationData":[OSD([subQ3,subQ1,subQ0]),TDD([subQ4,makeQuery(id+"F4.imprint","IMPRINT",EDGE,{"disambiguationData":[TD([[makeQuery(id+"F4.imprint","INTERSECT",VERTEX,{"derivedFrom":[subQ2,sQuery(id+"F4.wireOp",EDGE,"E32.MirrorCS")]}),1.0]])],"derivedFrom":subQ2})])]}),makeQuery(id+"F5.opSweep","SWEPT_FACE",FACE,{"disambiguationData":[OSD([subQ3,subQ1,subQ0]),TDD([subQ4,makeQuery(id+"F4.imprint","IMPRINT",EDGE,{"disambiguationData":[TD([[makeQuery(id+"F4.imprint","INTERSECT",VERTEX,{"derivedFrom":[subQ2,sQuery(id+"F4.wireOp",EDGE,"E34.MirrorCS")]}),1.0]])],"derivedFrom":subQ2})])]}),makeQuery(id+"F5.opSweep","SWEPT_FACE",FACE,{"disambiguationData":[OSD([subQ3,subQ1,subQ0]),TDD([subQ4,makeQuery(id+"F4.imprint","IMPRINT",EDGE,{"disambiguationData":[TD([[makeQuery(id+"F4.imprint","INTERSECT",VERTEX,{"derivedFrom":[subQ2,sQuery(id+"F4.wireOp",EDGE,"E36.MirrorCS")]}),1.0]])],"derivedFrom":subQ2})])]}),makeQuery(id+"F5.opSweep","SWEPT_FACE",FACE,{"disambiguationData":[OSD([subQ3,subQ1,subQ0]),TDD([subQ4,makeQuery(id+"F4.imprint","IMPRINT",EDGE,{"disambiguationData":[TD([[makeQuery(id+"F4.imprint","INTERSECT",VERTEX,{"derivedFrom":[subQ2,sQuery(id+"F4.wireOp",EDGE,"E38.MirrorCS")]}),1.0]])],"derivedFrom":subQ2})])]}),makeQuery(id+"F5.opSweep","SWEPT_FACE",FACE,{"disambiguationData":[OSD([subQ3,subQ1,subQ0]),TDD([subQ4,makeQuery(id+"F4.imprint","IMPRINT",EDGE,{"disambiguationData":[TD([[makeQuery(id+"F4.imprint","INTERSECT",VERTEX,{"derivedFrom":[subQ2,sQuery(id+"F4.wireOp",EDGE,"E40.MirrorCS")]}),1.0]])],"derivedFrom":subQ2})])]}),makeQuery(id+"F5.opSweep","SWEPT_FACE",FACE,{"disambiguationData":[OSD([subQ3,subQ1,subQ0]),TDD([subQ4,makeQuery(id+"F4.imprint","IMPRINT",EDGE,{"disambiguationData":[TD([[makeQuery(id+"F4.imprint","INTERSECT",VERTEX,{"derivedFrom":[subQ2,sQuery(id+"F4.wireOp",EDGE,"E42.MirrorCS")]}),1.0]])],"derivedFrom":subQ2})])]})]})],"blendedInto":[makeQuery(id+"F5.boolean.opBoolean","MERGE",FACE,{"derivedFrom":[makeQuery(id+"F1.opExtrude","SWEPT_FACE",FACE,{"disambiguationData":[OSD([subQ1]),TDD([makeQuery(id+"F0.imprint","IMPRINT",EDGE,{"disambiguationData":[TD([[makeQuery(id+"F0.imprint","INTERSECT",VERTEX,{"derivedFrom":[subQ1,sQuery(id+"F0.wireOp",EDGE,"E14.MirrorCS")]}),1.0]])],"derivedFrom":subQ1})])]}),makeQuery(id+"F1.opExtrude","SWEPT_FACE",FACE,{"disambiguationData":[OSD([subQ1]),TDD([makeQuery(id+"F0.imprint","IMPRINT",EDGE,{"disambiguationData":[TD([[makeQuery(id+"F0.imprint","INTERSECT",VERTEX,{"derivedFrom":[subQ1,sQuery(id+"F0.wireOp",EDGE,"E12.MirrorCS")]}),1.0]])],"derivedFrom":subQ1})])]}),makeQuery(id+"F1.opExtrude","SWEPT_FACE",FACE,{"disambiguationData":[OSD([subQ1]),TDD([makeQuery(id+"F0.imprint","IMPRINT",EDGE,{"disambiguationData":[TD([[makeQuery(id+"F0.imprint","INTERSECT",VERTEX,{"derivedFrom":[subQ1,sQuery(id+"F0.wireOp",EDGE,"E3")]}),1.0]])],"derivedFrom":subQ1})])]}),makeQuery(id+"F1.opExtrude","SWEPT_FACE",FACE,{"disambiguationData":[OSD([subQ1]),TDD([makeQuery(id+"F0.imprint","IMPRINT",EDGE,{"disambiguationData":[TD([[makeQuery(id+"F0.imprint","INTERSECT",VERTEX,{"derivedFrom":[subQ1,sQuery(id+"F0.wireOp",EDGE,"E8")]}),1.0]])],"derivedFrom":subQ1})])]}),makeQuery(id+"F1.opExtrude","SWEPT_FACE",FACE,{"disambiguationData":[OSD([subQ1]),TDD([makeQuery(id+"F0.imprint","IMPRINT",EDGE,{"disambiguationData":[TD([[makeQuery(id+"F0.imprint","INTERSECT",VERTEX,{"derivedFrom":[subQ1,sQuery(id+"F0.wireOp",EDGE,"E6")]}),1.0]])],"derivedFrom":subQ1})])]}),makeQuery(id+"F1.opExtrude","SWEPT_FACE",FACE,{"disambiguationData":[OSD([subQ1]),TDD([makeQuery(id+"F0.imprint","IMPRINT",EDGE,{"disambiguationData":[TD([[makeQuery(id+"F0.imprint","INTERSECT",VERTEX,{"derivedFrom":[subQ1,sQuery(id+"F0.wireOp",EDGE,"E5")]}),-1.0]])],"derivedFrom":subQ1})])]}),makeQuery(id+"F1.opExtrude","SWEPT_FACE",FACE,{"disambiguationData":[OSD([subQ1]),TDD([makeQuery(id+"F0.imprint","IMPRINT",EDGE,{"disambiguationData":[TD([[makeQuery(id+"F0.imprint","INTERSECT",VERTEX,{"derivedFrom":[subQ1,sQuery(id+"F0.wireOp",EDGE,"E26.MirrorCS")]}),1.0]])],"derivedFrom":subQ1})])]}),makeQuery(id+"F1.opExtrude","SWEPT_FACE",FACE,{"disambiguationData":[OSD([subQ1]),TDD([makeQuery(id+"F0.imprint","IMPRINT",EDGE,{"disambiguationData":[TD([[makeQuery(id+"F0.imprint","INTERSECT",VERTEX,{"derivedFrom":[subQ1,sQuery(id+"F0.wireOp",EDGE,"E24.MirrorCS")]}),1.0]])],"derivedFrom":subQ1})])]}),makeQuery(id+"F1.opExtrude","SWEPT_FACE",FACE,{"disambiguationData":[OSD([subQ1]),TDD([makeQuery(id+"F0.imprint","IMPRINT",EDGE,{"disambiguationData":[TD([[makeQuery(id+"F0.imprint","INTERSECT",VERTEX,{"derivedFrom":[subQ1,sQuery(id+"F0.wireOp",EDGE,"E22.MirrorCS")]}),1.0]])],"derivedFrom":subQ1})])]}),makeQuery(id+"F1.opExtrude","SWEPT_FACE",FACE,{"disambiguationData":[OSD([subQ1]),TDD([makeQuery(id+"F0.imprint","IMPRINT",EDGE,{"disambiguationData":[TD([[makeQuery(id+"F0.imprint","INTERSECT",VERTEX,{"derivedFrom":[subQ1,sQuery(id+"F0.wireOp",EDGE,"E20.MirrorCS")]}),1.0]])],"derivedFrom":subQ1})])]}),makeQuery(id+"F1.opExtrude","SWEPT_FACE",FACE,{"disambiguationData":[OSD([subQ1]),TDD([makeQuery(id+"F0.imprint","IMPRINT",EDGE,{"disambiguationData":[TD([[makeQuery(id+"F0.imprint","INTERSECT",VERTEX,{"derivedFrom":[subQ1,sQuery(id+"F0.wireOp",EDGE,"E18.MirrorCS")]}),1.0]])],"derivedFrom":subQ1})])]}),makeQuery(id+"F1.opExtrude","SWEPT_FACE",FACE,{"disambiguationData":[OSD([subQ1]),TDD([makeQuery(id+"F0.imprint","IMPRINT",EDGE,{"disambiguationData":[TD([[makeQuery(id+"F0.imprint","INTERSECT",VERTEX,{"derivedFrom":[subQ1,sQuery(id+"F0.wireOp",EDGE,"E17.MirrorCS")]}),-1.0]])],"derivedFrom":subQ1})])]})],"fromTools":[makeQuery(id+"F5.opSweep","SWEPT_FACE",FACE,{"disambiguationData":[OSD([subQ3,subQ1,subQ0]),TDD([subQ4,makeQuery(id+"F4.imprint","IMPRINT",EDGE,{"disambiguationData":[TD([[makeQuery(id+"F4.imprint","INTERSECT",VERTEX,{"derivedFrom":[subQ2,sQuery(id+"F4.wireOp",EDGE,"E30")]}),1.0]])],"derivedFrom":subQ2})])]}),makeQuery(id+"F5.opSweep","SWEPT_FACE",FACE,{"disambiguationData":[OSD([subQ3,subQ1,subQ0]),TDD([subQ4,makeQuery(id+"F4.imprint","IMPRINT",EDGE,{"disambiguationData":[TD([[makeQuery(id+"F4.imprint","INTERSECT",VERTEX,{"derivedFrom":[subQ2,sQuery(id+"F4.wireOp",EDGE,"E32.MirrorCS")]}),1.0]])],"derivedFrom":subQ2})])]}),makeQuery(id+"F5.opSweep","SWEPT_FACE",FACE,{"disambiguationData":[OSD([subQ3,subQ1,subQ0]),TDD([subQ4,makeQuery(id+"F4.imprint","IMPRINT",EDGE,{"disambiguationData":[TD([[makeQuery(id+"F4.imprint","INTERSECT",VERTEX,{"derivedFrom":[subQ2,sQuery(id+"F4.wireOp",EDGE,"E34.MirrorCS")]}),1.0]])],"derivedFrom":subQ2})])]}),makeQuery(id+"F5.opSweep","SWEPT_FACE",FACE,{"disambiguationData":[OSD([subQ3,subQ1,subQ0]),TDD([subQ4,makeQuery(id+"F4.imprint","IMPRINT",EDGE,{"disambiguationData":[TD([[makeQuery(id+"F4.imprint","INTERSECT",VERTEX,{"derivedFrom":[subQ2,sQuery(id+"F4.wireOp",EDGE,"E36.MirrorCS")]}),1.0]])],"derivedFrom":subQ2})])]}),makeQuery(id+"F5.opSweep","SWEPT_FACE",FACE,{"disambiguationData":[OSD([subQ3,subQ1,subQ0]),TDD([subQ4,makeQuery(id+"F4.imprint","IMPRINT",EDGE,{"disambiguationData":[TD([[makeQuery(id+"F4.imprint","INTERSECT",VERTEX,{"derivedFrom":[subQ2,sQuery(id+"F4.wireOp",EDGE,"E38.MirrorCS")]}),1.0]])],"derivedFrom":subQ2})])]}),makeQuery(id+"F5.opSweep","SWEPT_FACE",FACE,{"disambiguationData":[OSD([subQ3,subQ1,subQ0]),TDD([subQ4,makeQuery(id+"F4.imprint","IMPRINT",EDGE,{"disambiguationData":[TD([[makeQuery(id+"F4.imprint","INTERSECT",VERTEX,{"derivedFrom":[subQ2,sQuery(id+"F4.wireOp",EDGE,"E40.MirrorCS")]}),1.0]])],"derivedFrom":subQ2})])]}),makeQuery(id+"F5.opSweep","SWEPT_FACE",FACE,{"disambiguationData":[OSD([subQ3,subQ1,subQ0]),TDD([subQ4,makeQuery(id+"F4.imprint","IMPRINT",EDGE,{"disambiguationData":[TD([[makeQuery(id+"F4.imprint","INTERSECT",VERTEX,{"derivedFrom":[subQ2,sQuery(id+"F4.wireOp",EDGE,"E42.MirrorCS")]}),1.0]])],"derivedFrom":subQ2})])]})]})]});}
            var Q12;
            {var subQ0=sQuery(id+"F0.wireOp",EDGE,"E7");var subQ2=sQuery(id+"F2.wireOp",EDGE,"E29");var subQ3=sQuery(id+"F0.wireOp",EDGE,"E2");Q12=makeQuery(id+"F8.opFillet","BLEND_EDGE",EDGE,{"blendedFrom":[makeQuery(id+"F3.opExtrude","CAP_EDGE",EDGE,{"disambiguationData":[OSD([subQ2])],"isStart":true}),makeQuery(id+"F5.boolean.opBoolean","SPLIT",FACE,{"disambiguationData":[TD([makeQuery(id+"F3.opExtrude","CAP_FACE",FACE,{"disambiguationData":[OSD([subQ2])],"isStart":true})])],"derivedFrom":makeQuery(id+"F1.opExtrude","SWEPT_FACE",FACE,{"disambiguationData":[OSD([subQ3]),TDD([makeQuery(id+"F0.imprint","IMPRINT",EDGE,{"disambiguationData":[TD([[makeQuery(id+"F0.imprint","INTERSECT",VERTEX,{"derivedFrom":[subQ3,subQ0]}),1.0]])],"derivedFrom":subQ3})])]})})],"blendedInto":[makeQuery(id+"F5.boolean.opBoolean","SPLIT",FACE,{"disambiguationData":[TD([makeQuery(id+"F3.opExtrude","CAP_FACE",FACE,{"disambiguationData":[OSD([subQ2])],"isStart":true})])],"derivedFrom":makeQuery(id+"F1.opExtrude","SWEPT_FACE",FACE,{"disambiguationData":[OSD([subQ3]),TDD([makeQuery(id+"F0.imprint","IMPRINT",EDGE,{"disambiguationData":[TD([[makeQuery(id+"F0.imprint","INTERSECT",VERTEX,{"derivedFrom":[subQ3,subQ0]}),1.0]])],"derivedFrom":subQ3})])]})})]});}
            var Q13;
            {var subQ0=sQuery(id+"F0.wireOp",EDGE,"E27.MirrorCS");var subQ1=sQuery(id+"F0.wireOp",EDGE,"E1");var subQ2=makeQuery(id+"F1.opExtrude","SWEPT_EDGE",EDGE,{"disambiguationData":[OSD([subQ1,subQ0])]});var subQ3=sQuery(id+"F0.wireOp",EDGE,"E0");var subQ4=makeQuery(id+"F1.opExtrude","CAP_EDGE",EDGE,{"disambiguationData":[OSD([subQ3])],"isStart":true});Q13=makeQuery(id+"F8.opFillet","BLEND_EDGE",EDGE,{"disambiguationData":[OD(2.0)],"blendedFrom":[makeQuery(id+"F3.opExtrude","CAP_EDGE",EDGE,{"disambiguationData":[OSD([sQuery(id+"F2.wireOp",EDGE,"E29")])],"isStart":true}),makeQuery(id+"F5.boolean.opBoolean","MERGE",FACE,{"derivedFrom":[makeQuery(id+"F1.opExtrude","SWEPT_FACE",FACE,{"disambiguationData":[OSD([subQ1]),TDD([makeQuery(id+"F0.imprint","IMPRINT",EDGE,{"disambiguationData":[TD([[makeQuery(id+"F0.imprint","INTERSECT",VERTEX,{"derivedFrom":[subQ1,sQuery(id+"F0.wireOp",EDGE,"E14.MirrorCS")]}),1.0]])],"derivedFrom":subQ1})])]}),makeQuery(id+"F1.opExtrude","SWEPT_FACE",FACE,{"disambiguationData":[OSD([subQ1]),TDD([makeQuery(id+"F0.imprint","IMPRINT",EDGE,{"disambiguationData":[TD([[makeQuery(id+"F0.imprint","INTERSECT",VERTEX,{"derivedFrom":[subQ1,sQuery(id+"F0.wireOp",EDGE,"E12.MirrorCS")]}),1.0]])],"derivedFrom":subQ1})])]}),makeQuery(id+"F1.opExtrude","SWEPT_FACE",FACE,{"disambiguationData":[OSD([subQ1]),TDD([makeQuery(id+"F0.imprint","IMPRINT",EDGE,{"disambiguationData":[TD([[makeQuery(id+"F0.imprint","INTERSECT",VERTEX,{"derivedFrom":[subQ1,sQuery(id+"F0.wireOp",EDGE,"E3")]}),1.0]])],"derivedFrom":subQ1})])]}),makeQuery(id+"F1.opExtrude","SWEPT_FACE",FACE,{"disambiguationData":[OSD([subQ1]),TDD([makeQuery(id+"F0.imprint","IMPRINT",EDGE,{"disambiguationData":[TD([[makeQuery(id+"F0.imprint","INTERSECT",VERTEX,{"derivedFrom":[subQ1,sQuery(id+"F0.wireOp",EDGE,"E8")]}),1.0]])],"derivedFrom":subQ1})])]}),makeQuery(id+"F1.opExtrude","SWEPT_FACE",FACE,{"disambiguationData":[OSD([subQ1]),TDD([makeQuery(id+"F0.imprint","IMPRINT",EDGE,{"disambiguationData":[TD([[makeQuery(id+"F0.imprint","INTERSECT",VERTEX,{"derivedFrom":[subQ1,sQuery(id+"F0.wireOp",EDGE,"E6")]}),1.0]])],"derivedFrom":subQ1})])]}),makeQuery(id+"F1.opExtrude","SWEPT_FACE",FACE,{"disambiguationData":[OSD([subQ1]),TDD([makeQuery(id+"F0.imprint","IMPRINT",EDGE,{"disambiguationData":[TD([[makeQuery(id+"F0.imprint","INTERSECT",VERTEX,{"derivedFrom":[subQ1,sQuery(id+"F0.wireOp",EDGE,"E5")]}),-1.0]])],"derivedFrom":subQ1})])]}),makeQuery(id+"F1.opExtrude","SWEPT_FACE",FACE,{"disambiguationData":[OSD([subQ1]),TDD([makeQuery(id+"F0.imprint","IMPRINT",EDGE,{"disambiguationData":[TD([[makeQuery(id+"F0.imprint","INTERSECT",VERTEX,{"derivedFrom":[subQ1,sQuery(id+"F0.wireOp",EDGE,"E26.MirrorCS")]}),1.0]])],"derivedFrom":subQ1})])]}),makeQuery(id+"F1.opExtrude","SWEPT_FACE",FACE,{"disambiguationData":[OSD([subQ1]),TDD([makeQuery(id+"F0.imprint","IMPRINT",EDGE,{"disambiguationData":[TD([[makeQuery(id+"F0.imprint","INTERSECT",VERTEX,{"derivedFrom":[subQ1,sQuery(id+"F0.wireOp",EDGE,"E24.MirrorCS")]}),1.0]])],"derivedFrom":subQ1})])]}),makeQuery(id+"F1.opExtrude","SWEPT_FACE",FACE,{"disambiguationData":[OSD([subQ1]),TDD([makeQuery(id+"F0.imprint","IMPRINT",EDGE,{"disambiguationData":[TD([[makeQuery(id+"F0.imprint","INTERSECT",VERTEX,{"derivedFrom":[subQ1,sQuery(id+"F0.wireOp",EDGE,"E22.MirrorCS")]}),1.0]])],"derivedFrom":subQ1})])]}),makeQuery(id+"F1.opExtrude","SWEPT_FACE",FACE,{"disambiguationData":[OSD([subQ1]),TDD([makeQuery(id+"F0.imprint","IMPRINT",EDGE,{"disambiguationData":[TD([[makeQuery(id+"F0.imprint","INTERSECT",VERTEX,{"derivedFrom":[subQ1,sQuery(id+"F0.wireOp",EDGE,"E20.MirrorCS")]}),1.0]])],"derivedFrom":subQ1})])]}),makeQuery(id+"F1.opExtrude","SWEPT_FACE",FACE,{"disambiguationData":[OSD([subQ1]),TDD([makeQuery(id+"F0.imprint","IMPRINT",EDGE,{"disambiguationData":[TD([[makeQuery(id+"F0.imprint","INTERSECT",VERTEX,{"derivedFrom":[subQ1,sQuery(id+"F0.wireOp",EDGE,"E18.MirrorCS")]}),1.0]])],"derivedFrom":subQ1})])]}),makeQuery(id+"F1.opExtrude","SWEPT_FACE",FACE,{"disambiguationData":[OSD([subQ1]),TDD([makeQuery(id+"F0.imprint","IMPRINT",EDGE,{"disambiguationData":[TD([[makeQuery(id+"F0.imprint","INTERSECT",VERTEX,{"derivedFrom":[subQ1,sQuery(id+"F0.wireOp",EDGE,"E17.MirrorCS")]}),-1.0]])],"derivedFrom":subQ1})])]})],"fromTools":[makeQuery(id+"F5.opSweep","SWEPT_FACE",FACE,{"disambiguationData":[OSD([subQ3,subQ1,subQ0]),TDD([subQ4,makeQuery(id+"F4.imprint","IMPRINT",EDGE,{"disambiguationData":[TD([[makeQuery(id+"F4.imprint","INTERSECT",VERTEX,{"derivedFrom":[subQ2,sQuery(id+"F4.wireOp",EDGE,"E30")]}),1.0]])],"derivedFrom":subQ2})])]}),makeQuery(id+"F5.opSweep","SWEPT_FACE",FACE,{"disambiguationData":[OSD([subQ3,subQ1,subQ0]),TDD([subQ4,makeQuery(id+"F4.imprint","IMPRINT",EDGE,{"disambiguationData":[TD([[makeQuery(id+"F4.imprint","INTERSECT",VERTEX,{"derivedFrom":[subQ2,sQuery(id+"F4.wireOp",EDGE,"E32.MirrorCS")]}),1.0]])],"derivedFrom":subQ2})])]}),makeQuery(id+"F5.opSweep","SWEPT_FACE",FACE,{"disambiguationData":[OSD([subQ3,subQ1,subQ0]),TDD([subQ4,makeQuery(id+"F4.imprint","IMPRINT",EDGE,{"disambiguationData":[TD([[makeQuery(id+"F4.imprint","INTERSECT",VERTEX,{"derivedFrom":[subQ2,sQuery(id+"F4.wireOp",EDGE,"E34.MirrorCS")]}),1.0]])],"derivedFrom":subQ2})])]}),makeQuery(id+"F5.opSweep","SWEPT_FACE",FACE,{"disambiguationData":[OSD([subQ3,subQ1,subQ0]),TDD([subQ4,makeQuery(id+"F4.imprint","IMPRINT",EDGE,{"disambiguationData":[TD([[makeQuery(id+"F4.imprint","INTERSECT",VERTEX,{"derivedFrom":[subQ2,sQuery(id+"F4.wireOp",EDGE,"E36.MirrorCS")]}),1.0]])],"derivedFrom":subQ2})])]}),makeQuery(id+"F5.opSweep","SWEPT_FACE",FACE,{"disambiguationData":[OSD([subQ3,subQ1,subQ0]),TDD([subQ4,makeQuery(id+"F4.imprint","IMPRINT",EDGE,{"disambiguationData":[TD([[makeQuery(id+"F4.imprint","INTERSECT",VERTEX,{"derivedFrom":[subQ2,sQuery(id+"F4.wireOp",EDGE,"E38.MirrorCS")]}),1.0]])],"derivedFrom":subQ2})])]}),makeQuery(id+"F5.opSweep","SWEPT_FACE",FACE,{"disambiguationData":[OSD([subQ3,subQ1,subQ0]),TDD([subQ4,makeQuery(id+"F4.imprint","IMPRINT",EDGE,{"disambiguationData":[TD([[makeQuery(id+"F4.imprint","INTERSECT",VERTEX,{"derivedFrom":[subQ2,sQuery(id+"F4.wireOp",EDGE,"E40.MirrorCS")]}),1.0]])],"derivedFrom":subQ2})])]}),makeQuery(id+"F5.opSweep","SWEPT_FACE",FACE,{"disambiguationData":[OSD([subQ3,subQ1,subQ0]),TDD([subQ4,makeQuery(id+"F4.imprint","IMPRINT",EDGE,{"disambiguationData":[TD([[makeQuery(id+"F4.imprint","INTERSECT",VERTEX,{"derivedFrom":[subQ2,sQuery(id+"F4.wireOp",EDGE,"E42.MirrorCS")]}),1.0]])],"derivedFrom":subQ2})])]})]})],"blendedInto":[makeQuery(id+"F5.boolean.opBoolean","MERGE",FACE,{"derivedFrom":[makeQuery(id+"F1.opExtrude","SWEPT_FACE",FACE,{"disambiguationData":[OSD([subQ1]),TDD([makeQuery(id+"F0.imprint","IMPRINT",EDGE,{"disambiguationData":[TD([[makeQuery(id+"F0.imprint","INTERSECT",VERTEX,{"derivedFrom":[subQ1,sQuery(id+"F0.wireOp",EDGE,"E14.MirrorCS")]}),1.0]])],"derivedFrom":subQ1})])]}),makeQuery(id+"F1.opExtrude","SWEPT_FACE",FACE,{"disambiguationData":[OSD([subQ1]),TDD([makeQuery(id+"F0.imprint","IMPRINT",EDGE,{"disambiguationData":[TD([[makeQuery(id+"F0.imprint","INTERSECT",VERTEX,{"derivedFrom":[subQ1,sQuery(id+"F0.wireOp",EDGE,"E12.MirrorCS")]}),1.0]])],"derivedFrom":subQ1})])]}),makeQuery(id+"F1.opExtrude","SWEPT_FACE",FACE,{"disambiguationData":[OSD([subQ1]),TDD([makeQuery(id+"F0.imprint","IMPRINT",EDGE,{"disambiguationData":[TD([[makeQuery(id+"F0.imprint","INTERSECT",VERTEX,{"derivedFrom":[subQ1,sQuery(id+"F0.wireOp",EDGE,"E3")]}),1.0]])],"derivedFrom":subQ1})])]}),makeQuery(id+"F1.opExtrude","SWEPT_FACE",FACE,{"disambiguationData":[OSD([subQ1]),TDD([makeQuery(id+"F0.imprint","IMPRINT",EDGE,{"disambiguationData":[TD([[makeQuery(id+"F0.imprint","INTERSECT",VERTEX,{"derivedFrom":[subQ1,sQuery(id+"F0.wireOp",EDGE,"E8")]}),1.0]])],"derivedFrom":subQ1})])]}),makeQuery(id+"F1.opExtrude","SWEPT_FACE",FACE,{"disambiguationData":[OSD([subQ1]),TDD([makeQuery(id+"F0.imprint","IMPRINT",EDGE,{"disambiguationData":[TD([[makeQuery(id+"F0.imprint","INTERSECT",VERTEX,{"derivedFrom":[subQ1,sQuery(id+"F0.wireOp",EDGE,"E6")]}),1.0]])],"derivedFrom":subQ1})])]}),makeQuery(id+"F1.opExtrude","SWEPT_FACE",FACE,{"disambiguationData":[OSD([subQ1]),TDD([makeQuery(id+"F0.imprint","IMPRINT",EDGE,{"disambiguationData":[TD([[makeQuery(id+"F0.imprint","INTERSECT",VERTEX,{"derivedFrom":[subQ1,sQuery(id+"F0.wireOp",EDGE,"E5")]}),-1.0]])],"derivedFrom":subQ1})])]}),makeQuery(id+"F1.opExtrude","SWEPT_FACE",FACE,{"disambiguationData":[OSD([subQ1]),TDD([makeQuery(id+"F0.imprint","IMPRINT",EDGE,{"disambiguationData":[TD([[makeQuery(id+"F0.imprint","INTERSECT",VERTEX,{"derivedFrom":[subQ1,sQuery(id+"F0.wireOp",EDGE,"E26.MirrorCS")]}),1.0]])],"derivedFrom":subQ1})])]}),makeQuery(id+"F1.opExtrude","SWEPT_FACE",FACE,{"disambiguationData":[OSD([subQ1]),TDD([makeQuery(id+"F0.imprint","IMPRINT",EDGE,{"disambiguationData":[TD([[makeQuery(id+"F0.imprint","INTERSECT",VERTEX,{"derivedFrom":[subQ1,sQuery(id+"F0.wireOp",EDGE,"E24.MirrorCS")]}),1.0]])],"derivedFrom":subQ1})])]}),makeQuery(id+"F1.opExtrude","SWEPT_FACE",FACE,{"disambiguationData":[OSD([subQ1]),TDD([makeQuery(id+"F0.imprint","IMPRINT",EDGE,{"disambiguationData":[TD([[makeQuery(id+"F0.imprint","INTERSECT",VERTEX,{"derivedFrom":[subQ1,sQuery(id+"F0.wireOp",EDGE,"E22.MirrorCS")]}),1.0]])],"derivedFrom":subQ1})])]}),makeQuery(id+"F1.opExtrude","SWEPT_FACE",FACE,{"disambiguationData":[OSD([subQ1]),TDD([makeQuery(id+"F0.imprint","IMPRINT",EDGE,{"disambiguationData":[TD([[makeQuery(id+"F0.imprint","INTERSECT",VERTEX,{"derivedFrom":[subQ1,sQuery(id+"F0.wireOp",EDGE,"E20.MirrorCS")]}),1.0]])],"derivedFrom":subQ1})])]}),makeQuery(id+"F1.opExtrude","SWEPT_FACE",FACE,{"disambiguationData":[OSD([subQ1]),TDD([makeQuery(id+"F0.imprint","IMPRINT",EDGE,{"disambiguationData":[TD([[makeQuery(id+"F0.imprint","INTERSECT",VERTEX,{"derivedFrom":[subQ1,sQuery(id+"F0.wireOp",EDGE,"E18.MirrorCS")]}),1.0]])],"derivedFrom":subQ1})])]}),makeQuery(id+"F1.opExtrude","SWEPT_FACE",FACE,{"disambiguationData":[OSD([subQ1]),TDD([makeQuery(id+"F0.imprint","IMPRINT",EDGE,{"disambiguationData":[TD([[makeQuery(id+"F0.imprint","INTERSECT",VERTEX,{"derivedFrom":[subQ1,sQuery(id+"F0.wireOp",EDGE,"E17.MirrorCS")]}),-1.0]])],"derivedFrom":subQ1})])]})],"fromTools":[makeQuery(id+"F5.opSweep","SWEPT_FACE",FACE,{"disambiguationData":[OSD([subQ3,subQ1,subQ0]),TDD([subQ4,makeQuery(id+"F4.imprint","IMPRINT",EDGE,{"disambiguationData":[TD([[makeQuery(id+"F4.imprint","INTERSECT",VERTEX,{"derivedFrom":[subQ2,sQuery(id+"F4.wireOp",EDGE,"E30")]}),1.0]])],"derivedFrom":subQ2})])]}),makeQuery(id+"F5.opSweep","SWEPT_FACE",FACE,{"disambiguationData":[OSD([subQ3,subQ1,subQ0]),TDD([subQ4,makeQuery(id+"F4.imprint","IMPRINT",EDGE,{"disambiguationData":[TD([[makeQuery(id+"F4.imprint","INTERSECT",VERTEX,{"derivedFrom":[subQ2,sQuery(id+"F4.wireOp",EDGE,"E32.MirrorCS")]}),1.0]])],"derivedFrom":subQ2})])]}),makeQuery(id+"F5.opSweep","SWEPT_FACE",FACE,{"disambiguationData":[OSD([subQ3,subQ1,subQ0]),TDD([subQ4,makeQuery(id+"F4.imprint","IMPRINT",EDGE,{"disambiguationData":[TD([[makeQuery(id+"F4.imprint","INTERSECT",VERTEX,{"derivedFrom":[subQ2,sQuery(id+"F4.wireOp",EDGE,"E34.MirrorCS")]}),1.0]])],"derivedFrom":subQ2})])]}),makeQuery(id+"F5.opSweep","SWEPT_FACE",FACE,{"disambiguationData":[OSD([subQ3,subQ1,subQ0]),TDD([subQ4,makeQuery(id+"F4.imprint","IMPRINT",EDGE,{"disambiguationData":[TD([[makeQuery(id+"F4.imprint","INTERSECT",VERTEX,{"derivedFrom":[subQ2,sQuery(id+"F4.wireOp",EDGE,"E36.MirrorCS")]}),1.0]])],"derivedFrom":subQ2})])]}),makeQuery(id+"F5.opSweep","SWEPT_FACE",FACE,{"disambiguationData":[OSD([subQ3,subQ1,subQ0]),TDD([subQ4,makeQuery(id+"F4.imprint","IMPRINT",EDGE,{"disambiguationData":[TD([[makeQuery(id+"F4.imprint","INTERSECT",VERTEX,{"derivedFrom":[subQ2,sQuery(id+"F4.wireOp",EDGE,"E38.MirrorCS")]}),1.0]])],"derivedFrom":subQ2})])]}),makeQuery(id+"F5.opSweep","SWEPT_FACE",FACE,{"disambiguationData":[OSD([subQ3,subQ1,subQ0]),TDD([subQ4,makeQuery(id+"F4.imprint","IMPRINT",EDGE,{"disambiguationData":[TD([[makeQuery(id+"F4.imprint","INTERSECT",VERTEX,{"derivedFrom":[subQ2,sQuery(id+"F4.wireOp",EDGE,"E40.MirrorCS")]}),1.0]])],"derivedFrom":subQ2})])]}),makeQuery(id+"F5.opSweep","SWEPT_FACE",FACE,{"disambiguationData":[OSD([subQ3,subQ1,subQ0]),TDD([subQ4,makeQuery(id+"F4.imprint","IMPRINT",EDGE,{"disambiguationData":[TD([[makeQuery(id+"F4.imprint","INTERSECT",VERTEX,{"derivedFrom":[subQ2,sQuery(id+"F4.wireOp",EDGE,"E42.MirrorCS")]}),1.0]])],"derivedFrom":subQ2})])]})]})]});}
            var Q14;
            {var subQ0=sQuery(id+"F0.wireOp",EDGE,"E5");var subQ2=sQuery(id+"F2.wireOp",EDGE,"E29");var subQ3=sQuery(id+"F0.wireOp",EDGE,"E2");Q14=makeQuery(id+"F8.opFillet","BLEND_EDGE",EDGE,{"blendedFrom":[makeQuery(id+"F3.opExtrude","CAP_EDGE",EDGE,{"disambiguationData":[OSD([subQ2])],"isStart":true}),makeQuery(id+"F5.boolean.opBoolean","SPLIT",FACE,{"disambiguationData":[TD([makeQuery(id+"F3.opExtrude","CAP_FACE",FACE,{"disambiguationData":[OSD([subQ2])],"isStart":true})])],"derivedFrom":makeQuery(id+"F1.opExtrude","SWEPT_FACE",FACE,{"disambiguationData":[OSD([subQ3]),TDD([makeQuery(id+"F0.imprint","IMPRINT",EDGE,{"disambiguationData":[TD([[makeQuery(id+"F0.imprint","INTERSECT",VERTEX,{"derivedFrom":[subQ3,subQ0]}),1.0]])],"derivedFrom":subQ3})])]})})],"blendedInto":[makeQuery(id+"F5.boolean.opBoolean","SPLIT",FACE,{"disambiguationData":[TD([makeQuery(id+"F3.opExtrude","CAP_FACE",FACE,{"disambiguationData":[OSD([subQ2])],"isStart":true})])],"derivedFrom":makeQuery(id+"F1.opExtrude","SWEPT_FACE",FACE,{"disambiguationData":[OSD([subQ3]),TDD([makeQuery(id+"F0.imprint","IMPRINT",EDGE,{"disambiguationData":[TD([[makeQuery(id+"F0.imprint","INTERSECT",VERTEX,{"derivedFrom":[subQ3,subQ0]}),1.0]])],"derivedFrom":subQ3})])]})})]});}
            var Q15;
            {var subQ0=sQuery(id+"F0.wireOp",EDGE,"E27.MirrorCS");var subQ1=sQuery(id+"F0.wireOp",EDGE,"E1");var subQ2=makeQuery(id+"F1.opExtrude","SWEPT_EDGE",EDGE,{"disambiguationData":[OSD([subQ1,subQ0])]});var subQ3=sQuery(id+"F0.wireOp",EDGE,"E0");var subQ4=makeQuery(id+"F1.opExtrude","CAP_EDGE",EDGE,{"disambiguationData":[OSD([subQ3])],"isStart":true});Q15=makeQuery(id+"F8.opFillet","BLEND_EDGE",EDGE,{"disambiguationData":[OD(1.0)],"blendedFrom":[makeQuery(id+"F3.opExtrude","CAP_EDGE",EDGE,{"disambiguationData":[OSD([sQuery(id+"F2.wireOp",EDGE,"E29")])],"isStart":true}),makeQuery(id+"F5.boolean.opBoolean","MERGE",FACE,{"derivedFrom":[makeQuery(id+"F1.opExtrude","SWEPT_FACE",FACE,{"disambiguationData":[OSD([subQ1]),TDD([makeQuery(id+"F0.imprint","IMPRINT",EDGE,{"disambiguationData":[TD([[makeQuery(id+"F0.imprint","INTERSECT",VERTEX,{"derivedFrom":[subQ1,sQuery(id+"F0.wireOp",EDGE,"E14.MirrorCS")]}),1.0]])],"derivedFrom":subQ1})])]}),makeQuery(id+"F1.opExtrude","SWEPT_FACE",FACE,{"disambiguationData":[OSD([subQ1]),TDD([makeQuery(id+"F0.imprint","IMPRINT",EDGE,{"disambiguationData":[TD([[makeQuery(id+"F0.imprint","INTERSECT",VERTEX,{"derivedFrom":[subQ1,sQuery(id+"F0.wireOp",EDGE,"E12.MirrorCS")]}),1.0]])],"derivedFrom":subQ1})])]}),makeQuery(id+"F1.opExtrude","SWEPT_FACE",FACE,{"disambiguationData":[OSD([subQ1]),TDD([makeQuery(id+"F0.imprint","IMPRINT",EDGE,{"disambiguationData":[TD([[makeQuery(id+"F0.imprint","INTERSECT",VERTEX,{"derivedFrom":[subQ1,sQuery(id+"F0.wireOp",EDGE,"E3")]}),1.0]])],"derivedFrom":subQ1})])]}),makeQuery(id+"F1.opExtrude","SWEPT_FACE",FACE,{"disambiguationData":[OSD([subQ1]),TDD([makeQuery(id+"F0.imprint","IMPRINT",EDGE,{"disambiguationData":[TD([[makeQuery(id+"F0.imprint","INTERSECT",VERTEX,{"derivedFrom":[subQ1,sQuery(id+"F0.wireOp",EDGE,"E8")]}),1.0]])],"derivedFrom":subQ1})])]}),makeQuery(id+"F1.opExtrude","SWEPT_FACE",FACE,{"disambiguationData":[OSD([subQ1]),TDD([makeQuery(id+"F0.imprint","IMPRINT",EDGE,{"disambiguationData":[TD([[makeQuery(id+"F0.imprint","INTERSECT",VERTEX,{"derivedFrom":[subQ1,sQuery(id+"F0.wireOp",EDGE,"E6")]}),1.0]])],"derivedFrom":subQ1})])]}),makeQuery(id+"F1.opExtrude","SWEPT_FACE",FACE,{"disambiguationData":[OSD([subQ1]),TDD([makeQuery(id+"F0.imprint","IMPRINT",EDGE,{"disambiguationData":[TD([[makeQuery(id+"F0.imprint","INTERSECT",VERTEX,{"derivedFrom":[subQ1,sQuery(id+"F0.wireOp",EDGE,"E5")]}),-1.0]])],"derivedFrom":subQ1})])]}),makeQuery(id+"F1.opExtrude","SWEPT_FACE",FACE,{"disambiguationData":[OSD([subQ1]),TDD([makeQuery(id+"F0.imprint","IMPRINT",EDGE,{"disambiguationData":[TD([[makeQuery(id+"F0.imprint","INTERSECT",VERTEX,{"derivedFrom":[subQ1,sQuery(id+"F0.wireOp",EDGE,"E26.MirrorCS")]}),1.0]])],"derivedFrom":subQ1})])]}),makeQuery(id+"F1.opExtrude","SWEPT_FACE",FACE,{"disambiguationData":[OSD([subQ1]),TDD([makeQuery(id+"F0.imprint","IMPRINT",EDGE,{"disambiguationData":[TD([[makeQuery(id+"F0.imprint","INTERSECT",VERTEX,{"derivedFrom":[subQ1,sQuery(id+"F0.wireOp",EDGE,"E24.MirrorCS")]}),1.0]])],"derivedFrom":subQ1})])]}),makeQuery(id+"F1.opExtrude","SWEPT_FACE",FACE,{"disambiguationData":[OSD([subQ1]),TDD([makeQuery(id+"F0.imprint","IMPRINT",EDGE,{"disambiguationData":[TD([[makeQuery(id+"F0.imprint","INTERSECT",VERTEX,{"derivedFrom":[subQ1,sQuery(id+"F0.wireOp",EDGE,"E22.MirrorCS")]}),1.0]])],"derivedFrom":subQ1})])]}),makeQuery(id+"F1.opExtrude","SWEPT_FACE",FACE,{"disambiguationData":[OSD([subQ1]),TDD([makeQuery(id+"F0.imprint","IMPRINT",EDGE,{"disambiguationData":[TD([[makeQuery(id+"F0.imprint","INTERSECT",VERTEX,{"derivedFrom":[subQ1,sQuery(id+"F0.wireOp",EDGE,"E20.MirrorCS")]}),1.0]])],"derivedFrom":subQ1})])]}),makeQuery(id+"F1.opExtrude","SWEPT_FACE",FACE,{"disambiguationData":[OSD([subQ1]),TDD([makeQuery(id+"F0.imprint","IMPRINT",EDGE,{"disambiguationData":[TD([[makeQuery(id+"F0.imprint","INTERSECT",VERTEX,{"derivedFrom":[subQ1,sQuery(id+"F0.wireOp",EDGE,"E18.MirrorCS")]}),1.0]])],"derivedFrom":subQ1})])]}),makeQuery(id+"F1.opExtrude","SWEPT_FACE",FACE,{"disambiguationData":[OSD([subQ1]),TDD([makeQuery(id+"F0.imprint","IMPRINT",EDGE,{"disambiguationData":[TD([[makeQuery(id+"F0.imprint","INTERSECT",VERTEX,{"derivedFrom":[subQ1,sQuery(id+"F0.wireOp",EDGE,"E17.MirrorCS")]}),-1.0]])],"derivedFrom":subQ1})])]})],"fromTools":[makeQuery(id+"F5.opSweep","SWEPT_FACE",FACE,{"disambiguationData":[OSD([subQ3,subQ1,subQ0]),TDD([subQ4,makeQuery(id+"F4.imprint","IMPRINT",EDGE,{"disambiguationData":[TD([[makeQuery(id+"F4.imprint","INTERSECT",VERTEX,{"derivedFrom":[subQ2,sQuery(id+"F4.wireOp",EDGE,"E30")]}),1.0]])],"derivedFrom":subQ2})])]}),makeQuery(id+"F5.opSweep","SWEPT_FACE",FACE,{"disambiguationData":[OSD([subQ3,subQ1,subQ0]),TDD([subQ4,makeQuery(id+"F4.imprint","IMPRINT",EDGE,{"disambiguationData":[TD([[makeQuery(id+"F4.imprint","INTERSECT",VERTEX,{"derivedFrom":[subQ2,sQuery(id+"F4.wireOp",EDGE,"E32.MirrorCS")]}),1.0]])],"derivedFrom":subQ2})])]}),makeQuery(id+"F5.opSweep","SWEPT_FACE",FACE,{"disambiguationData":[OSD([subQ3,subQ1,subQ0]),TDD([subQ4,makeQuery(id+"F4.imprint","IMPRINT",EDGE,{"disambiguationData":[TD([[makeQuery(id+"F4.imprint","INTERSECT",VERTEX,{"derivedFrom":[subQ2,sQuery(id+"F4.wireOp",EDGE,"E34.MirrorCS")]}),1.0]])],"derivedFrom":subQ2})])]}),makeQuery(id+"F5.opSweep","SWEPT_FACE",FACE,{"disambiguationData":[OSD([subQ3,subQ1,subQ0]),TDD([subQ4,makeQuery(id+"F4.imprint","IMPRINT",EDGE,{"disambiguationData":[TD([[makeQuery(id+"F4.imprint","INTERSECT",VERTEX,{"derivedFrom":[subQ2,sQuery(id+"F4.wireOp",EDGE,"E36.MirrorCS")]}),1.0]])],"derivedFrom":subQ2})])]}),makeQuery(id+"F5.opSweep","SWEPT_FACE",FACE,{"disambiguationData":[OSD([subQ3,subQ1,subQ0]),TDD([subQ4,makeQuery(id+"F4.imprint","IMPRINT",EDGE,{"disambiguationData":[TD([[makeQuery(id+"F4.imprint","INTERSECT",VERTEX,{"derivedFrom":[subQ2,sQuery(id+"F4.wireOp",EDGE,"E38.MirrorCS")]}),1.0]])],"derivedFrom":subQ2})])]}),makeQuery(id+"F5.opSweep","SWEPT_FACE",FACE,{"disambiguationData":[OSD([subQ3,subQ1,subQ0]),TDD([subQ4,makeQuery(id+"F4.imprint","IMPRINT",EDGE,{"disambiguationData":[TD([[makeQuery(id+"F4.imprint","INTERSECT",VERTEX,{"derivedFrom":[subQ2,sQuery(id+"F4.wireOp",EDGE,"E40.MirrorCS")]}),1.0]])],"derivedFrom":subQ2})])]}),makeQuery(id+"F5.opSweep","SWEPT_FACE",FACE,{"disambiguationData":[OSD([subQ3,subQ1,subQ0]),TDD([subQ4,makeQuery(id+"F4.imprint","IMPRINT",EDGE,{"disambiguationData":[TD([[makeQuery(id+"F4.imprint","INTERSECT",VERTEX,{"derivedFrom":[subQ2,sQuery(id+"F4.wireOp",EDGE,"E42.MirrorCS")]}),1.0]])],"derivedFrom":subQ2})])]})]})],"blendedInto":[makeQuery(id+"F5.boolean.opBoolean","MERGE",FACE,{"derivedFrom":[makeQuery(id+"F1.opExtrude","SWEPT_FACE",FACE,{"disambiguationData":[OSD([subQ1]),TDD([makeQuery(id+"F0.imprint","IMPRINT",EDGE,{"disambiguationData":[TD([[makeQuery(id+"F0.imprint","INTERSECT",VERTEX,{"derivedFrom":[subQ1,sQuery(id+"F0.wireOp",EDGE,"E14.MirrorCS")]}),1.0]])],"derivedFrom":subQ1})])]}),makeQuery(id+"F1.opExtrude","SWEPT_FACE",FACE,{"disambiguationData":[OSD([subQ1]),TDD([makeQuery(id+"F0.imprint","IMPRINT",EDGE,{"disambiguationData":[TD([[makeQuery(id+"F0.imprint","INTERSECT",VERTEX,{"derivedFrom":[subQ1,sQuery(id+"F0.wireOp",EDGE,"E12.MirrorCS")]}),1.0]])],"derivedFrom":subQ1})])]}),makeQuery(id+"F1.opExtrude","SWEPT_FACE",FACE,{"disambiguationData":[OSD([subQ1]),TDD([makeQuery(id+"F0.imprint","IMPRINT",EDGE,{"disambiguationData":[TD([[makeQuery(id+"F0.imprint","INTERSECT",VERTEX,{"derivedFrom":[subQ1,sQuery(id+"F0.wireOp",EDGE,"E3")]}),1.0]])],"derivedFrom":subQ1})])]}),makeQuery(id+"F1.opExtrude","SWEPT_FACE",FACE,{"disambiguationData":[OSD([subQ1]),TDD([makeQuery(id+"F0.imprint","IMPRINT",EDGE,{"disambiguationData":[TD([[makeQuery(id+"F0.imprint","INTERSECT",VERTEX,{"derivedFrom":[subQ1,sQuery(id+"F0.wireOp",EDGE,"E8")]}),1.0]])],"derivedFrom":subQ1})])]}),makeQuery(id+"F1.opExtrude","SWEPT_FACE",FACE,{"disambiguationData":[OSD([subQ1]),TDD([makeQuery(id+"F0.imprint","IMPRINT",EDGE,{"disambiguationData":[TD([[makeQuery(id+"F0.imprint","INTERSECT",VERTEX,{"derivedFrom":[subQ1,sQuery(id+"F0.wireOp",EDGE,"E6")]}),1.0]])],"derivedFrom":subQ1})])]}),makeQuery(id+"F1.opExtrude","SWEPT_FACE",FACE,{"disambiguationData":[OSD([subQ1]),TDD([makeQuery(id+"F0.imprint","IMPRINT",EDGE,{"disambiguationData":[TD([[makeQuery(id+"F0.imprint","INTERSECT",VERTEX,{"derivedFrom":[subQ1,sQuery(id+"F0.wireOp",EDGE,"E5")]}),-1.0]])],"derivedFrom":subQ1})])]}),makeQuery(id+"F1.opExtrude","SWEPT_FACE",FACE,{"disambiguationData":[OSD([subQ1]),TDD([makeQuery(id+"F0.imprint","IMPRINT",EDGE,{"disambiguationData":[TD([[makeQuery(id+"F0.imprint","INTERSECT",VERTEX,{"derivedFrom":[subQ1,sQuery(id+"F0.wireOp",EDGE,"E26.MirrorCS")]}),1.0]])],"derivedFrom":subQ1})])]}),makeQuery(id+"F1.opExtrude","SWEPT_FACE",FACE,{"disambiguationData":[OSD([subQ1]),TDD([makeQuery(id+"F0.imprint","IMPRINT",EDGE,{"disambiguationData":[TD([[makeQuery(id+"F0.imprint","INTERSECT",VERTEX,{"derivedFrom":[subQ1,sQuery(id+"F0.wireOp",EDGE,"E24.MirrorCS")]}),1.0]])],"derivedFrom":subQ1})])]}),makeQuery(id+"F1.opExtrude","SWEPT_FACE",FACE,{"disambiguationData":[OSD([subQ1]),TDD([makeQuery(id+"F0.imprint","IMPRINT",EDGE,{"disambiguationData":[TD([[makeQuery(id+"F0.imprint","INTERSECT",VERTEX,{"derivedFrom":[subQ1,sQuery(id+"F0.wireOp",EDGE,"E22.MirrorCS")]}),1.0]])],"derivedFrom":subQ1})])]}),makeQuery(id+"F1.opExtrude","SWEPT_FACE",FACE,{"disambiguationData":[OSD([subQ1]),TDD([makeQuery(id+"F0.imprint","IMPRINT",EDGE,{"disambiguationData":[TD([[makeQuery(id+"F0.imprint","INTERSECT",VERTEX,{"derivedFrom":[subQ1,sQuery(id+"F0.wireOp",EDGE,"E20.MirrorCS")]}),1.0]])],"derivedFrom":subQ1})])]}),makeQuery(id+"F1.opExtrude","SWEPT_FACE",FACE,{"disambiguationData":[OSD([subQ1]),TDD([makeQuery(id+"F0.imprint","IMPRINT",EDGE,{"disambiguationData":[TD([[makeQuery(id+"F0.imprint","INTERSECT",VERTEX,{"derivedFrom":[subQ1,sQuery(id+"F0.wireOp",EDGE,"E18.MirrorCS")]}),1.0]])],"derivedFrom":subQ1})])]}),makeQuery(id+"F1.opExtrude","SWEPT_FACE",FACE,{"disambiguationData":[OSD([subQ1]),TDD([makeQuery(id+"F0.imprint","IMPRINT",EDGE,{"disambiguationData":[TD([[makeQuery(id+"F0.imprint","INTERSECT",VERTEX,{"derivedFrom":[subQ1,sQuery(id+"F0.wireOp",EDGE,"E17.MirrorCS")]}),-1.0]])],"derivedFrom":subQ1})])]})],"fromTools":[makeQuery(id+"F5.opSweep","SWEPT_FACE",FACE,{"disambiguationData":[OSD([subQ3,subQ1,subQ0]),TDD([subQ4,makeQuery(id+"F4.imprint","IMPRINT",EDGE,{"disambiguationData":[TD([[makeQuery(id+"F4.imprint","INTERSECT",VERTEX,{"derivedFrom":[subQ2,sQuery(id+"F4.wireOp",EDGE,"E30")]}),1.0]])],"derivedFrom":subQ2})])]}),makeQuery(id+"F5.opSweep","SWEPT_FACE",FACE,{"disambiguationData":[OSD([subQ3,subQ1,subQ0]),TDD([subQ4,makeQuery(id+"F4.imprint","IMPRINT",EDGE,{"disambiguationData":[TD([[makeQuery(id+"F4.imprint","INTERSECT",VERTEX,{"derivedFrom":[subQ2,sQuery(id+"F4.wireOp",EDGE,"E32.MirrorCS")]}),1.0]])],"derivedFrom":subQ2})])]}),makeQuery(id+"F5.opSweep","SWEPT_FACE",FACE,{"disambiguationData":[OSD([subQ3,subQ1,subQ0]),TDD([subQ4,makeQuery(id+"F4.imprint","IMPRINT",EDGE,{"disambiguationData":[TD([[makeQuery(id+"F4.imprint","INTERSECT",VERTEX,{"derivedFrom":[subQ2,sQuery(id+"F4.wireOp",EDGE,"E34.MirrorCS")]}),1.0]])],"derivedFrom":subQ2})])]}),makeQuery(id+"F5.opSweep","SWEPT_FACE",FACE,{"disambiguationData":[OSD([subQ3,subQ1,subQ0]),TDD([subQ4,makeQuery(id+"F4.imprint","IMPRINT",EDGE,{"disambiguationData":[TD([[makeQuery(id+"F4.imprint","INTERSECT",VERTEX,{"derivedFrom":[subQ2,sQuery(id+"F4.wireOp",EDGE,"E36.MirrorCS")]}),1.0]])],"derivedFrom":subQ2})])]}),makeQuery(id+"F5.opSweep","SWEPT_FACE",FACE,{"disambiguationData":[OSD([subQ3,subQ1,subQ0]),TDD([subQ4,makeQuery(id+"F4.imprint","IMPRINT",EDGE,{"disambiguationData":[TD([[makeQuery(id+"F4.imprint","INTERSECT",VERTEX,{"derivedFrom":[subQ2,sQuery(id+"F4.wireOp",EDGE,"E38.MirrorCS")]}),1.0]])],"derivedFrom":subQ2})])]}),makeQuery(id+"F5.opSweep","SWEPT_FACE",FACE,{"disambiguationData":[OSD([subQ3,subQ1,subQ0]),TDD([subQ4,makeQuery(id+"F4.imprint","IMPRINT",EDGE,{"disambiguationData":[TD([[makeQuery(id+"F4.imprint","INTERSECT",VERTEX,{"derivedFrom":[subQ2,sQuery(id+"F4.wireOp",EDGE,"E40.MirrorCS")]}),1.0]])],"derivedFrom":subQ2})])]}),makeQuery(id+"F5.opSweep","SWEPT_FACE",FACE,{"disambiguationData":[OSD([subQ3,subQ1,subQ0]),TDD([subQ4,makeQuery(id+"F4.imprint","IMPRINT",EDGE,{"disambiguationData":[TD([[makeQuery(id+"F4.imprint","INTERSECT",VERTEX,{"derivedFrom":[subQ2,sQuery(id+"F4.wireOp",EDGE,"E42.MirrorCS")]}),1.0]])],"derivedFrom":subQ2})])]})]})]});}
            var Q16;
            {var subQ0=sQuery(id+"F0.wireOp",EDGE,"E10");var subQ2=sQuery(id+"F2.wireOp",EDGE,"E29");var subQ3=sQuery(id+"F0.wireOp",EDGE,"E2");Q16=makeQuery(id+"F8.opFillet","BLEND_EDGE",EDGE,{"blendedFrom":[makeQuery(id+"F3.opExtrude","CAP_EDGE",EDGE,{"disambiguationData":[OSD([subQ2])],"isStart":true}),makeQuery(id+"F5.boolean.opBoolean","SPLIT",FACE,{"disambiguationData":[TD([makeQuery(id+"F3.opExtrude","CAP_FACE",FACE,{"disambiguationData":[OSD([subQ2])],"isStart":true})])],"derivedFrom":makeQuery(id+"F1.opExtrude","SWEPT_FACE",FACE,{"disambiguationData":[OSD([subQ3]),TDD([makeQuery(id+"F0.imprint","IMPRINT",EDGE,{"disambiguationData":[TD([[makeQuery(id+"F0.imprint","INTERSECT",VERTEX,{"derivedFrom":[subQ3,subQ0]}),-1.0]])],"derivedFrom":subQ3})])]})})],"blendedInto":[makeQuery(id+"F5.boolean.opBoolean","SPLIT",FACE,{"disambiguationData":[TD([makeQuery(id+"F3.opExtrude","CAP_FACE",FACE,{"disambiguationData":[OSD([subQ2])],"isStart":true})])],"derivedFrom":makeQuery(id+"F1.opExtrude","SWEPT_FACE",FACE,{"disambiguationData":[OSD([subQ3]),TDD([makeQuery(id+"F0.imprint","IMPRINT",EDGE,{"disambiguationData":[TD([[makeQuery(id+"F0.imprint","INTERSECT",VERTEX,{"derivedFrom":[subQ3,subQ0]}),-1.0]])],"derivedFrom":subQ3})])]})})]});}
            var Q17;
            {var subQ0=sQuery(id+"F0.wireOp",EDGE,"E27.MirrorCS");var subQ1=sQuery(id+"F0.wireOp",EDGE,"E1");var subQ2=makeQuery(id+"F1.opExtrude","SWEPT_EDGE",EDGE,{"disambiguationData":[OSD([subQ1,subQ0])]});var subQ3=sQuery(id+"F0.wireOp",EDGE,"E0");var subQ4=makeQuery(id+"F1.opExtrude","CAP_EDGE",EDGE,{"disambiguationData":[OSD([subQ3])],"isStart":true});Q17=makeQuery(id+"F8.opFillet","BLEND_EDGE",EDGE,{"disambiguationData":[OD(11.0)],"blendedFrom":[makeQuery(id+"F3.opExtrude","CAP_EDGE",EDGE,{"disambiguationData":[OSD([sQuery(id+"F2.wireOp",EDGE,"E29")])],"isStart":true}),makeQuery(id+"F5.boolean.opBoolean","MERGE",FACE,{"derivedFrom":[makeQuery(id+"F1.opExtrude","SWEPT_FACE",FACE,{"disambiguationData":[OSD([subQ1]),TDD([makeQuery(id+"F0.imprint","IMPRINT",EDGE,{"disambiguationData":[TD([[makeQuery(id+"F0.imprint","INTERSECT",VERTEX,{"derivedFrom":[subQ1,sQuery(id+"F0.wireOp",EDGE,"E14.MirrorCS")]}),1.0]])],"derivedFrom":subQ1})])]}),makeQuery(id+"F1.opExtrude","SWEPT_FACE",FACE,{"disambiguationData":[OSD([subQ1]),TDD([makeQuery(id+"F0.imprint","IMPRINT",EDGE,{"disambiguationData":[TD([[makeQuery(id+"F0.imprint","INTERSECT",VERTEX,{"derivedFrom":[subQ1,sQuery(id+"F0.wireOp",EDGE,"E12.MirrorCS")]}),1.0]])],"derivedFrom":subQ1})])]}),makeQuery(id+"F1.opExtrude","SWEPT_FACE",FACE,{"disambiguationData":[OSD([subQ1]),TDD([makeQuery(id+"F0.imprint","IMPRINT",EDGE,{"disambiguationData":[TD([[makeQuery(id+"F0.imprint","INTERSECT",VERTEX,{"derivedFrom":[subQ1,sQuery(id+"F0.wireOp",EDGE,"E3")]}),1.0]])],"derivedFrom":subQ1})])]}),makeQuery(id+"F1.opExtrude","SWEPT_FACE",FACE,{"disambiguationData":[OSD([subQ1]),TDD([makeQuery(id+"F0.imprint","IMPRINT",EDGE,{"disambiguationData":[TD([[makeQuery(id+"F0.imprint","INTERSECT",VERTEX,{"derivedFrom":[subQ1,sQuery(id+"F0.wireOp",EDGE,"E8")]}),1.0]])],"derivedFrom":subQ1})])]}),makeQuery(id+"F1.opExtrude","SWEPT_FACE",FACE,{"disambiguationData":[OSD([subQ1]),TDD([makeQuery(id+"F0.imprint","IMPRINT",EDGE,{"disambiguationData":[TD([[makeQuery(id+"F0.imprint","INTERSECT",VERTEX,{"derivedFrom":[subQ1,sQuery(id+"F0.wireOp",EDGE,"E6")]}),1.0]])],"derivedFrom":subQ1})])]}),makeQuery(id+"F1.opExtrude","SWEPT_FACE",FACE,{"disambiguationData":[OSD([subQ1]),TDD([makeQuery(id+"F0.imprint","IMPRINT",EDGE,{"disambiguationData":[TD([[makeQuery(id+"F0.imprint","INTERSECT",VERTEX,{"derivedFrom":[subQ1,sQuery(id+"F0.wireOp",EDGE,"E5")]}),-1.0]])],"derivedFrom":subQ1})])]}),makeQuery(id+"F1.opExtrude","SWEPT_FACE",FACE,{"disambiguationData":[OSD([subQ1]),TDD([makeQuery(id+"F0.imprint","IMPRINT",EDGE,{"disambiguationData":[TD([[makeQuery(id+"F0.imprint","INTERSECT",VERTEX,{"derivedFrom":[subQ1,sQuery(id+"F0.wireOp",EDGE,"E26.MirrorCS")]}),1.0]])],"derivedFrom":subQ1})])]}),makeQuery(id+"F1.opExtrude","SWEPT_FACE",FACE,{"disambiguationData":[OSD([subQ1]),TDD([makeQuery(id+"F0.imprint","IMPRINT",EDGE,{"disambiguationData":[TD([[makeQuery(id+"F0.imprint","INTERSECT",VERTEX,{"derivedFrom":[subQ1,sQuery(id+"F0.wireOp",EDGE,"E24.MirrorCS")]}),1.0]])],"derivedFrom":subQ1})])]}),makeQuery(id+"F1.opExtrude","SWEPT_FACE",FACE,{"disambiguationData":[OSD([subQ1]),TDD([makeQuery(id+"F0.imprint","IMPRINT",EDGE,{"disambiguationData":[TD([[makeQuery(id+"F0.imprint","INTERSECT",VERTEX,{"derivedFrom":[subQ1,sQuery(id+"F0.wireOp",EDGE,"E22.MirrorCS")]}),1.0]])],"derivedFrom":subQ1})])]}),makeQuery(id+"F1.opExtrude","SWEPT_FACE",FACE,{"disambiguationData":[OSD([subQ1]),TDD([makeQuery(id+"F0.imprint","IMPRINT",EDGE,{"disambiguationData":[TD([[makeQuery(id+"F0.imprint","INTERSECT",VERTEX,{"derivedFrom":[subQ1,sQuery(id+"F0.wireOp",EDGE,"E20.MirrorCS")]}),1.0]])],"derivedFrom":subQ1})])]}),makeQuery(id+"F1.opExtrude","SWEPT_FACE",FACE,{"disambiguationData":[OSD([subQ1]),TDD([makeQuery(id+"F0.imprint","IMPRINT",EDGE,{"disambiguationData":[TD([[makeQuery(id+"F0.imprint","INTERSECT",VERTEX,{"derivedFrom":[subQ1,sQuery(id+"F0.wireOp",EDGE,"E18.MirrorCS")]}),1.0]])],"derivedFrom":subQ1})])]}),makeQuery(id+"F1.opExtrude","SWEPT_FACE",FACE,{"disambiguationData":[OSD([subQ1]),TDD([makeQuery(id+"F0.imprint","IMPRINT",EDGE,{"disambiguationData":[TD([[makeQuery(id+"F0.imprint","INTERSECT",VERTEX,{"derivedFrom":[subQ1,sQuery(id+"F0.wireOp",EDGE,"E17.MirrorCS")]}),-1.0]])],"derivedFrom":subQ1})])]})],"fromTools":[makeQuery(id+"F5.opSweep","SWEPT_FACE",FACE,{"disambiguationData":[OSD([subQ3,subQ1,subQ0]),TDD([subQ4,makeQuery(id+"F4.imprint","IMPRINT",EDGE,{"disambiguationData":[TD([[makeQuery(id+"F4.imprint","INTERSECT",VERTEX,{"derivedFrom":[subQ2,sQuery(id+"F4.wireOp",EDGE,"E30")]}),1.0]])],"derivedFrom":subQ2})])]}),makeQuery(id+"F5.opSweep","SWEPT_FACE",FACE,{"disambiguationData":[OSD([subQ3,subQ1,subQ0]),TDD([subQ4,makeQuery(id+"F4.imprint","IMPRINT",EDGE,{"disambiguationData":[TD([[makeQuery(id+"F4.imprint","INTERSECT",VERTEX,{"derivedFrom":[subQ2,sQuery(id+"F4.wireOp",EDGE,"E32.MirrorCS")]}),1.0]])],"derivedFrom":subQ2})])]}),makeQuery(id+"F5.opSweep","SWEPT_FACE",FACE,{"disambiguationData":[OSD([subQ3,subQ1,subQ0]),TDD([subQ4,makeQuery(id+"F4.imprint","IMPRINT",EDGE,{"disambiguationData":[TD([[makeQuery(id+"F4.imprint","INTERSECT",VERTEX,{"derivedFrom":[subQ2,sQuery(id+"F4.wireOp",EDGE,"E34.MirrorCS")]}),1.0]])],"derivedFrom":subQ2})])]}),makeQuery(id+"F5.opSweep","SWEPT_FACE",FACE,{"disambiguationData":[OSD([subQ3,subQ1,subQ0]),TDD([subQ4,makeQuery(id+"F4.imprint","IMPRINT",EDGE,{"disambiguationData":[TD([[makeQuery(id+"F4.imprint","INTERSECT",VERTEX,{"derivedFrom":[subQ2,sQuery(id+"F4.wireOp",EDGE,"E36.MirrorCS")]}),1.0]])],"derivedFrom":subQ2})])]}),makeQuery(id+"F5.opSweep","SWEPT_FACE",FACE,{"disambiguationData":[OSD([subQ3,subQ1,subQ0]),TDD([subQ4,makeQuery(id+"F4.imprint","IMPRINT",EDGE,{"disambiguationData":[TD([[makeQuery(id+"F4.imprint","INTERSECT",VERTEX,{"derivedFrom":[subQ2,sQuery(id+"F4.wireOp",EDGE,"E38.MirrorCS")]}),1.0]])],"derivedFrom":subQ2})])]}),makeQuery(id+"F5.opSweep","SWEPT_FACE",FACE,{"disambiguationData":[OSD([subQ3,subQ1,subQ0]),TDD([subQ4,makeQuery(id+"F4.imprint","IMPRINT",EDGE,{"disambiguationData":[TD([[makeQuery(id+"F4.imprint","INTERSECT",VERTEX,{"derivedFrom":[subQ2,sQuery(id+"F4.wireOp",EDGE,"E40.MirrorCS")]}),1.0]])],"derivedFrom":subQ2})])]}),makeQuery(id+"F5.opSweep","SWEPT_FACE",FACE,{"disambiguationData":[OSD([subQ3,subQ1,subQ0]),TDD([subQ4,makeQuery(id+"F4.imprint","IMPRINT",EDGE,{"disambiguationData":[TD([[makeQuery(id+"F4.imprint","INTERSECT",VERTEX,{"derivedFrom":[subQ2,sQuery(id+"F4.wireOp",EDGE,"E42.MirrorCS")]}),1.0]])],"derivedFrom":subQ2})])]})]})],"blendedInto":[makeQuery(id+"F5.boolean.opBoolean","MERGE",FACE,{"derivedFrom":[makeQuery(id+"F1.opExtrude","SWEPT_FACE",FACE,{"disambiguationData":[OSD([subQ1]),TDD([makeQuery(id+"F0.imprint","IMPRINT",EDGE,{"disambiguationData":[TD([[makeQuery(id+"F0.imprint","INTERSECT",VERTEX,{"derivedFrom":[subQ1,sQuery(id+"F0.wireOp",EDGE,"E14.MirrorCS")]}),1.0]])],"derivedFrom":subQ1})])]}),makeQuery(id+"F1.opExtrude","SWEPT_FACE",FACE,{"disambiguationData":[OSD([subQ1]),TDD([makeQuery(id+"F0.imprint","IMPRINT",EDGE,{"disambiguationData":[TD([[makeQuery(id+"F0.imprint","INTERSECT",VERTEX,{"derivedFrom":[subQ1,sQuery(id+"F0.wireOp",EDGE,"E12.MirrorCS")]}),1.0]])],"derivedFrom":subQ1})])]}),makeQuery(id+"F1.opExtrude","SWEPT_FACE",FACE,{"disambiguationData":[OSD([subQ1]),TDD([makeQuery(id+"F0.imprint","IMPRINT",EDGE,{"disambiguationData":[TD([[makeQuery(id+"F0.imprint","INTERSECT",VERTEX,{"derivedFrom":[subQ1,sQuery(id+"F0.wireOp",EDGE,"E3")]}),1.0]])],"derivedFrom":subQ1})])]}),makeQuery(id+"F1.opExtrude","SWEPT_FACE",FACE,{"disambiguationData":[OSD([subQ1]),TDD([makeQuery(id+"F0.imprint","IMPRINT",EDGE,{"disambiguationData":[TD([[makeQuery(id+"F0.imprint","INTERSECT",VERTEX,{"derivedFrom":[subQ1,sQuery(id+"F0.wireOp",EDGE,"E8")]}),1.0]])],"derivedFrom":subQ1})])]}),makeQuery(id+"F1.opExtrude","SWEPT_FACE",FACE,{"disambiguationData":[OSD([subQ1]),TDD([makeQuery(id+"F0.imprint","IMPRINT",EDGE,{"disambiguationData":[TD([[makeQuery(id+"F0.imprint","INTERSECT",VERTEX,{"derivedFrom":[subQ1,sQuery(id+"F0.wireOp",EDGE,"E6")]}),1.0]])],"derivedFrom":subQ1})])]}),makeQuery(id+"F1.opExtrude","SWEPT_FACE",FACE,{"disambiguationData":[OSD([subQ1]),TDD([makeQuery(id+"F0.imprint","IMPRINT",EDGE,{"disambiguationData":[TD([[makeQuery(id+"F0.imprint","INTERSECT",VERTEX,{"derivedFrom":[subQ1,sQuery(id+"F0.wireOp",EDGE,"E5")]}),-1.0]])],"derivedFrom":subQ1})])]}),makeQuery(id+"F1.opExtrude","SWEPT_FACE",FACE,{"disambiguationData":[OSD([subQ1]),TDD([makeQuery(id+"F0.imprint","IMPRINT",EDGE,{"disambiguationData":[TD([[makeQuery(id+"F0.imprint","INTERSECT",VERTEX,{"derivedFrom":[subQ1,sQuery(id+"F0.wireOp",EDGE,"E26.MirrorCS")]}),1.0]])],"derivedFrom":subQ1})])]}),makeQuery(id+"F1.opExtrude","SWEPT_FACE",FACE,{"disambiguationData":[OSD([subQ1]),TDD([makeQuery(id+"F0.imprint","IMPRINT",EDGE,{"disambiguationData":[TD([[makeQuery(id+"F0.imprint","INTERSECT",VERTEX,{"derivedFrom":[subQ1,sQuery(id+"F0.wireOp",EDGE,"E24.MirrorCS")]}),1.0]])],"derivedFrom":subQ1})])]}),makeQuery(id+"F1.opExtrude","SWEPT_FACE",FACE,{"disambiguationData":[OSD([subQ1]),TDD([makeQuery(id+"F0.imprint","IMPRINT",EDGE,{"disambiguationData":[TD([[makeQuery(id+"F0.imprint","INTERSECT",VERTEX,{"derivedFrom":[subQ1,sQuery(id+"F0.wireOp",EDGE,"E22.MirrorCS")]}),1.0]])],"derivedFrom":subQ1})])]}),makeQuery(id+"F1.opExtrude","SWEPT_FACE",FACE,{"disambiguationData":[OSD([subQ1]),TDD([makeQuery(id+"F0.imprint","IMPRINT",EDGE,{"disambiguationData":[TD([[makeQuery(id+"F0.imprint","INTERSECT",VERTEX,{"derivedFrom":[subQ1,sQuery(id+"F0.wireOp",EDGE,"E20.MirrorCS")]}),1.0]])],"derivedFrom":subQ1})])]}),makeQuery(id+"F1.opExtrude","SWEPT_FACE",FACE,{"disambiguationData":[OSD([subQ1]),TDD([makeQuery(id+"F0.imprint","IMPRINT",EDGE,{"disambiguationData":[TD([[makeQuery(id+"F0.imprint","INTERSECT",VERTEX,{"derivedFrom":[subQ1,sQuery(id+"F0.wireOp",EDGE,"E18.MirrorCS")]}),1.0]])],"derivedFrom":subQ1})])]}),makeQuery(id+"F1.opExtrude","SWEPT_FACE",FACE,{"disambiguationData":[OSD([subQ1]),TDD([makeQuery(id+"F0.imprint","IMPRINT",EDGE,{"disambiguationData":[TD([[makeQuery(id+"F0.imprint","INTERSECT",VERTEX,{"derivedFrom":[subQ1,sQuery(id+"F0.wireOp",EDGE,"E17.MirrorCS")]}),-1.0]])],"derivedFrom":subQ1})])]})],"fromTools":[makeQuery(id+"F5.opSweep","SWEPT_FACE",FACE,{"disambiguationData":[OSD([subQ3,subQ1,subQ0]),TDD([subQ4,makeQuery(id+"F4.imprint","IMPRINT",EDGE,{"disambiguationData":[TD([[makeQuery(id+"F4.imprint","INTERSECT",VERTEX,{"derivedFrom":[subQ2,sQuery(id+"F4.wireOp",EDGE,"E30")]}),1.0]])],"derivedFrom":subQ2})])]}),makeQuery(id+"F5.opSweep","SWEPT_FACE",FACE,{"disambiguationData":[OSD([subQ3,subQ1,subQ0]),TDD([subQ4,makeQuery(id+"F4.imprint","IMPRINT",EDGE,{"disambiguationData":[TD([[makeQuery(id+"F4.imprint","INTERSECT",VERTEX,{"derivedFrom":[subQ2,sQuery(id+"F4.wireOp",EDGE,"E32.MirrorCS")]}),1.0]])],"derivedFrom":subQ2})])]}),makeQuery(id+"F5.opSweep","SWEPT_FACE",FACE,{"disambiguationData":[OSD([subQ3,subQ1,subQ0]),TDD([subQ4,makeQuery(id+"F4.imprint","IMPRINT",EDGE,{"disambiguationData":[TD([[makeQuery(id+"F4.imprint","INTERSECT",VERTEX,{"derivedFrom":[subQ2,sQuery(id+"F4.wireOp",EDGE,"E34.MirrorCS")]}),1.0]])],"derivedFrom":subQ2})])]}),makeQuery(id+"F5.opSweep","SWEPT_FACE",FACE,{"disambiguationData":[OSD([subQ3,subQ1,subQ0]),TDD([subQ4,makeQuery(id+"F4.imprint","IMPRINT",EDGE,{"disambiguationData":[TD([[makeQuery(id+"F4.imprint","INTERSECT",VERTEX,{"derivedFrom":[subQ2,sQuery(id+"F4.wireOp",EDGE,"E36.MirrorCS")]}),1.0]])],"derivedFrom":subQ2})])]}),makeQuery(id+"F5.opSweep","SWEPT_FACE",FACE,{"disambiguationData":[OSD([subQ3,subQ1,subQ0]),TDD([subQ4,makeQuery(id+"F4.imprint","IMPRINT",EDGE,{"disambiguationData":[TD([[makeQuery(id+"F4.imprint","INTERSECT",VERTEX,{"derivedFrom":[subQ2,sQuery(id+"F4.wireOp",EDGE,"E38.MirrorCS")]}),1.0]])],"derivedFrom":subQ2})])]}),makeQuery(id+"F5.opSweep","SWEPT_FACE",FACE,{"disambiguationData":[OSD([subQ3,subQ1,subQ0]),TDD([subQ4,makeQuery(id+"F4.imprint","IMPRINT",EDGE,{"disambiguationData":[TD([[makeQuery(id+"F4.imprint","INTERSECT",VERTEX,{"derivedFrom":[subQ2,sQuery(id+"F4.wireOp",EDGE,"E40.MirrorCS")]}),1.0]])],"derivedFrom":subQ2})])]}),makeQuery(id+"F5.opSweep","SWEPT_FACE",FACE,{"disambiguationData":[OSD([subQ3,subQ1,subQ0]),TDD([subQ4,makeQuery(id+"F4.imprint","IMPRINT",EDGE,{"disambiguationData":[TD([[makeQuery(id+"F4.imprint","INTERSECT",VERTEX,{"derivedFrom":[subQ2,sQuery(id+"F4.wireOp",EDGE,"E42.MirrorCS")]}),1.0]])],"derivedFrom":subQ2})])]})]})]});}
            var Q18;
            {var subQ0=sQuery(id+"F0.wireOp",EDGE,"E25.MirrorCS");var subQ2=sQuery(id+"F2.wireOp",EDGE,"E29");var subQ3=sQuery(id+"F0.wireOp",EDGE,"E2");Q18=makeQuery(id+"F8.opFillet","BLEND_EDGE",EDGE,{"blendedFrom":[makeQuery(id+"F3.opExtrude","CAP_EDGE",EDGE,{"disambiguationData":[OSD([subQ2])],"isStart":true}),makeQuery(id+"F5.boolean.opBoolean","SPLIT",FACE,{"disambiguationData":[TD([makeQuery(id+"F3.opExtrude","CAP_FACE",FACE,{"disambiguationData":[OSD([subQ2])],"isStart":true})])],"derivedFrom":makeQuery(id+"F1.opExtrude","SWEPT_FACE",FACE,{"disambiguationData":[OSD([subQ3]),TDD([makeQuery(id+"F0.imprint","IMPRINT",EDGE,{"disambiguationData":[TD([[makeQuery(id+"F0.imprint","INTERSECT",VERTEX,{"derivedFrom":[subQ3,subQ0]}),1.0]])],"derivedFrom":subQ3})])]})})],"blendedInto":[makeQuery(id+"F5.boolean.opBoolean","SPLIT",FACE,{"disambiguationData":[TD([makeQuery(id+"F3.opExtrude","CAP_FACE",FACE,{"disambiguationData":[OSD([subQ2])],"isStart":true})])],"derivedFrom":makeQuery(id+"F1.opExtrude","SWEPT_FACE",FACE,{"disambiguationData":[OSD([subQ3]),TDD([makeQuery(id+"F0.imprint","IMPRINT",EDGE,{"disambiguationData":[TD([[makeQuery(id+"F0.imprint","INTERSECT",VERTEX,{"derivedFrom":[subQ3,subQ0]}),1.0]])],"derivedFrom":subQ3})])]})})]});}
            var Q19;
            {var subQ0=sQuery(id+"F0.wireOp",EDGE,"E27.MirrorCS");var subQ1=sQuery(id+"F0.wireOp",EDGE,"E1");var subQ2=makeQuery(id+"F1.opExtrude","SWEPT_EDGE",EDGE,{"disambiguationData":[OSD([subQ1,subQ0])]});var subQ3=sQuery(id+"F0.wireOp",EDGE,"E0");var subQ4=makeQuery(id+"F1.opExtrude","CAP_EDGE",EDGE,{"disambiguationData":[OSD([subQ3])],"isStart":true});Q19=makeQuery(id+"F8.opFillet","BLEND_EDGE",EDGE,{"disambiguationData":[OD(10.0)],"blendedFrom":[makeQuery(id+"F3.opExtrude","CAP_EDGE",EDGE,{"disambiguationData":[OSD([sQuery(id+"F2.wireOp",EDGE,"E29")])],"isStart":true}),makeQuery(id+"F5.boolean.opBoolean","MERGE",FACE,{"derivedFrom":[makeQuery(id+"F1.opExtrude","SWEPT_FACE",FACE,{"disambiguationData":[OSD([subQ1]),TDD([makeQuery(id+"F0.imprint","IMPRINT",EDGE,{"disambiguationData":[TD([[makeQuery(id+"F0.imprint","INTERSECT",VERTEX,{"derivedFrom":[subQ1,sQuery(id+"F0.wireOp",EDGE,"E14.MirrorCS")]}),1.0]])],"derivedFrom":subQ1})])]}),makeQuery(id+"F1.opExtrude","SWEPT_FACE",FACE,{"disambiguationData":[OSD([subQ1]),TDD([makeQuery(id+"F0.imprint","IMPRINT",EDGE,{"disambiguationData":[TD([[makeQuery(id+"F0.imprint","INTERSECT",VERTEX,{"derivedFrom":[subQ1,sQuery(id+"F0.wireOp",EDGE,"E12.MirrorCS")]}),1.0]])],"derivedFrom":subQ1})])]}),makeQuery(id+"F1.opExtrude","SWEPT_FACE",FACE,{"disambiguationData":[OSD([subQ1]),TDD([makeQuery(id+"F0.imprint","IMPRINT",EDGE,{"disambiguationData":[TD([[makeQuery(id+"F0.imprint","INTERSECT",VERTEX,{"derivedFrom":[subQ1,sQuery(id+"F0.wireOp",EDGE,"E3")]}),1.0]])],"derivedFrom":subQ1})])]}),makeQuery(id+"F1.opExtrude","SWEPT_FACE",FACE,{"disambiguationData":[OSD([subQ1]),TDD([makeQuery(id+"F0.imprint","IMPRINT",EDGE,{"disambiguationData":[TD([[makeQuery(id+"F0.imprint","INTERSECT",VERTEX,{"derivedFrom":[subQ1,sQuery(id+"F0.wireOp",EDGE,"E8")]}),1.0]])],"derivedFrom":subQ1})])]}),makeQuery(id+"F1.opExtrude","SWEPT_FACE",FACE,{"disambiguationData":[OSD([subQ1]),TDD([makeQuery(id+"F0.imprint","IMPRINT",EDGE,{"disambiguationData":[TD([[makeQuery(id+"F0.imprint","INTERSECT",VERTEX,{"derivedFrom":[subQ1,sQuery(id+"F0.wireOp",EDGE,"E6")]}),1.0]])],"derivedFrom":subQ1})])]}),makeQuery(id+"F1.opExtrude","SWEPT_FACE",FACE,{"disambiguationData":[OSD([subQ1]),TDD([makeQuery(id+"F0.imprint","IMPRINT",EDGE,{"disambiguationData":[TD([[makeQuery(id+"F0.imprint","INTERSECT",VERTEX,{"derivedFrom":[subQ1,sQuery(id+"F0.wireOp",EDGE,"E5")]}),-1.0]])],"derivedFrom":subQ1})])]}),makeQuery(id+"F1.opExtrude","SWEPT_FACE",FACE,{"disambiguationData":[OSD([subQ1]),TDD([makeQuery(id+"F0.imprint","IMPRINT",EDGE,{"disambiguationData":[TD([[makeQuery(id+"F0.imprint","INTERSECT",VERTEX,{"derivedFrom":[subQ1,sQuery(id+"F0.wireOp",EDGE,"E26.MirrorCS")]}),1.0]])],"derivedFrom":subQ1})])]}),makeQuery(id+"F1.opExtrude","SWEPT_FACE",FACE,{"disambiguationData":[OSD([subQ1]),TDD([makeQuery(id+"F0.imprint","IMPRINT",EDGE,{"disambiguationData":[TD([[makeQuery(id+"F0.imprint","INTERSECT",VERTEX,{"derivedFrom":[subQ1,sQuery(id+"F0.wireOp",EDGE,"E24.MirrorCS")]}),1.0]])],"derivedFrom":subQ1})])]}),makeQuery(id+"F1.opExtrude","SWEPT_FACE",FACE,{"disambiguationData":[OSD([subQ1]),TDD([makeQuery(id+"F0.imprint","IMPRINT",EDGE,{"disambiguationData":[TD([[makeQuery(id+"F0.imprint","INTERSECT",VERTEX,{"derivedFrom":[subQ1,sQuery(id+"F0.wireOp",EDGE,"E22.MirrorCS")]}),1.0]])],"derivedFrom":subQ1})])]}),makeQuery(id+"F1.opExtrude","SWEPT_FACE",FACE,{"disambiguationData":[OSD([subQ1]),TDD([makeQuery(id+"F0.imprint","IMPRINT",EDGE,{"disambiguationData":[TD([[makeQuery(id+"F0.imprint","INTERSECT",VERTEX,{"derivedFrom":[subQ1,sQuery(id+"F0.wireOp",EDGE,"E20.MirrorCS")]}),1.0]])],"derivedFrom":subQ1})])]}),makeQuery(id+"F1.opExtrude","SWEPT_FACE",FACE,{"disambiguationData":[OSD([subQ1]),TDD([makeQuery(id+"F0.imprint","IMPRINT",EDGE,{"disambiguationData":[TD([[makeQuery(id+"F0.imprint","INTERSECT",VERTEX,{"derivedFrom":[subQ1,sQuery(id+"F0.wireOp",EDGE,"E18.MirrorCS")]}),1.0]])],"derivedFrom":subQ1})])]}),makeQuery(id+"F1.opExtrude","SWEPT_FACE",FACE,{"disambiguationData":[OSD([subQ1]),TDD([makeQuery(id+"F0.imprint","IMPRINT",EDGE,{"disambiguationData":[TD([[makeQuery(id+"F0.imprint","INTERSECT",VERTEX,{"derivedFrom":[subQ1,sQuery(id+"F0.wireOp",EDGE,"E17.MirrorCS")]}),-1.0]])],"derivedFrom":subQ1})])]})],"fromTools":[makeQuery(id+"F5.opSweep","SWEPT_FACE",FACE,{"disambiguationData":[OSD([subQ3,subQ1,subQ0]),TDD([subQ4,makeQuery(id+"F4.imprint","IMPRINT",EDGE,{"disambiguationData":[TD([[makeQuery(id+"F4.imprint","INTERSECT",VERTEX,{"derivedFrom":[subQ2,sQuery(id+"F4.wireOp",EDGE,"E30")]}),1.0]])],"derivedFrom":subQ2})])]}),makeQuery(id+"F5.opSweep","SWEPT_FACE",FACE,{"disambiguationData":[OSD([subQ3,subQ1,subQ0]),TDD([subQ4,makeQuery(id+"F4.imprint","IMPRINT",EDGE,{"disambiguationData":[TD([[makeQuery(id+"F4.imprint","INTERSECT",VERTEX,{"derivedFrom":[subQ2,sQuery(id+"F4.wireOp",EDGE,"E32.MirrorCS")]}),1.0]])],"derivedFrom":subQ2})])]}),makeQuery(id+"F5.opSweep","SWEPT_FACE",FACE,{"disambiguationData":[OSD([subQ3,subQ1,subQ0]),TDD([subQ4,makeQuery(id+"F4.imprint","IMPRINT",EDGE,{"disambiguationData":[TD([[makeQuery(id+"F4.imprint","INTERSECT",VERTEX,{"derivedFrom":[subQ2,sQuery(id+"F4.wireOp",EDGE,"E34.MirrorCS")]}),1.0]])],"derivedFrom":subQ2})])]}),makeQuery(id+"F5.opSweep","SWEPT_FACE",FACE,{"disambiguationData":[OSD([subQ3,subQ1,subQ0]),TDD([subQ4,makeQuery(id+"F4.imprint","IMPRINT",EDGE,{"disambiguationData":[TD([[makeQuery(id+"F4.imprint","INTERSECT",VERTEX,{"derivedFrom":[subQ2,sQuery(id+"F4.wireOp",EDGE,"E36.MirrorCS")]}),1.0]])],"derivedFrom":subQ2})])]}),makeQuery(id+"F5.opSweep","SWEPT_FACE",FACE,{"disambiguationData":[OSD([subQ3,subQ1,subQ0]),TDD([subQ4,makeQuery(id+"F4.imprint","IMPRINT",EDGE,{"disambiguationData":[TD([[makeQuery(id+"F4.imprint","INTERSECT",VERTEX,{"derivedFrom":[subQ2,sQuery(id+"F4.wireOp",EDGE,"E38.MirrorCS")]}),1.0]])],"derivedFrom":subQ2})])]}),makeQuery(id+"F5.opSweep","SWEPT_FACE",FACE,{"disambiguationData":[OSD([subQ3,subQ1,subQ0]),TDD([subQ4,makeQuery(id+"F4.imprint","IMPRINT",EDGE,{"disambiguationData":[TD([[makeQuery(id+"F4.imprint","INTERSECT",VERTEX,{"derivedFrom":[subQ2,sQuery(id+"F4.wireOp",EDGE,"E40.MirrorCS")]}),1.0]])],"derivedFrom":subQ2})])]}),makeQuery(id+"F5.opSweep","SWEPT_FACE",FACE,{"disambiguationData":[OSD([subQ3,subQ1,subQ0]),TDD([subQ4,makeQuery(id+"F4.imprint","IMPRINT",EDGE,{"disambiguationData":[TD([[makeQuery(id+"F4.imprint","INTERSECT",VERTEX,{"derivedFrom":[subQ2,sQuery(id+"F4.wireOp",EDGE,"E42.MirrorCS")]}),1.0]])],"derivedFrom":subQ2})])]})]})],"blendedInto":[makeQuery(id+"F5.boolean.opBoolean","MERGE",FACE,{"derivedFrom":[makeQuery(id+"F1.opExtrude","SWEPT_FACE",FACE,{"disambiguationData":[OSD([subQ1]),TDD([makeQuery(id+"F0.imprint","IMPRINT",EDGE,{"disambiguationData":[TD([[makeQuery(id+"F0.imprint","INTERSECT",VERTEX,{"derivedFrom":[subQ1,sQuery(id+"F0.wireOp",EDGE,"E14.MirrorCS")]}),1.0]])],"derivedFrom":subQ1})])]}),makeQuery(id+"F1.opExtrude","SWEPT_FACE",FACE,{"disambiguationData":[OSD([subQ1]),TDD([makeQuery(id+"F0.imprint","IMPRINT",EDGE,{"disambiguationData":[TD([[makeQuery(id+"F0.imprint","INTERSECT",VERTEX,{"derivedFrom":[subQ1,sQuery(id+"F0.wireOp",EDGE,"E12.MirrorCS")]}),1.0]])],"derivedFrom":subQ1})])]}),makeQuery(id+"F1.opExtrude","SWEPT_FACE",FACE,{"disambiguationData":[OSD([subQ1]),TDD([makeQuery(id+"F0.imprint","IMPRINT",EDGE,{"disambiguationData":[TD([[makeQuery(id+"F0.imprint","INTERSECT",VERTEX,{"derivedFrom":[subQ1,sQuery(id+"F0.wireOp",EDGE,"E3")]}),1.0]])],"derivedFrom":subQ1})])]}),makeQuery(id+"F1.opExtrude","SWEPT_FACE",FACE,{"disambiguationData":[OSD([subQ1]),TDD([makeQuery(id+"F0.imprint","IMPRINT",EDGE,{"disambiguationData":[TD([[makeQuery(id+"F0.imprint","INTERSECT",VERTEX,{"derivedFrom":[subQ1,sQuery(id+"F0.wireOp",EDGE,"E8")]}),1.0]])],"derivedFrom":subQ1})])]}),makeQuery(id+"F1.opExtrude","SWEPT_FACE",FACE,{"disambiguationData":[OSD([subQ1]),TDD([makeQuery(id+"F0.imprint","IMPRINT",EDGE,{"disambiguationData":[TD([[makeQuery(id+"F0.imprint","INTERSECT",VERTEX,{"derivedFrom":[subQ1,sQuery(id+"F0.wireOp",EDGE,"E6")]}),1.0]])],"derivedFrom":subQ1})])]}),makeQuery(id+"F1.opExtrude","SWEPT_FACE",FACE,{"disambiguationData":[OSD([subQ1]),TDD([makeQuery(id+"F0.imprint","IMPRINT",EDGE,{"disambiguationData":[TD([[makeQuery(id+"F0.imprint","INTERSECT",VERTEX,{"derivedFrom":[subQ1,sQuery(id+"F0.wireOp",EDGE,"E5")]}),-1.0]])],"derivedFrom":subQ1})])]}),makeQuery(id+"F1.opExtrude","SWEPT_FACE",FACE,{"disambiguationData":[OSD([subQ1]),TDD([makeQuery(id+"F0.imprint","IMPRINT",EDGE,{"disambiguationData":[TD([[makeQuery(id+"F0.imprint","INTERSECT",VERTEX,{"derivedFrom":[subQ1,sQuery(id+"F0.wireOp",EDGE,"E26.MirrorCS")]}),1.0]])],"derivedFrom":subQ1})])]}),makeQuery(id+"F1.opExtrude","SWEPT_FACE",FACE,{"disambiguationData":[OSD([subQ1]),TDD([makeQuery(id+"F0.imprint","IMPRINT",EDGE,{"disambiguationData":[TD([[makeQuery(id+"F0.imprint","INTERSECT",VERTEX,{"derivedFrom":[subQ1,sQuery(id+"F0.wireOp",EDGE,"E24.MirrorCS")]}),1.0]])],"derivedFrom":subQ1})])]}),makeQuery(id+"F1.opExtrude","SWEPT_FACE",FACE,{"disambiguationData":[OSD([subQ1]),TDD([makeQuery(id+"F0.imprint","IMPRINT",EDGE,{"disambiguationData":[TD([[makeQuery(id+"F0.imprint","INTERSECT",VERTEX,{"derivedFrom":[subQ1,sQuery(id+"F0.wireOp",EDGE,"E22.MirrorCS")]}),1.0]])],"derivedFrom":subQ1})])]}),makeQuery(id+"F1.opExtrude","SWEPT_FACE",FACE,{"disambiguationData":[OSD([subQ1]),TDD([makeQuery(id+"F0.imprint","IMPRINT",EDGE,{"disambiguationData":[TD([[makeQuery(id+"F0.imprint","INTERSECT",VERTEX,{"derivedFrom":[subQ1,sQuery(id+"F0.wireOp",EDGE,"E20.MirrorCS")]}),1.0]])],"derivedFrom":subQ1})])]}),makeQuery(id+"F1.opExtrude","SWEPT_FACE",FACE,{"disambiguationData":[OSD([subQ1]),TDD([makeQuery(id+"F0.imprint","IMPRINT",EDGE,{"disambiguationData":[TD([[makeQuery(id+"F0.imprint","INTERSECT",VERTEX,{"derivedFrom":[subQ1,sQuery(id+"F0.wireOp",EDGE,"E18.MirrorCS")]}),1.0]])],"derivedFrom":subQ1})])]}),makeQuery(id+"F1.opExtrude","SWEPT_FACE",FACE,{"disambiguationData":[OSD([subQ1]),TDD([makeQuery(id+"F0.imprint","IMPRINT",EDGE,{"disambiguationData":[TD([[makeQuery(id+"F0.imprint","INTERSECT",VERTEX,{"derivedFrom":[subQ1,sQuery(id+"F0.wireOp",EDGE,"E17.MirrorCS")]}),-1.0]])],"derivedFrom":subQ1})])]})],"fromTools":[makeQuery(id+"F5.opSweep","SWEPT_FACE",FACE,{"disambiguationData":[OSD([subQ3,subQ1,subQ0]),TDD([subQ4,makeQuery(id+"F4.imprint","IMPRINT",EDGE,{"disambiguationData":[TD([[makeQuery(id+"F4.imprint","INTERSECT",VERTEX,{"derivedFrom":[subQ2,sQuery(id+"F4.wireOp",EDGE,"E30")]}),1.0]])],"derivedFrom":subQ2})])]}),makeQuery(id+"F5.opSweep","SWEPT_FACE",FACE,{"disambiguationData":[OSD([subQ3,subQ1,subQ0]),TDD([subQ4,makeQuery(id+"F4.imprint","IMPRINT",EDGE,{"disambiguationData":[TD([[makeQuery(id+"F4.imprint","INTERSECT",VERTEX,{"derivedFrom":[subQ2,sQuery(id+"F4.wireOp",EDGE,"E32.MirrorCS")]}),1.0]])],"derivedFrom":subQ2})])]}),makeQuery(id+"F5.opSweep","SWEPT_FACE",FACE,{"disambiguationData":[OSD([subQ3,subQ1,subQ0]),TDD([subQ4,makeQuery(id+"F4.imprint","IMPRINT",EDGE,{"disambiguationData":[TD([[makeQuery(id+"F4.imprint","INTERSECT",VERTEX,{"derivedFrom":[subQ2,sQuery(id+"F4.wireOp",EDGE,"E34.MirrorCS")]}),1.0]])],"derivedFrom":subQ2})])]}),makeQuery(id+"F5.opSweep","SWEPT_FACE",FACE,{"disambiguationData":[OSD([subQ3,subQ1,subQ0]),TDD([subQ4,makeQuery(id+"F4.imprint","IMPRINT",EDGE,{"disambiguationData":[TD([[makeQuery(id+"F4.imprint","INTERSECT",VERTEX,{"derivedFrom":[subQ2,sQuery(id+"F4.wireOp",EDGE,"E36.MirrorCS")]}),1.0]])],"derivedFrom":subQ2})])]}),makeQuery(id+"F5.opSweep","SWEPT_FACE",FACE,{"disambiguationData":[OSD([subQ3,subQ1,subQ0]),TDD([subQ4,makeQuery(id+"F4.imprint","IMPRINT",EDGE,{"disambiguationData":[TD([[makeQuery(id+"F4.imprint","INTERSECT",VERTEX,{"derivedFrom":[subQ2,sQuery(id+"F4.wireOp",EDGE,"E38.MirrorCS")]}),1.0]])],"derivedFrom":subQ2})])]}),makeQuery(id+"F5.opSweep","SWEPT_FACE",FACE,{"disambiguationData":[OSD([subQ3,subQ1,subQ0]),TDD([subQ4,makeQuery(id+"F4.imprint","IMPRINT",EDGE,{"disambiguationData":[TD([[makeQuery(id+"F4.imprint","INTERSECT",VERTEX,{"derivedFrom":[subQ2,sQuery(id+"F4.wireOp",EDGE,"E40.MirrorCS")]}),1.0]])],"derivedFrom":subQ2})])]}),makeQuery(id+"F5.opSweep","SWEPT_FACE",FACE,{"disambiguationData":[OSD([subQ3,subQ1,subQ0]),TDD([subQ4,makeQuery(id+"F4.imprint","IMPRINT",EDGE,{"disambiguationData":[TD([[makeQuery(id+"F4.imprint","INTERSECT",VERTEX,{"derivedFrom":[subQ2,sQuery(id+"F4.wireOp",EDGE,"E42.MirrorCS")]}),1.0]])],"derivedFrom":subQ2})])]})]})]});}
            var Q20;
            {var subQ0=sQuery(id+"F0.wireOp",EDGE,"E23.MirrorCS");var subQ2=sQuery(id+"F2.wireOp",EDGE,"E29");var subQ3=sQuery(id+"F0.wireOp",EDGE,"E2");Q20=makeQuery(id+"F8.opFillet","BLEND_EDGE",EDGE,{"blendedFrom":[makeQuery(id+"F3.opExtrude","CAP_EDGE",EDGE,{"disambiguationData":[OSD([subQ2])],"isStart":true}),makeQuery(id+"F5.boolean.opBoolean","SPLIT",FACE,{"disambiguationData":[TD([makeQuery(id+"F3.opExtrude","CAP_FACE",FACE,{"disambiguationData":[OSD([subQ2])],"isStart":true})])],"derivedFrom":makeQuery(id+"F1.opExtrude","SWEPT_FACE",FACE,{"disambiguationData":[OSD([subQ3]),TDD([makeQuery(id+"F0.imprint","IMPRINT",EDGE,{"disambiguationData":[TD([[makeQuery(id+"F0.imprint","INTERSECT",VERTEX,{"derivedFrom":[subQ3,subQ0]}),1.0]])],"derivedFrom":subQ3})])]})})],"blendedInto":[makeQuery(id+"F5.boolean.opBoolean","SPLIT",FACE,{"disambiguationData":[TD([makeQuery(id+"F3.opExtrude","CAP_FACE",FACE,{"disambiguationData":[OSD([subQ2])],"isStart":true})])],"derivedFrom":makeQuery(id+"F1.opExtrude","SWEPT_FACE",FACE,{"disambiguationData":[OSD([subQ3]),TDD([makeQuery(id+"F0.imprint","IMPRINT",EDGE,{"disambiguationData":[TD([[makeQuery(id+"F0.imprint","INTERSECT",VERTEX,{"derivedFrom":[subQ3,subQ0]}),1.0]])],"derivedFrom":subQ3})])]})})]});}
            var Q21;
            {var subQ0=sQuery(id+"F0.wireOp",EDGE,"E27.MirrorCS");var subQ1=sQuery(id+"F0.wireOp",EDGE,"E1");var subQ2=makeQuery(id+"F1.opExtrude","SWEPT_EDGE",EDGE,{"disambiguationData":[OSD([subQ1,subQ0])]});var subQ3=sQuery(id+"F0.wireOp",EDGE,"E0");var subQ4=makeQuery(id+"F1.opExtrude","CAP_EDGE",EDGE,{"disambiguationData":[OSD([subQ3])],"isStart":true});Q21=makeQuery(id+"F8.opFillet","BLEND_EDGE",EDGE,{"disambiguationData":[OD(9.0)],"blendedFrom":[makeQuery(id+"F3.opExtrude","CAP_EDGE",EDGE,{"disambiguationData":[OSD([sQuery(id+"F2.wireOp",EDGE,"E29")])],"isStart":true}),makeQuery(id+"F5.boolean.opBoolean","MERGE",FACE,{"derivedFrom":[makeQuery(id+"F1.opExtrude","SWEPT_FACE",FACE,{"disambiguationData":[OSD([subQ1]),TDD([makeQuery(id+"F0.imprint","IMPRINT",EDGE,{"disambiguationData":[TD([[makeQuery(id+"F0.imprint","INTERSECT",VERTEX,{"derivedFrom":[subQ1,sQuery(id+"F0.wireOp",EDGE,"E14.MirrorCS")]}),1.0]])],"derivedFrom":subQ1})])]}),makeQuery(id+"F1.opExtrude","SWEPT_FACE",FACE,{"disambiguationData":[OSD([subQ1]),TDD([makeQuery(id+"F0.imprint","IMPRINT",EDGE,{"disambiguationData":[TD([[makeQuery(id+"F0.imprint","INTERSECT",VERTEX,{"derivedFrom":[subQ1,sQuery(id+"F0.wireOp",EDGE,"E12.MirrorCS")]}),1.0]])],"derivedFrom":subQ1})])]}),makeQuery(id+"F1.opExtrude","SWEPT_FACE",FACE,{"disambiguationData":[OSD([subQ1]),TDD([makeQuery(id+"F0.imprint","IMPRINT",EDGE,{"disambiguationData":[TD([[makeQuery(id+"F0.imprint","INTERSECT",VERTEX,{"derivedFrom":[subQ1,sQuery(id+"F0.wireOp",EDGE,"E3")]}),1.0]])],"derivedFrom":subQ1})])]}),makeQuery(id+"F1.opExtrude","SWEPT_FACE",FACE,{"disambiguationData":[OSD([subQ1]),TDD([makeQuery(id+"F0.imprint","IMPRINT",EDGE,{"disambiguationData":[TD([[makeQuery(id+"F0.imprint","INTERSECT",VERTEX,{"derivedFrom":[subQ1,sQuery(id+"F0.wireOp",EDGE,"E8")]}),1.0]])],"derivedFrom":subQ1})])]}),makeQuery(id+"F1.opExtrude","SWEPT_FACE",FACE,{"disambiguationData":[OSD([subQ1]),TDD([makeQuery(id+"F0.imprint","IMPRINT",EDGE,{"disambiguationData":[TD([[makeQuery(id+"F0.imprint","INTERSECT",VERTEX,{"derivedFrom":[subQ1,sQuery(id+"F0.wireOp",EDGE,"E6")]}),1.0]])],"derivedFrom":subQ1})])]}),makeQuery(id+"F1.opExtrude","SWEPT_FACE",FACE,{"disambiguationData":[OSD([subQ1]),TDD([makeQuery(id+"F0.imprint","IMPRINT",EDGE,{"disambiguationData":[TD([[makeQuery(id+"F0.imprint","INTERSECT",VERTEX,{"derivedFrom":[subQ1,sQuery(id+"F0.wireOp",EDGE,"E5")]}),-1.0]])],"derivedFrom":subQ1})])]}),makeQuery(id+"F1.opExtrude","SWEPT_FACE",FACE,{"disambiguationData":[OSD([subQ1]),TDD([makeQuery(id+"F0.imprint","IMPRINT",EDGE,{"disambiguationData":[TD([[makeQuery(id+"F0.imprint","INTERSECT",VERTEX,{"derivedFrom":[subQ1,sQuery(id+"F0.wireOp",EDGE,"E26.MirrorCS")]}),1.0]])],"derivedFrom":subQ1})])]}),makeQuery(id+"F1.opExtrude","SWEPT_FACE",FACE,{"disambiguationData":[OSD([subQ1]),TDD([makeQuery(id+"F0.imprint","IMPRINT",EDGE,{"disambiguationData":[TD([[makeQuery(id+"F0.imprint","INTERSECT",VERTEX,{"derivedFrom":[subQ1,sQuery(id+"F0.wireOp",EDGE,"E24.MirrorCS")]}),1.0]])],"derivedFrom":subQ1})])]}),makeQuery(id+"F1.opExtrude","SWEPT_FACE",FACE,{"disambiguationData":[OSD([subQ1]),TDD([makeQuery(id+"F0.imprint","IMPRINT",EDGE,{"disambiguationData":[TD([[makeQuery(id+"F0.imprint","INTERSECT",VERTEX,{"derivedFrom":[subQ1,sQuery(id+"F0.wireOp",EDGE,"E22.MirrorCS")]}),1.0]])],"derivedFrom":subQ1})])]}),makeQuery(id+"F1.opExtrude","SWEPT_FACE",FACE,{"disambiguationData":[OSD([subQ1]),TDD([makeQuery(id+"F0.imprint","IMPRINT",EDGE,{"disambiguationData":[TD([[makeQuery(id+"F0.imprint","INTERSECT",VERTEX,{"derivedFrom":[subQ1,sQuery(id+"F0.wireOp",EDGE,"E20.MirrorCS")]}),1.0]])],"derivedFrom":subQ1})])]}),makeQuery(id+"F1.opExtrude","SWEPT_FACE",FACE,{"disambiguationData":[OSD([subQ1]),TDD([makeQuery(id+"F0.imprint","IMPRINT",EDGE,{"disambiguationData":[TD([[makeQuery(id+"F0.imprint","INTERSECT",VERTEX,{"derivedFrom":[subQ1,sQuery(id+"F0.wireOp",EDGE,"E18.MirrorCS")]}),1.0]])],"derivedFrom":subQ1})])]}),makeQuery(id+"F1.opExtrude","SWEPT_FACE",FACE,{"disambiguationData":[OSD([subQ1]),TDD([makeQuery(id+"F0.imprint","IMPRINT",EDGE,{"disambiguationData":[TD([[makeQuery(id+"F0.imprint","INTERSECT",VERTEX,{"derivedFrom":[subQ1,sQuery(id+"F0.wireOp",EDGE,"E17.MirrorCS")]}),-1.0]])],"derivedFrom":subQ1})])]})],"fromTools":[makeQuery(id+"F5.opSweep","SWEPT_FACE",FACE,{"disambiguationData":[OSD([subQ3,subQ1,subQ0]),TDD([subQ4,makeQuery(id+"F4.imprint","IMPRINT",EDGE,{"disambiguationData":[TD([[makeQuery(id+"F4.imprint","INTERSECT",VERTEX,{"derivedFrom":[subQ2,sQuery(id+"F4.wireOp",EDGE,"E30")]}),1.0]])],"derivedFrom":subQ2})])]}),makeQuery(id+"F5.opSweep","SWEPT_FACE",FACE,{"disambiguationData":[OSD([subQ3,subQ1,subQ0]),TDD([subQ4,makeQuery(id+"F4.imprint","IMPRINT",EDGE,{"disambiguationData":[TD([[makeQuery(id+"F4.imprint","INTERSECT",VERTEX,{"derivedFrom":[subQ2,sQuery(id+"F4.wireOp",EDGE,"E32.MirrorCS")]}),1.0]])],"derivedFrom":subQ2})])]}),makeQuery(id+"F5.opSweep","SWEPT_FACE",FACE,{"disambiguationData":[OSD([subQ3,subQ1,subQ0]),TDD([subQ4,makeQuery(id+"F4.imprint","IMPRINT",EDGE,{"disambiguationData":[TD([[makeQuery(id+"F4.imprint","INTERSECT",VERTEX,{"derivedFrom":[subQ2,sQuery(id+"F4.wireOp",EDGE,"E34.MirrorCS")]}),1.0]])],"derivedFrom":subQ2})])]}),makeQuery(id+"F5.opSweep","SWEPT_FACE",FACE,{"disambiguationData":[OSD([subQ3,subQ1,subQ0]),TDD([subQ4,makeQuery(id+"F4.imprint","IMPRINT",EDGE,{"disambiguationData":[TD([[makeQuery(id+"F4.imprint","INTERSECT",VERTEX,{"derivedFrom":[subQ2,sQuery(id+"F4.wireOp",EDGE,"E36.MirrorCS")]}),1.0]])],"derivedFrom":subQ2})])]}),makeQuery(id+"F5.opSweep","SWEPT_FACE",FACE,{"disambiguationData":[OSD([subQ3,subQ1,subQ0]),TDD([subQ4,makeQuery(id+"F4.imprint","IMPRINT",EDGE,{"disambiguationData":[TD([[makeQuery(id+"F4.imprint","INTERSECT",VERTEX,{"derivedFrom":[subQ2,sQuery(id+"F4.wireOp",EDGE,"E38.MirrorCS")]}),1.0]])],"derivedFrom":subQ2})])]}),makeQuery(id+"F5.opSweep","SWEPT_FACE",FACE,{"disambiguationData":[OSD([subQ3,subQ1,subQ0]),TDD([subQ4,makeQuery(id+"F4.imprint","IMPRINT",EDGE,{"disambiguationData":[TD([[makeQuery(id+"F4.imprint","INTERSECT",VERTEX,{"derivedFrom":[subQ2,sQuery(id+"F4.wireOp",EDGE,"E40.MirrorCS")]}),1.0]])],"derivedFrom":subQ2})])]}),makeQuery(id+"F5.opSweep","SWEPT_FACE",FACE,{"disambiguationData":[OSD([subQ3,subQ1,subQ0]),TDD([subQ4,makeQuery(id+"F4.imprint","IMPRINT",EDGE,{"disambiguationData":[TD([[makeQuery(id+"F4.imprint","INTERSECT",VERTEX,{"derivedFrom":[subQ2,sQuery(id+"F4.wireOp",EDGE,"E42.MirrorCS")]}),1.0]])],"derivedFrom":subQ2})])]})]})],"blendedInto":[makeQuery(id+"F5.boolean.opBoolean","MERGE",FACE,{"derivedFrom":[makeQuery(id+"F1.opExtrude","SWEPT_FACE",FACE,{"disambiguationData":[OSD([subQ1]),TDD([makeQuery(id+"F0.imprint","IMPRINT",EDGE,{"disambiguationData":[TD([[makeQuery(id+"F0.imprint","INTERSECT",VERTEX,{"derivedFrom":[subQ1,sQuery(id+"F0.wireOp",EDGE,"E14.MirrorCS")]}),1.0]])],"derivedFrom":subQ1})])]}),makeQuery(id+"F1.opExtrude","SWEPT_FACE",FACE,{"disambiguationData":[OSD([subQ1]),TDD([makeQuery(id+"F0.imprint","IMPRINT",EDGE,{"disambiguationData":[TD([[makeQuery(id+"F0.imprint","INTERSECT",VERTEX,{"derivedFrom":[subQ1,sQuery(id+"F0.wireOp",EDGE,"E12.MirrorCS")]}),1.0]])],"derivedFrom":subQ1})])]}),makeQuery(id+"F1.opExtrude","SWEPT_FACE",FACE,{"disambiguationData":[OSD([subQ1]),TDD([makeQuery(id+"F0.imprint","IMPRINT",EDGE,{"disambiguationData":[TD([[makeQuery(id+"F0.imprint","INTERSECT",VERTEX,{"derivedFrom":[subQ1,sQuery(id+"F0.wireOp",EDGE,"E3")]}),1.0]])],"derivedFrom":subQ1})])]}),makeQuery(id+"F1.opExtrude","SWEPT_FACE",FACE,{"disambiguationData":[OSD([subQ1]),TDD([makeQuery(id+"F0.imprint","IMPRINT",EDGE,{"disambiguationData":[TD([[makeQuery(id+"F0.imprint","INTERSECT",VERTEX,{"derivedFrom":[subQ1,sQuery(id+"F0.wireOp",EDGE,"E8")]}),1.0]])],"derivedFrom":subQ1})])]}),makeQuery(id+"F1.opExtrude","SWEPT_FACE",FACE,{"disambiguationData":[OSD([subQ1]),TDD([makeQuery(id+"F0.imprint","IMPRINT",EDGE,{"disambiguationData":[TD([[makeQuery(id+"F0.imprint","INTERSECT",VERTEX,{"derivedFrom":[subQ1,sQuery(id+"F0.wireOp",EDGE,"E6")]}),1.0]])],"derivedFrom":subQ1})])]}),makeQuery(id+"F1.opExtrude","SWEPT_FACE",FACE,{"disambiguationData":[OSD([subQ1]),TDD([makeQuery(id+"F0.imprint","IMPRINT",EDGE,{"disambiguationData":[TD([[makeQuery(id+"F0.imprint","INTERSECT",VERTEX,{"derivedFrom":[subQ1,sQuery(id+"F0.wireOp",EDGE,"E5")]}),-1.0]])],"derivedFrom":subQ1})])]}),makeQuery(id+"F1.opExtrude","SWEPT_FACE",FACE,{"disambiguationData":[OSD([subQ1]),TDD([makeQuery(id+"F0.imprint","IMPRINT",EDGE,{"disambiguationData":[TD([[makeQuery(id+"F0.imprint","INTERSECT",VERTEX,{"derivedFrom":[subQ1,sQuery(id+"F0.wireOp",EDGE,"E26.MirrorCS")]}),1.0]])],"derivedFrom":subQ1})])]}),makeQuery(id+"F1.opExtrude","SWEPT_FACE",FACE,{"disambiguationData":[OSD([subQ1]),TDD([makeQuery(id+"F0.imprint","IMPRINT",EDGE,{"disambiguationData":[TD([[makeQuery(id+"F0.imprint","INTERSECT",VERTEX,{"derivedFrom":[subQ1,sQuery(id+"F0.wireOp",EDGE,"E24.MirrorCS")]}),1.0]])],"derivedFrom":subQ1})])]}),makeQuery(id+"F1.opExtrude","SWEPT_FACE",FACE,{"disambiguationData":[OSD([subQ1]),TDD([makeQuery(id+"F0.imprint","IMPRINT",EDGE,{"disambiguationData":[TD([[makeQuery(id+"F0.imprint","INTERSECT",VERTEX,{"derivedFrom":[subQ1,sQuery(id+"F0.wireOp",EDGE,"E22.MirrorCS")]}),1.0]])],"derivedFrom":subQ1})])]}),makeQuery(id+"F1.opExtrude","SWEPT_FACE",FACE,{"disambiguationData":[OSD([subQ1]),TDD([makeQuery(id+"F0.imprint","IMPRINT",EDGE,{"disambiguationData":[TD([[makeQuery(id+"F0.imprint","INTERSECT",VERTEX,{"derivedFrom":[subQ1,sQuery(id+"F0.wireOp",EDGE,"E20.MirrorCS")]}),1.0]])],"derivedFrom":subQ1})])]}),makeQuery(id+"F1.opExtrude","SWEPT_FACE",FACE,{"disambiguationData":[OSD([subQ1]),TDD([makeQuery(id+"F0.imprint","IMPRINT",EDGE,{"disambiguationData":[TD([[makeQuery(id+"F0.imprint","INTERSECT",VERTEX,{"derivedFrom":[subQ1,sQuery(id+"F0.wireOp",EDGE,"E18.MirrorCS")]}),1.0]])],"derivedFrom":subQ1})])]}),makeQuery(id+"F1.opExtrude","SWEPT_FACE",FACE,{"disambiguationData":[OSD([subQ1]),TDD([makeQuery(id+"F0.imprint","IMPRINT",EDGE,{"disambiguationData":[TD([[makeQuery(id+"F0.imprint","INTERSECT",VERTEX,{"derivedFrom":[subQ1,sQuery(id+"F0.wireOp",EDGE,"E17.MirrorCS")]}),-1.0]])],"derivedFrom":subQ1})])]})],"fromTools":[makeQuery(id+"F5.opSweep","SWEPT_FACE",FACE,{"disambiguationData":[OSD([subQ3,subQ1,subQ0]),TDD([subQ4,makeQuery(id+"F4.imprint","IMPRINT",EDGE,{"disambiguationData":[TD([[makeQuery(id+"F4.imprint","INTERSECT",VERTEX,{"derivedFrom":[subQ2,sQuery(id+"F4.wireOp",EDGE,"E30")]}),1.0]])],"derivedFrom":subQ2})])]}),makeQuery(id+"F5.opSweep","SWEPT_FACE",FACE,{"disambiguationData":[OSD([subQ3,subQ1,subQ0]),TDD([subQ4,makeQuery(id+"F4.imprint","IMPRINT",EDGE,{"disambiguationData":[TD([[makeQuery(id+"F4.imprint","INTERSECT",VERTEX,{"derivedFrom":[subQ2,sQuery(id+"F4.wireOp",EDGE,"E32.MirrorCS")]}),1.0]])],"derivedFrom":subQ2})])]}),makeQuery(id+"F5.opSweep","SWEPT_FACE",FACE,{"disambiguationData":[OSD([subQ3,subQ1,subQ0]),TDD([subQ4,makeQuery(id+"F4.imprint","IMPRINT",EDGE,{"disambiguationData":[TD([[makeQuery(id+"F4.imprint","INTERSECT",VERTEX,{"derivedFrom":[subQ2,sQuery(id+"F4.wireOp",EDGE,"E34.MirrorCS")]}),1.0]])],"derivedFrom":subQ2})])]}),makeQuery(id+"F5.opSweep","SWEPT_FACE",FACE,{"disambiguationData":[OSD([subQ3,subQ1,subQ0]),TDD([subQ4,makeQuery(id+"F4.imprint","IMPRINT",EDGE,{"disambiguationData":[TD([[makeQuery(id+"F4.imprint","INTERSECT",VERTEX,{"derivedFrom":[subQ2,sQuery(id+"F4.wireOp",EDGE,"E36.MirrorCS")]}),1.0]])],"derivedFrom":subQ2})])]}),makeQuery(id+"F5.opSweep","SWEPT_FACE",FACE,{"disambiguationData":[OSD([subQ3,subQ1,subQ0]),TDD([subQ4,makeQuery(id+"F4.imprint","IMPRINT",EDGE,{"disambiguationData":[TD([[makeQuery(id+"F4.imprint","INTERSECT",VERTEX,{"derivedFrom":[subQ2,sQuery(id+"F4.wireOp",EDGE,"E38.MirrorCS")]}),1.0]])],"derivedFrom":subQ2})])]}),makeQuery(id+"F5.opSweep","SWEPT_FACE",FACE,{"disambiguationData":[OSD([subQ3,subQ1,subQ0]),TDD([subQ4,makeQuery(id+"F4.imprint","IMPRINT",EDGE,{"disambiguationData":[TD([[makeQuery(id+"F4.imprint","INTERSECT",VERTEX,{"derivedFrom":[subQ2,sQuery(id+"F4.wireOp",EDGE,"E40.MirrorCS")]}),1.0]])],"derivedFrom":subQ2})])]}),makeQuery(id+"F5.opSweep","SWEPT_FACE",FACE,{"disambiguationData":[OSD([subQ3,subQ1,subQ0]),TDD([subQ4,makeQuery(id+"F4.imprint","IMPRINT",EDGE,{"disambiguationData":[TD([[makeQuery(id+"F4.imprint","INTERSECT",VERTEX,{"derivedFrom":[subQ2,sQuery(id+"F4.wireOp",EDGE,"E42.MirrorCS")]}),1.0]])],"derivedFrom":subQ2})])]})]})]});}
            var Q22;
            {var subQ0=sQuery(id+"F0.wireOp",EDGE,"E21.MirrorCS");var subQ2=sQuery(id+"F2.wireOp",EDGE,"E29");var subQ3=sQuery(id+"F0.wireOp",EDGE,"E2");Q22=makeQuery(id+"F8.opFillet","BLEND_EDGE",EDGE,{"blendedFrom":[makeQuery(id+"F3.opExtrude","CAP_EDGE",EDGE,{"disambiguationData":[OSD([subQ2])],"isStart":true}),makeQuery(id+"F5.boolean.opBoolean","SPLIT",FACE,{"disambiguationData":[TD([makeQuery(id+"F3.opExtrude","CAP_FACE",FACE,{"disambiguationData":[OSD([subQ2])],"isStart":true})])],"derivedFrom":makeQuery(id+"F1.opExtrude","SWEPT_FACE",FACE,{"disambiguationData":[OSD([subQ3]),TDD([makeQuery(id+"F0.imprint","IMPRINT",EDGE,{"disambiguationData":[TD([[makeQuery(id+"F0.imprint","INTERSECT",VERTEX,{"derivedFrom":[subQ3,subQ0]}),1.0]])],"derivedFrom":subQ3})])]})})],"blendedInto":[makeQuery(id+"F5.boolean.opBoolean","SPLIT",FACE,{"disambiguationData":[TD([makeQuery(id+"F3.opExtrude","CAP_FACE",FACE,{"disambiguationData":[OSD([subQ2])],"isStart":true})])],"derivedFrom":makeQuery(id+"F1.opExtrude","SWEPT_FACE",FACE,{"disambiguationData":[OSD([subQ3]),TDD([makeQuery(id+"F0.imprint","IMPRINT",EDGE,{"disambiguationData":[TD([[makeQuery(id+"F0.imprint","INTERSECT",VERTEX,{"derivedFrom":[subQ3,subQ0]}),1.0]])],"derivedFrom":subQ3})])]})})]});}
            var Q23;
            {var subQ0=sQuery(id+"F0.wireOp",EDGE,"E27.MirrorCS");var subQ1=sQuery(id+"F0.wireOp",EDGE,"E1");var subQ2=makeQuery(id+"F1.opExtrude","SWEPT_EDGE",EDGE,{"disambiguationData":[OSD([subQ1,subQ0])]});var subQ3=sQuery(id+"F0.wireOp",EDGE,"E0");var subQ4=makeQuery(id+"F1.opExtrude","CAP_EDGE",EDGE,{"disambiguationData":[OSD([subQ3])],"isStart":true});Q23=makeQuery(id+"F8.opFillet","BLEND_EDGE",EDGE,{"disambiguationData":[OD(8.0)],"blendedFrom":[makeQuery(id+"F3.opExtrude","CAP_EDGE",EDGE,{"disambiguationData":[OSD([sQuery(id+"F2.wireOp",EDGE,"E29")])],"isStart":true}),makeQuery(id+"F5.boolean.opBoolean","MERGE",FACE,{"derivedFrom":[makeQuery(id+"F1.opExtrude","SWEPT_FACE",FACE,{"disambiguationData":[OSD([subQ1]),TDD([makeQuery(id+"F0.imprint","IMPRINT",EDGE,{"disambiguationData":[TD([[makeQuery(id+"F0.imprint","INTERSECT",VERTEX,{"derivedFrom":[subQ1,sQuery(id+"F0.wireOp",EDGE,"E14.MirrorCS")]}),1.0]])],"derivedFrom":subQ1})])]}),makeQuery(id+"F1.opExtrude","SWEPT_FACE",FACE,{"disambiguationData":[OSD([subQ1]),TDD([makeQuery(id+"F0.imprint","IMPRINT",EDGE,{"disambiguationData":[TD([[makeQuery(id+"F0.imprint","INTERSECT",VERTEX,{"derivedFrom":[subQ1,sQuery(id+"F0.wireOp",EDGE,"E12.MirrorCS")]}),1.0]])],"derivedFrom":subQ1})])]}),makeQuery(id+"F1.opExtrude","SWEPT_FACE",FACE,{"disambiguationData":[OSD([subQ1]),TDD([makeQuery(id+"F0.imprint","IMPRINT",EDGE,{"disambiguationData":[TD([[makeQuery(id+"F0.imprint","INTERSECT",VERTEX,{"derivedFrom":[subQ1,sQuery(id+"F0.wireOp",EDGE,"E3")]}),1.0]])],"derivedFrom":subQ1})])]}),makeQuery(id+"F1.opExtrude","SWEPT_FACE",FACE,{"disambiguationData":[OSD([subQ1]),TDD([makeQuery(id+"F0.imprint","IMPRINT",EDGE,{"disambiguationData":[TD([[makeQuery(id+"F0.imprint","INTERSECT",VERTEX,{"derivedFrom":[subQ1,sQuery(id+"F0.wireOp",EDGE,"E8")]}),1.0]])],"derivedFrom":subQ1})])]}),makeQuery(id+"F1.opExtrude","SWEPT_FACE",FACE,{"disambiguationData":[OSD([subQ1]),TDD([makeQuery(id+"F0.imprint","IMPRINT",EDGE,{"disambiguationData":[TD([[makeQuery(id+"F0.imprint","INTERSECT",VERTEX,{"derivedFrom":[subQ1,sQuery(id+"F0.wireOp",EDGE,"E6")]}),1.0]])],"derivedFrom":subQ1})])]}),makeQuery(id+"F1.opExtrude","SWEPT_FACE",FACE,{"disambiguationData":[OSD([subQ1]),TDD([makeQuery(id+"F0.imprint","IMPRINT",EDGE,{"disambiguationData":[TD([[makeQuery(id+"F0.imprint","INTERSECT",VERTEX,{"derivedFrom":[subQ1,sQuery(id+"F0.wireOp",EDGE,"E5")]}),-1.0]])],"derivedFrom":subQ1})])]}),makeQuery(id+"F1.opExtrude","SWEPT_FACE",FACE,{"disambiguationData":[OSD([subQ1]),TDD([makeQuery(id+"F0.imprint","IMPRINT",EDGE,{"disambiguationData":[TD([[makeQuery(id+"F0.imprint","INTERSECT",VERTEX,{"derivedFrom":[subQ1,sQuery(id+"F0.wireOp",EDGE,"E26.MirrorCS")]}),1.0]])],"derivedFrom":subQ1})])]}),makeQuery(id+"F1.opExtrude","SWEPT_FACE",FACE,{"disambiguationData":[OSD([subQ1]),TDD([makeQuery(id+"F0.imprint","IMPRINT",EDGE,{"disambiguationData":[TD([[makeQuery(id+"F0.imprint","INTERSECT",VERTEX,{"derivedFrom":[subQ1,sQuery(id+"F0.wireOp",EDGE,"E24.MirrorCS")]}),1.0]])],"derivedFrom":subQ1})])]}),makeQuery(id+"F1.opExtrude","SWEPT_FACE",FACE,{"disambiguationData":[OSD([subQ1]),TDD([makeQuery(id+"F0.imprint","IMPRINT",EDGE,{"disambiguationData":[TD([[makeQuery(id+"F0.imprint","INTERSECT",VERTEX,{"derivedFrom":[subQ1,sQuery(id+"F0.wireOp",EDGE,"E22.MirrorCS")]}),1.0]])],"derivedFrom":subQ1})])]}),makeQuery(id+"F1.opExtrude","SWEPT_FACE",FACE,{"disambiguationData":[OSD([subQ1]),TDD([makeQuery(id+"F0.imprint","IMPRINT",EDGE,{"disambiguationData":[TD([[makeQuery(id+"F0.imprint","INTERSECT",VERTEX,{"derivedFrom":[subQ1,sQuery(id+"F0.wireOp",EDGE,"E20.MirrorCS")]}),1.0]])],"derivedFrom":subQ1})])]}),makeQuery(id+"F1.opExtrude","SWEPT_FACE",FACE,{"disambiguationData":[OSD([subQ1]),TDD([makeQuery(id+"F0.imprint","IMPRINT",EDGE,{"disambiguationData":[TD([[makeQuery(id+"F0.imprint","INTERSECT",VERTEX,{"derivedFrom":[subQ1,sQuery(id+"F0.wireOp",EDGE,"E18.MirrorCS")]}),1.0]])],"derivedFrom":subQ1})])]}),makeQuery(id+"F1.opExtrude","SWEPT_FACE",FACE,{"disambiguationData":[OSD([subQ1]),TDD([makeQuery(id+"F0.imprint","IMPRINT",EDGE,{"disambiguationData":[TD([[makeQuery(id+"F0.imprint","INTERSECT",VERTEX,{"derivedFrom":[subQ1,sQuery(id+"F0.wireOp",EDGE,"E17.MirrorCS")]}),-1.0]])],"derivedFrom":subQ1})])]})],"fromTools":[makeQuery(id+"F5.opSweep","SWEPT_FACE",FACE,{"disambiguationData":[OSD([subQ3,subQ1,subQ0]),TDD([subQ4,makeQuery(id+"F4.imprint","IMPRINT",EDGE,{"disambiguationData":[TD([[makeQuery(id+"F4.imprint","INTERSECT",VERTEX,{"derivedFrom":[subQ2,sQuery(id+"F4.wireOp",EDGE,"E30")]}),1.0]])],"derivedFrom":subQ2})])]}),makeQuery(id+"F5.opSweep","SWEPT_FACE",FACE,{"disambiguationData":[OSD([subQ3,subQ1,subQ0]),TDD([subQ4,makeQuery(id+"F4.imprint","IMPRINT",EDGE,{"disambiguationData":[TD([[makeQuery(id+"F4.imprint","INTERSECT",VERTEX,{"derivedFrom":[subQ2,sQuery(id+"F4.wireOp",EDGE,"E32.MirrorCS")]}),1.0]])],"derivedFrom":subQ2})])]}),makeQuery(id+"F5.opSweep","SWEPT_FACE",FACE,{"disambiguationData":[OSD([subQ3,subQ1,subQ0]),TDD([subQ4,makeQuery(id+"F4.imprint","IMPRINT",EDGE,{"disambiguationData":[TD([[makeQuery(id+"F4.imprint","INTERSECT",VERTEX,{"derivedFrom":[subQ2,sQuery(id+"F4.wireOp",EDGE,"E34.MirrorCS")]}),1.0]])],"derivedFrom":subQ2})])]}),makeQuery(id+"F5.opSweep","SWEPT_FACE",FACE,{"disambiguationData":[OSD([subQ3,subQ1,subQ0]),TDD([subQ4,makeQuery(id+"F4.imprint","IMPRINT",EDGE,{"disambiguationData":[TD([[makeQuery(id+"F4.imprint","INTERSECT",VERTEX,{"derivedFrom":[subQ2,sQuery(id+"F4.wireOp",EDGE,"E36.MirrorCS")]}),1.0]])],"derivedFrom":subQ2})])]}),makeQuery(id+"F5.opSweep","SWEPT_FACE",FACE,{"disambiguationData":[OSD([subQ3,subQ1,subQ0]),TDD([subQ4,makeQuery(id+"F4.imprint","IMPRINT",EDGE,{"disambiguationData":[TD([[makeQuery(id+"F4.imprint","INTERSECT",VERTEX,{"derivedFrom":[subQ2,sQuery(id+"F4.wireOp",EDGE,"E38.MirrorCS")]}),1.0]])],"derivedFrom":subQ2})])]}),makeQuery(id+"F5.opSweep","SWEPT_FACE",FACE,{"disambiguationData":[OSD([subQ3,subQ1,subQ0]),TDD([subQ4,makeQuery(id+"F4.imprint","IMPRINT",EDGE,{"disambiguationData":[TD([[makeQuery(id+"F4.imprint","INTERSECT",VERTEX,{"derivedFrom":[subQ2,sQuery(id+"F4.wireOp",EDGE,"E40.MirrorCS")]}),1.0]])],"derivedFrom":subQ2})])]}),makeQuery(id+"F5.opSweep","SWEPT_FACE",FACE,{"disambiguationData":[OSD([subQ3,subQ1,subQ0]),TDD([subQ4,makeQuery(id+"F4.imprint","IMPRINT",EDGE,{"disambiguationData":[TD([[makeQuery(id+"F4.imprint","INTERSECT",VERTEX,{"derivedFrom":[subQ2,sQuery(id+"F4.wireOp",EDGE,"E42.MirrorCS")]}),1.0]])],"derivedFrom":subQ2})])]})]})],"blendedInto":[makeQuery(id+"F5.boolean.opBoolean","MERGE",FACE,{"derivedFrom":[makeQuery(id+"F1.opExtrude","SWEPT_FACE",FACE,{"disambiguationData":[OSD([subQ1]),TDD([makeQuery(id+"F0.imprint","IMPRINT",EDGE,{"disambiguationData":[TD([[makeQuery(id+"F0.imprint","INTERSECT",VERTEX,{"derivedFrom":[subQ1,sQuery(id+"F0.wireOp",EDGE,"E14.MirrorCS")]}),1.0]])],"derivedFrom":subQ1})])]}),makeQuery(id+"F1.opExtrude","SWEPT_FACE",FACE,{"disambiguationData":[OSD([subQ1]),TDD([makeQuery(id+"F0.imprint","IMPRINT",EDGE,{"disambiguationData":[TD([[makeQuery(id+"F0.imprint","INTERSECT",VERTEX,{"derivedFrom":[subQ1,sQuery(id+"F0.wireOp",EDGE,"E12.MirrorCS")]}),1.0]])],"derivedFrom":subQ1})])]}),makeQuery(id+"F1.opExtrude","SWEPT_FACE",FACE,{"disambiguationData":[OSD([subQ1]),TDD([makeQuery(id+"F0.imprint","IMPRINT",EDGE,{"disambiguationData":[TD([[makeQuery(id+"F0.imprint","INTERSECT",VERTEX,{"derivedFrom":[subQ1,sQuery(id+"F0.wireOp",EDGE,"E3")]}),1.0]])],"derivedFrom":subQ1})])]}),makeQuery(id+"F1.opExtrude","SWEPT_FACE",FACE,{"disambiguationData":[OSD([subQ1]),TDD([makeQuery(id+"F0.imprint","IMPRINT",EDGE,{"disambiguationData":[TD([[makeQuery(id+"F0.imprint","INTERSECT",VERTEX,{"derivedFrom":[subQ1,sQuery(id+"F0.wireOp",EDGE,"E8")]}),1.0]])],"derivedFrom":subQ1})])]}),makeQuery(id+"F1.opExtrude","SWEPT_FACE",FACE,{"disambiguationData":[OSD([subQ1]),TDD([makeQuery(id+"F0.imprint","IMPRINT",EDGE,{"disambiguationData":[TD([[makeQuery(id+"F0.imprint","INTERSECT",VERTEX,{"derivedFrom":[subQ1,sQuery(id+"F0.wireOp",EDGE,"E6")]}),1.0]])],"derivedFrom":subQ1})])]}),makeQuery(id+"F1.opExtrude","SWEPT_FACE",FACE,{"disambiguationData":[OSD([subQ1]),TDD([makeQuery(id+"F0.imprint","IMPRINT",EDGE,{"disambiguationData":[TD([[makeQuery(id+"F0.imprint","INTERSECT",VERTEX,{"derivedFrom":[subQ1,sQuery(id+"F0.wireOp",EDGE,"E5")]}),-1.0]])],"derivedFrom":subQ1})])]}),makeQuery(id+"F1.opExtrude","SWEPT_FACE",FACE,{"disambiguationData":[OSD([subQ1]),TDD([makeQuery(id+"F0.imprint","IMPRINT",EDGE,{"disambiguationData":[TD([[makeQuery(id+"F0.imprint","INTERSECT",VERTEX,{"derivedFrom":[subQ1,sQuery(id+"F0.wireOp",EDGE,"E26.MirrorCS")]}),1.0]])],"derivedFrom":subQ1})])]}),makeQuery(id+"F1.opExtrude","SWEPT_FACE",FACE,{"disambiguationData":[OSD([subQ1]),TDD([makeQuery(id+"F0.imprint","IMPRINT",EDGE,{"disambiguationData":[TD([[makeQuery(id+"F0.imprint","INTERSECT",VERTEX,{"derivedFrom":[subQ1,sQuery(id+"F0.wireOp",EDGE,"E24.MirrorCS")]}),1.0]])],"derivedFrom":subQ1})])]}),makeQuery(id+"F1.opExtrude","SWEPT_FACE",FACE,{"disambiguationData":[OSD([subQ1]),TDD([makeQuery(id+"F0.imprint","IMPRINT",EDGE,{"disambiguationData":[TD([[makeQuery(id+"F0.imprint","INTERSECT",VERTEX,{"derivedFrom":[subQ1,sQuery(id+"F0.wireOp",EDGE,"E22.MirrorCS")]}),1.0]])],"derivedFrom":subQ1})])]}),makeQuery(id+"F1.opExtrude","SWEPT_FACE",FACE,{"disambiguationData":[OSD([subQ1]),TDD([makeQuery(id+"F0.imprint","IMPRINT",EDGE,{"disambiguationData":[TD([[makeQuery(id+"F0.imprint","INTERSECT",VERTEX,{"derivedFrom":[subQ1,sQuery(id+"F0.wireOp",EDGE,"E20.MirrorCS")]}),1.0]])],"derivedFrom":subQ1})])]}),makeQuery(id+"F1.opExtrude","SWEPT_FACE",FACE,{"disambiguationData":[OSD([subQ1]),TDD([makeQuery(id+"F0.imprint","IMPRINT",EDGE,{"disambiguationData":[TD([[makeQuery(id+"F0.imprint","INTERSECT",VERTEX,{"derivedFrom":[subQ1,sQuery(id+"F0.wireOp",EDGE,"E18.MirrorCS")]}),1.0]])],"derivedFrom":subQ1})])]}),makeQuery(id+"F1.opExtrude","SWEPT_FACE",FACE,{"disambiguationData":[OSD([subQ1]),TDD([makeQuery(id+"F0.imprint","IMPRINT",EDGE,{"disambiguationData":[TD([[makeQuery(id+"F0.imprint","INTERSECT",VERTEX,{"derivedFrom":[subQ1,sQuery(id+"F0.wireOp",EDGE,"E17.MirrorCS")]}),-1.0]])],"derivedFrom":subQ1})])]})],"fromTools":[makeQuery(id+"F5.opSweep","SWEPT_FACE",FACE,{"disambiguationData":[OSD([subQ3,subQ1,subQ0]),TDD([subQ4,makeQuery(id+"F4.imprint","IMPRINT",EDGE,{"disambiguationData":[TD([[makeQuery(id+"F4.imprint","INTERSECT",VERTEX,{"derivedFrom":[subQ2,sQuery(id+"F4.wireOp",EDGE,"E30")]}),1.0]])],"derivedFrom":subQ2})])]}),makeQuery(id+"F5.opSweep","SWEPT_FACE",FACE,{"disambiguationData":[OSD([subQ3,subQ1,subQ0]),TDD([subQ4,makeQuery(id+"F4.imprint","IMPRINT",EDGE,{"disambiguationData":[TD([[makeQuery(id+"F4.imprint","INTERSECT",VERTEX,{"derivedFrom":[subQ2,sQuery(id+"F4.wireOp",EDGE,"E32.MirrorCS")]}),1.0]])],"derivedFrom":subQ2})])]}),makeQuery(id+"F5.opSweep","SWEPT_FACE",FACE,{"disambiguationData":[OSD([subQ3,subQ1,subQ0]),TDD([subQ4,makeQuery(id+"F4.imprint","IMPRINT",EDGE,{"disambiguationData":[TD([[makeQuery(id+"F4.imprint","INTERSECT",VERTEX,{"derivedFrom":[subQ2,sQuery(id+"F4.wireOp",EDGE,"E34.MirrorCS")]}),1.0]])],"derivedFrom":subQ2})])]}),makeQuery(id+"F5.opSweep","SWEPT_FACE",FACE,{"disambiguationData":[OSD([subQ3,subQ1,subQ0]),TDD([subQ4,makeQuery(id+"F4.imprint","IMPRINT",EDGE,{"disambiguationData":[TD([[makeQuery(id+"F4.imprint","INTERSECT",VERTEX,{"derivedFrom":[subQ2,sQuery(id+"F4.wireOp",EDGE,"E36.MirrorCS")]}),1.0]])],"derivedFrom":subQ2})])]}),makeQuery(id+"F5.opSweep","SWEPT_FACE",FACE,{"disambiguationData":[OSD([subQ3,subQ1,subQ0]),TDD([subQ4,makeQuery(id+"F4.imprint","IMPRINT",EDGE,{"disambiguationData":[TD([[makeQuery(id+"F4.imprint","INTERSECT",VERTEX,{"derivedFrom":[subQ2,sQuery(id+"F4.wireOp",EDGE,"E38.MirrorCS")]}),1.0]])],"derivedFrom":subQ2})])]}),makeQuery(id+"F5.opSweep","SWEPT_FACE",FACE,{"disambiguationData":[OSD([subQ3,subQ1,subQ0]),TDD([subQ4,makeQuery(id+"F4.imprint","IMPRINT",EDGE,{"disambiguationData":[TD([[makeQuery(id+"F4.imprint","INTERSECT",VERTEX,{"derivedFrom":[subQ2,sQuery(id+"F4.wireOp",EDGE,"E40.MirrorCS")]}),1.0]])],"derivedFrom":subQ2})])]}),makeQuery(id+"F5.opSweep","SWEPT_FACE",FACE,{"disambiguationData":[OSD([subQ3,subQ1,subQ0]),TDD([subQ4,makeQuery(id+"F4.imprint","IMPRINT",EDGE,{"disambiguationData":[TD([[makeQuery(id+"F4.imprint","INTERSECT",VERTEX,{"derivedFrom":[subQ2,sQuery(id+"F4.wireOp",EDGE,"E42.MirrorCS")]}),1.0]])],"derivedFrom":subQ2})])]})]})]});}
            var Q24;
            {var subQ0=sQuery(id+"F0.wireOp",EDGE,"E19.MirrorCS");var subQ2=sQuery(id+"F2.wireOp",EDGE,"E29");var subQ3=sQuery(id+"F0.wireOp",EDGE,"E2");Q24=makeQuery(id+"F8.opFillet","BLEND_EDGE",EDGE,{"blendedFrom":[makeQuery(id+"F3.opExtrude","CAP_EDGE",EDGE,{"disambiguationData":[OSD([subQ2])],"isStart":true}),makeQuery(id+"F5.boolean.opBoolean","SPLIT",FACE,{"disambiguationData":[TD([makeQuery(id+"F3.opExtrude","CAP_FACE",FACE,{"disambiguationData":[OSD([subQ2])],"isStart":true})])],"derivedFrom":makeQuery(id+"F1.opExtrude","SWEPT_FACE",FACE,{"disambiguationData":[OSD([subQ3]),TDD([makeQuery(id+"F0.imprint","IMPRINT",EDGE,{"disambiguationData":[TD([[makeQuery(id+"F0.imprint","INTERSECT",VERTEX,{"derivedFrom":[subQ3,subQ0]}),1.0]])],"derivedFrom":subQ3})])]})})],"blendedInto":[makeQuery(id+"F5.boolean.opBoolean","SPLIT",FACE,{"disambiguationData":[TD([makeQuery(id+"F3.opExtrude","CAP_FACE",FACE,{"disambiguationData":[OSD([subQ2])],"isStart":true})])],"derivedFrom":makeQuery(id+"F1.opExtrude","SWEPT_FACE",FACE,{"disambiguationData":[OSD([subQ3]),TDD([makeQuery(id+"F0.imprint","IMPRINT",EDGE,{"disambiguationData":[TD([[makeQuery(id+"F0.imprint","INTERSECT",VERTEX,{"derivedFrom":[subQ3,subQ0]}),1.0]])],"derivedFrom":subQ3})])]})})]});}
            var Q25;
            {var subQ0=sQuery(id+"F0.wireOp",EDGE,"E27.MirrorCS");var subQ1=sQuery(id+"F0.wireOp",EDGE,"E1");var subQ2=makeQuery(id+"F1.opExtrude","SWEPT_EDGE",EDGE,{"disambiguationData":[OSD([subQ1,subQ0])]});var subQ3=sQuery(id+"F0.wireOp",EDGE,"E0");var subQ4=makeQuery(id+"F1.opExtrude","CAP_EDGE",EDGE,{"disambiguationData":[OSD([subQ3])],"isStart":true});Q25=makeQuery(id+"F8.opFillet","BLEND_EDGE",EDGE,{"disambiguationData":[OD(7.0)],"blendedFrom":[makeQuery(id+"F3.opExtrude","CAP_EDGE",EDGE,{"disambiguationData":[OSD([sQuery(id+"F2.wireOp",EDGE,"E29")])],"isStart":true}),makeQuery(id+"F5.boolean.opBoolean","MERGE",FACE,{"derivedFrom":[makeQuery(id+"F1.opExtrude","SWEPT_FACE",FACE,{"disambiguationData":[OSD([subQ1]),TDD([makeQuery(id+"F0.imprint","IMPRINT",EDGE,{"disambiguationData":[TD([[makeQuery(id+"F0.imprint","INTERSECT",VERTEX,{"derivedFrom":[subQ1,sQuery(id+"F0.wireOp",EDGE,"E14.MirrorCS")]}),1.0]])],"derivedFrom":subQ1})])]}),makeQuery(id+"F1.opExtrude","SWEPT_FACE",FACE,{"disambiguationData":[OSD([subQ1]),TDD([makeQuery(id+"F0.imprint","IMPRINT",EDGE,{"disambiguationData":[TD([[makeQuery(id+"F0.imprint","INTERSECT",VERTEX,{"derivedFrom":[subQ1,sQuery(id+"F0.wireOp",EDGE,"E12.MirrorCS")]}),1.0]])],"derivedFrom":subQ1})])]}),makeQuery(id+"F1.opExtrude","SWEPT_FACE",FACE,{"disambiguationData":[OSD([subQ1]),TDD([makeQuery(id+"F0.imprint","IMPRINT",EDGE,{"disambiguationData":[TD([[makeQuery(id+"F0.imprint","INTERSECT",VERTEX,{"derivedFrom":[subQ1,sQuery(id+"F0.wireOp",EDGE,"E3")]}),1.0]])],"derivedFrom":subQ1})])]}),makeQuery(id+"F1.opExtrude","SWEPT_FACE",FACE,{"disambiguationData":[OSD([subQ1]),TDD([makeQuery(id+"F0.imprint","IMPRINT",EDGE,{"disambiguationData":[TD([[makeQuery(id+"F0.imprint","INTERSECT",VERTEX,{"derivedFrom":[subQ1,sQuery(id+"F0.wireOp",EDGE,"E8")]}),1.0]])],"derivedFrom":subQ1})])]}),makeQuery(id+"F1.opExtrude","SWEPT_FACE",FACE,{"disambiguationData":[OSD([subQ1]),TDD([makeQuery(id+"F0.imprint","IMPRINT",EDGE,{"disambiguationData":[TD([[makeQuery(id+"F0.imprint","INTERSECT",VERTEX,{"derivedFrom":[subQ1,sQuery(id+"F0.wireOp",EDGE,"E6")]}),1.0]])],"derivedFrom":subQ1})])]}),makeQuery(id+"F1.opExtrude","SWEPT_FACE",FACE,{"disambiguationData":[OSD([subQ1]),TDD([makeQuery(id+"F0.imprint","IMPRINT",EDGE,{"disambiguationData":[TD([[makeQuery(id+"F0.imprint","INTERSECT",VERTEX,{"derivedFrom":[subQ1,sQuery(id+"F0.wireOp",EDGE,"E5")]}),-1.0]])],"derivedFrom":subQ1})])]}),makeQuery(id+"F1.opExtrude","SWEPT_FACE",FACE,{"disambiguationData":[OSD([subQ1]),TDD([makeQuery(id+"F0.imprint","IMPRINT",EDGE,{"disambiguationData":[TD([[makeQuery(id+"F0.imprint","INTERSECT",VERTEX,{"derivedFrom":[subQ1,sQuery(id+"F0.wireOp",EDGE,"E26.MirrorCS")]}),1.0]])],"derivedFrom":subQ1})])]}),makeQuery(id+"F1.opExtrude","SWEPT_FACE",FACE,{"disambiguationData":[OSD([subQ1]),TDD([makeQuery(id+"F0.imprint","IMPRINT",EDGE,{"disambiguationData":[TD([[makeQuery(id+"F0.imprint","INTERSECT",VERTEX,{"derivedFrom":[subQ1,sQuery(id+"F0.wireOp",EDGE,"E24.MirrorCS")]}),1.0]])],"derivedFrom":subQ1})])]}),makeQuery(id+"F1.opExtrude","SWEPT_FACE",FACE,{"disambiguationData":[OSD([subQ1]),TDD([makeQuery(id+"F0.imprint","IMPRINT",EDGE,{"disambiguationData":[TD([[makeQuery(id+"F0.imprint","INTERSECT",VERTEX,{"derivedFrom":[subQ1,sQuery(id+"F0.wireOp",EDGE,"E22.MirrorCS")]}),1.0]])],"derivedFrom":subQ1})])]}),makeQuery(id+"F1.opExtrude","SWEPT_FACE",FACE,{"disambiguationData":[OSD([subQ1]),TDD([makeQuery(id+"F0.imprint","IMPRINT",EDGE,{"disambiguationData":[TD([[makeQuery(id+"F0.imprint","INTERSECT",VERTEX,{"derivedFrom":[subQ1,sQuery(id+"F0.wireOp",EDGE,"E20.MirrorCS")]}),1.0]])],"derivedFrom":subQ1})])]}),makeQuery(id+"F1.opExtrude","SWEPT_FACE",FACE,{"disambiguationData":[OSD([subQ1]),TDD([makeQuery(id+"F0.imprint","IMPRINT",EDGE,{"disambiguationData":[TD([[makeQuery(id+"F0.imprint","INTERSECT",VERTEX,{"derivedFrom":[subQ1,sQuery(id+"F0.wireOp",EDGE,"E18.MirrorCS")]}),1.0]])],"derivedFrom":subQ1})])]}),makeQuery(id+"F1.opExtrude","SWEPT_FACE",FACE,{"disambiguationData":[OSD([subQ1]),TDD([makeQuery(id+"F0.imprint","IMPRINT",EDGE,{"disambiguationData":[TD([[makeQuery(id+"F0.imprint","INTERSECT",VERTEX,{"derivedFrom":[subQ1,sQuery(id+"F0.wireOp",EDGE,"E17.MirrorCS")]}),-1.0]])],"derivedFrom":subQ1})])]})],"fromTools":[makeQuery(id+"F5.opSweep","SWEPT_FACE",FACE,{"disambiguationData":[OSD([subQ3,subQ1,subQ0]),TDD([subQ4,makeQuery(id+"F4.imprint","IMPRINT",EDGE,{"disambiguationData":[TD([[makeQuery(id+"F4.imprint","INTERSECT",VERTEX,{"derivedFrom":[subQ2,sQuery(id+"F4.wireOp",EDGE,"E30")]}),1.0]])],"derivedFrom":subQ2})])]}),makeQuery(id+"F5.opSweep","SWEPT_FACE",FACE,{"disambiguationData":[OSD([subQ3,subQ1,subQ0]),TDD([subQ4,makeQuery(id+"F4.imprint","IMPRINT",EDGE,{"disambiguationData":[TD([[makeQuery(id+"F4.imprint","INTERSECT",VERTEX,{"derivedFrom":[subQ2,sQuery(id+"F4.wireOp",EDGE,"E32.MirrorCS")]}),1.0]])],"derivedFrom":subQ2})])]}),makeQuery(id+"F5.opSweep","SWEPT_FACE",FACE,{"disambiguationData":[OSD([subQ3,subQ1,subQ0]),TDD([subQ4,makeQuery(id+"F4.imprint","IMPRINT",EDGE,{"disambiguationData":[TD([[makeQuery(id+"F4.imprint","INTERSECT",VERTEX,{"derivedFrom":[subQ2,sQuery(id+"F4.wireOp",EDGE,"E34.MirrorCS")]}),1.0]])],"derivedFrom":subQ2})])]}),makeQuery(id+"F5.opSweep","SWEPT_FACE",FACE,{"disambiguationData":[OSD([subQ3,subQ1,subQ0]),TDD([subQ4,makeQuery(id+"F4.imprint","IMPRINT",EDGE,{"disambiguationData":[TD([[makeQuery(id+"F4.imprint","INTERSECT",VERTEX,{"derivedFrom":[subQ2,sQuery(id+"F4.wireOp",EDGE,"E36.MirrorCS")]}),1.0]])],"derivedFrom":subQ2})])]}),makeQuery(id+"F5.opSweep","SWEPT_FACE",FACE,{"disambiguationData":[OSD([subQ3,subQ1,subQ0]),TDD([subQ4,makeQuery(id+"F4.imprint","IMPRINT",EDGE,{"disambiguationData":[TD([[makeQuery(id+"F4.imprint","INTERSECT",VERTEX,{"derivedFrom":[subQ2,sQuery(id+"F4.wireOp",EDGE,"E38.MirrorCS")]}),1.0]])],"derivedFrom":subQ2})])]}),makeQuery(id+"F5.opSweep","SWEPT_FACE",FACE,{"disambiguationData":[OSD([subQ3,subQ1,subQ0]),TDD([subQ4,makeQuery(id+"F4.imprint","IMPRINT",EDGE,{"disambiguationData":[TD([[makeQuery(id+"F4.imprint","INTERSECT",VERTEX,{"derivedFrom":[subQ2,sQuery(id+"F4.wireOp",EDGE,"E40.MirrorCS")]}),1.0]])],"derivedFrom":subQ2})])]}),makeQuery(id+"F5.opSweep","SWEPT_FACE",FACE,{"disambiguationData":[OSD([subQ3,subQ1,subQ0]),TDD([subQ4,makeQuery(id+"F4.imprint","IMPRINT",EDGE,{"disambiguationData":[TD([[makeQuery(id+"F4.imprint","INTERSECT",VERTEX,{"derivedFrom":[subQ2,sQuery(id+"F4.wireOp",EDGE,"E42.MirrorCS")]}),1.0]])],"derivedFrom":subQ2})])]})]})],"blendedInto":[makeQuery(id+"F5.boolean.opBoolean","MERGE",FACE,{"derivedFrom":[makeQuery(id+"F1.opExtrude","SWEPT_FACE",FACE,{"disambiguationData":[OSD([subQ1]),TDD([makeQuery(id+"F0.imprint","IMPRINT",EDGE,{"disambiguationData":[TD([[makeQuery(id+"F0.imprint","INTERSECT",VERTEX,{"derivedFrom":[subQ1,sQuery(id+"F0.wireOp",EDGE,"E14.MirrorCS")]}),1.0]])],"derivedFrom":subQ1})])]}),makeQuery(id+"F1.opExtrude","SWEPT_FACE",FACE,{"disambiguationData":[OSD([subQ1]),TDD([makeQuery(id+"F0.imprint","IMPRINT",EDGE,{"disambiguationData":[TD([[makeQuery(id+"F0.imprint","INTERSECT",VERTEX,{"derivedFrom":[subQ1,sQuery(id+"F0.wireOp",EDGE,"E12.MirrorCS")]}),1.0]])],"derivedFrom":subQ1})])]}),makeQuery(id+"F1.opExtrude","SWEPT_FACE",FACE,{"disambiguationData":[OSD([subQ1]),TDD([makeQuery(id+"F0.imprint","IMPRINT",EDGE,{"disambiguationData":[TD([[makeQuery(id+"F0.imprint","INTERSECT",VERTEX,{"derivedFrom":[subQ1,sQuery(id+"F0.wireOp",EDGE,"E3")]}),1.0]])],"derivedFrom":subQ1})])]}),makeQuery(id+"F1.opExtrude","SWEPT_FACE",FACE,{"disambiguationData":[OSD([subQ1]),TDD([makeQuery(id+"F0.imprint","IMPRINT",EDGE,{"disambiguationData":[TD([[makeQuery(id+"F0.imprint","INTERSECT",VERTEX,{"derivedFrom":[subQ1,sQuery(id+"F0.wireOp",EDGE,"E8")]}),1.0]])],"derivedFrom":subQ1})])]}),makeQuery(id+"F1.opExtrude","SWEPT_FACE",FACE,{"disambiguationData":[OSD([subQ1]),TDD([makeQuery(id+"F0.imprint","IMPRINT",EDGE,{"disambiguationData":[TD([[makeQuery(id+"F0.imprint","INTERSECT",VERTEX,{"derivedFrom":[subQ1,sQuery(id+"F0.wireOp",EDGE,"E6")]}),1.0]])],"derivedFrom":subQ1})])]}),makeQuery(id+"F1.opExtrude","SWEPT_FACE",FACE,{"disambiguationData":[OSD([subQ1]),TDD([makeQuery(id+"F0.imprint","IMPRINT",EDGE,{"disambiguationData":[TD([[makeQuery(id+"F0.imprint","INTERSECT",VERTEX,{"derivedFrom":[subQ1,sQuery(id+"F0.wireOp",EDGE,"E5")]}),-1.0]])],"derivedFrom":subQ1})])]}),makeQuery(id+"F1.opExtrude","SWEPT_FACE",FACE,{"disambiguationData":[OSD([subQ1]),TDD([makeQuery(id+"F0.imprint","IMPRINT",EDGE,{"disambiguationData":[TD([[makeQuery(id+"F0.imprint","INTERSECT",VERTEX,{"derivedFrom":[subQ1,sQuery(id+"F0.wireOp",EDGE,"E26.MirrorCS")]}),1.0]])],"derivedFrom":subQ1})])]}),makeQuery(id+"F1.opExtrude","SWEPT_FACE",FACE,{"disambiguationData":[OSD([subQ1]),TDD([makeQuery(id+"F0.imprint","IMPRINT",EDGE,{"disambiguationData":[TD([[makeQuery(id+"F0.imprint","INTERSECT",VERTEX,{"derivedFrom":[subQ1,sQuery(id+"F0.wireOp",EDGE,"E24.MirrorCS")]}),1.0]])],"derivedFrom":subQ1})])]}),makeQuery(id+"F1.opExtrude","SWEPT_FACE",FACE,{"disambiguationData":[OSD([subQ1]),TDD([makeQuery(id+"F0.imprint","IMPRINT",EDGE,{"disambiguationData":[TD([[makeQuery(id+"F0.imprint","INTERSECT",VERTEX,{"derivedFrom":[subQ1,sQuery(id+"F0.wireOp",EDGE,"E22.MirrorCS")]}),1.0]])],"derivedFrom":subQ1})])]}),makeQuery(id+"F1.opExtrude","SWEPT_FACE",FACE,{"disambiguationData":[OSD([subQ1]),TDD([makeQuery(id+"F0.imprint","IMPRINT",EDGE,{"disambiguationData":[TD([[makeQuery(id+"F0.imprint","INTERSECT",VERTEX,{"derivedFrom":[subQ1,sQuery(id+"F0.wireOp",EDGE,"E20.MirrorCS")]}),1.0]])],"derivedFrom":subQ1})])]}),makeQuery(id+"F1.opExtrude","SWEPT_FACE",FACE,{"disambiguationData":[OSD([subQ1]),TDD([makeQuery(id+"F0.imprint","IMPRINT",EDGE,{"disambiguationData":[TD([[makeQuery(id+"F0.imprint","INTERSECT",VERTEX,{"derivedFrom":[subQ1,sQuery(id+"F0.wireOp",EDGE,"E18.MirrorCS")]}),1.0]])],"derivedFrom":subQ1})])]}),makeQuery(id+"F1.opExtrude","SWEPT_FACE",FACE,{"disambiguationData":[OSD([subQ1]),TDD([makeQuery(id+"F0.imprint","IMPRINT",EDGE,{"disambiguationData":[TD([[makeQuery(id+"F0.imprint","INTERSECT",VERTEX,{"derivedFrom":[subQ1,sQuery(id+"F0.wireOp",EDGE,"E17.MirrorCS")]}),-1.0]])],"derivedFrom":subQ1})])]})],"fromTools":[makeQuery(id+"F5.opSweep","SWEPT_FACE",FACE,{"disambiguationData":[OSD([subQ3,subQ1,subQ0]),TDD([subQ4,makeQuery(id+"F4.imprint","IMPRINT",EDGE,{"disambiguationData":[TD([[makeQuery(id+"F4.imprint","INTERSECT",VERTEX,{"derivedFrom":[subQ2,sQuery(id+"F4.wireOp",EDGE,"E30")]}),1.0]])],"derivedFrom":subQ2})])]}),makeQuery(id+"F5.opSweep","SWEPT_FACE",FACE,{"disambiguationData":[OSD([subQ3,subQ1,subQ0]),TDD([subQ4,makeQuery(id+"F4.imprint","IMPRINT",EDGE,{"disambiguationData":[TD([[makeQuery(id+"F4.imprint","INTERSECT",VERTEX,{"derivedFrom":[subQ2,sQuery(id+"F4.wireOp",EDGE,"E32.MirrorCS")]}),1.0]])],"derivedFrom":subQ2})])]}),makeQuery(id+"F5.opSweep","SWEPT_FACE",FACE,{"disambiguationData":[OSD([subQ3,subQ1,subQ0]),TDD([subQ4,makeQuery(id+"F4.imprint","IMPRINT",EDGE,{"disambiguationData":[TD([[makeQuery(id+"F4.imprint","INTERSECT",VERTEX,{"derivedFrom":[subQ2,sQuery(id+"F4.wireOp",EDGE,"E34.MirrorCS")]}),1.0]])],"derivedFrom":subQ2})])]}),makeQuery(id+"F5.opSweep","SWEPT_FACE",FACE,{"disambiguationData":[OSD([subQ3,subQ1,subQ0]),TDD([subQ4,makeQuery(id+"F4.imprint","IMPRINT",EDGE,{"disambiguationData":[TD([[makeQuery(id+"F4.imprint","INTERSECT",VERTEX,{"derivedFrom":[subQ2,sQuery(id+"F4.wireOp",EDGE,"E36.MirrorCS")]}),1.0]])],"derivedFrom":subQ2})])]}),makeQuery(id+"F5.opSweep","SWEPT_FACE",FACE,{"disambiguationData":[OSD([subQ3,subQ1,subQ0]),TDD([subQ4,makeQuery(id+"F4.imprint","IMPRINT",EDGE,{"disambiguationData":[TD([[makeQuery(id+"F4.imprint","INTERSECT",VERTEX,{"derivedFrom":[subQ2,sQuery(id+"F4.wireOp",EDGE,"E38.MirrorCS")]}),1.0]])],"derivedFrom":subQ2})])]}),makeQuery(id+"F5.opSweep","SWEPT_FACE",FACE,{"disambiguationData":[OSD([subQ3,subQ1,subQ0]),TDD([subQ4,makeQuery(id+"F4.imprint","IMPRINT",EDGE,{"disambiguationData":[TD([[makeQuery(id+"F4.imprint","INTERSECT",VERTEX,{"derivedFrom":[subQ2,sQuery(id+"F4.wireOp",EDGE,"E40.MirrorCS")]}),1.0]])],"derivedFrom":subQ2})])]}),makeQuery(id+"F5.opSweep","SWEPT_FACE",FACE,{"disambiguationData":[OSD([subQ3,subQ1,subQ0]),TDD([subQ4,makeQuery(id+"F4.imprint","IMPRINT",EDGE,{"disambiguationData":[TD([[makeQuery(id+"F4.imprint","INTERSECT",VERTEX,{"derivedFrom":[subQ2,sQuery(id+"F4.wireOp",EDGE,"E42.MirrorCS")]}),1.0]])],"derivedFrom":subQ2})])]})]})]});}
            var Q26;
            {var subQ0=sQuery(id+"F0.wireOp",EDGE,"E17.MirrorCS");var subQ1=sQuery(id+"F2.wireOp",EDGE,"E29");var subQ3=sQuery(id+"F0.wireOp",EDGE,"E2");Q26=makeQuery(id+"F8.opFillet","BLEND_EDGE",EDGE,{"blendedFrom":[makeQuery(id+"F3.opExtrude","CAP_EDGE",EDGE,{"disambiguationData":[OSD([subQ1])],"isStart":true}),makeQuery(id+"F5.boolean.opBoolean","SPLIT",FACE,{"disambiguationData":[TD([makeQuery(id+"F3.opExtrude","CAP_FACE",FACE,{"disambiguationData":[OSD([subQ1])],"isStart":true})])],"derivedFrom":makeQuery(id+"F1.opExtrude","SWEPT_FACE",FACE,{"disambiguationData":[OSD([subQ3]),TDD([makeQuery(id+"F0.imprint","IMPRINT",EDGE,{"disambiguationData":[TD([[makeQuery(id+"F0.imprint","INTERSECT",VERTEX,{"derivedFrom":[subQ3,subQ0]}),1.0]])],"derivedFrom":subQ3})])]})})],"blendedInto":[makeQuery(id+"F5.boolean.opBoolean","SPLIT",FACE,{"disambiguationData":[TD([makeQuery(id+"F3.opExtrude","CAP_FACE",FACE,{"disambiguationData":[OSD([subQ1])],"isStart":true})])],"derivedFrom":makeQuery(id+"F1.opExtrude","SWEPT_FACE",FACE,{"disambiguationData":[OSD([subQ3]),TDD([makeQuery(id+"F0.imprint","IMPRINT",EDGE,{"disambiguationData":[TD([[makeQuery(id+"F0.imprint","INTERSECT",VERTEX,{"derivedFrom":[subQ3,subQ0]}),1.0]])],"derivedFrom":subQ3})])]})})]});}
            var Q27;
            {var subQ0=sQuery(id+"F0.wireOp",EDGE,"E27.MirrorCS");var subQ1=sQuery(id+"F0.wireOp",EDGE,"E1");var subQ2=makeQuery(id+"F1.opExtrude","SWEPT_EDGE",EDGE,{"disambiguationData":[OSD([subQ1,subQ0])]});var subQ3=sQuery(id+"F0.wireOp",EDGE,"E0");var subQ4=makeQuery(id+"F1.opExtrude","CAP_EDGE",EDGE,{"disambiguationData":[OSD([subQ3])],"isStart":true});Q27=makeQuery(id+"F8.opFillet","BLEND_EDGE",EDGE,{"disambiguationData":[OD(6.0)],"blendedFrom":[makeQuery(id+"F3.opExtrude","CAP_EDGE",EDGE,{"disambiguationData":[OSD([sQuery(id+"F2.wireOp",EDGE,"E29")])],"isStart":true}),makeQuery(id+"F5.boolean.opBoolean","MERGE",FACE,{"derivedFrom":[makeQuery(id+"F1.opExtrude","SWEPT_FACE",FACE,{"disambiguationData":[OSD([subQ1]),TDD([makeQuery(id+"F0.imprint","IMPRINT",EDGE,{"disambiguationData":[TD([[makeQuery(id+"F0.imprint","INTERSECT",VERTEX,{"derivedFrom":[subQ1,sQuery(id+"F0.wireOp",EDGE,"E14.MirrorCS")]}),1.0]])],"derivedFrom":subQ1})])]}),makeQuery(id+"F1.opExtrude","SWEPT_FACE",FACE,{"disambiguationData":[OSD([subQ1]),TDD([makeQuery(id+"F0.imprint","IMPRINT",EDGE,{"disambiguationData":[TD([[makeQuery(id+"F0.imprint","INTERSECT",VERTEX,{"derivedFrom":[subQ1,sQuery(id+"F0.wireOp",EDGE,"E12.MirrorCS")]}),1.0]])],"derivedFrom":subQ1})])]}),makeQuery(id+"F1.opExtrude","SWEPT_FACE",FACE,{"disambiguationData":[OSD([subQ1]),TDD([makeQuery(id+"F0.imprint","IMPRINT",EDGE,{"disambiguationData":[TD([[makeQuery(id+"F0.imprint","INTERSECT",VERTEX,{"derivedFrom":[subQ1,sQuery(id+"F0.wireOp",EDGE,"E3")]}),1.0]])],"derivedFrom":subQ1})])]}),makeQuery(id+"F1.opExtrude","SWEPT_FACE",FACE,{"disambiguationData":[OSD([subQ1]),TDD([makeQuery(id+"F0.imprint","IMPRINT",EDGE,{"disambiguationData":[TD([[makeQuery(id+"F0.imprint","INTERSECT",VERTEX,{"derivedFrom":[subQ1,sQuery(id+"F0.wireOp",EDGE,"E8")]}),1.0]])],"derivedFrom":subQ1})])]}),makeQuery(id+"F1.opExtrude","SWEPT_FACE",FACE,{"disambiguationData":[OSD([subQ1]),TDD([makeQuery(id+"F0.imprint","IMPRINT",EDGE,{"disambiguationData":[TD([[makeQuery(id+"F0.imprint","INTERSECT",VERTEX,{"derivedFrom":[subQ1,sQuery(id+"F0.wireOp",EDGE,"E6")]}),1.0]])],"derivedFrom":subQ1})])]}),makeQuery(id+"F1.opExtrude","SWEPT_FACE",FACE,{"disambiguationData":[OSD([subQ1]),TDD([makeQuery(id+"F0.imprint","IMPRINT",EDGE,{"disambiguationData":[TD([[makeQuery(id+"F0.imprint","INTERSECT",VERTEX,{"derivedFrom":[subQ1,sQuery(id+"F0.wireOp",EDGE,"E5")]}),-1.0]])],"derivedFrom":subQ1})])]}),makeQuery(id+"F1.opExtrude","SWEPT_FACE",FACE,{"disambiguationData":[OSD([subQ1]),TDD([makeQuery(id+"F0.imprint","IMPRINT",EDGE,{"disambiguationData":[TD([[makeQuery(id+"F0.imprint","INTERSECT",VERTEX,{"derivedFrom":[subQ1,sQuery(id+"F0.wireOp",EDGE,"E26.MirrorCS")]}),1.0]])],"derivedFrom":subQ1})])]}),makeQuery(id+"F1.opExtrude","SWEPT_FACE",FACE,{"disambiguationData":[OSD([subQ1]),TDD([makeQuery(id+"F0.imprint","IMPRINT",EDGE,{"disambiguationData":[TD([[makeQuery(id+"F0.imprint","INTERSECT",VERTEX,{"derivedFrom":[subQ1,sQuery(id+"F0.wireOp",EDGE,"E24.MirrorCS")]}),1.0]])],"derivedFrom":subQ1})])]}),makeQuery(id+"F1.opExtrude","SWEPT_FACE",FACE,{"disambiguationData":[OSD([subQ1]),TDD([makeQuery(id+"F0.imprint","IMPRINT",EDGE,{"disambiguationData":[TD([[makeQuery(id+"F0.imprint","INTERSECT",VERTEX,{"derivedFrom":[subQ1,sQuery(id+"F0.wireOp",EDGE,"E22.MirrorCS")]}),1.0]])],"derivedFrom":subQ1})])]}),makeQuery(id+"F1.opExtrude","SWEPT_FACE",FACE,{"disambiguationData":[OSD([subQ1]),TDD([makeQuery(id+"F0.imprint","IMPRINT",EDGE,{"disambiguationData":[TD([[makeQuery(id+"F0.imprint","INTERSECT",VERTEX,{"derivedFrom":[subQ1,sQuery(id+"F0.wireOp",EDGE,"E20.MirrorCS")]}),1.0]])],"derivedFrom":subQ1})])]}),makeQuery(id+"F1.opExtrude","SWEPT_FACE",FACE,{"disambiguationData":[OSD([subQ1]),TDD([makeQuery(id+"F0.imprint","IMPRINT",EDGE,{"disambiguationData":[TD([[makeQuery(id+"F0.imprint","INTERSECT",VERTEX,{"derivedFrom":[subQ1,sQuery(id+"F0.wireOp",EDGE,"E18.MirrorCS")]}),1.0]])],"derivedFrom":subQ1})])]}),makeQuery(id+"F1.opExtrude","SWEPT_FACE",FACE,{"disambiguationData":[OSD([subQ1]),TDD([makeQuery(id+"F0.imprint","IMPRINT",EDGE,{"disambiguationData":[TD([[makeQuery(id+"F0.imprint","INTERSECT",VERTEX,{"derivedFrom":[subQ1,sQuery(id+"F0.wireOp",EDGE,"E17.MirrorCS")]}),-1.0]])],"derivedFrom":subQ1})])]})],"fromTools":[makeQuery(id+"F5.opSweep","SWEPT_FACE",FACE,{"disambiguationData":[OSD([subQ3,subQ1,subQ0]),TDD([subQ4,makeQuery(id+"F4.imprint","IMPRINT",EDGE,{"disambiguationData":[TD([[makeQuery(id+"F4.imprint","INTERSECT",VERTEX,{"derivedFrom":[subQ2,sQuery(id+"F4.wireOp",EDGE,"E30")]}),1.0]])],"derivedFrom":subQ2})])]}),makeQuery(id+"F5.opSweep","SWEPT_FACE",FACE,{"disambiguationData":[OSD([subQ3,subQ1,subQ0]),TDD([subQ4,makeQuery(id+"F4.imprint","IMPRINT",EDGE,{"disambiguationData":[TD([[makeQuery(id+"F4.imprint","INTERSECT",VERTEX,{"derivedFrom":[subQ2,sQuery(id+"F4.wireOp",EDGE,"E32.MirrorCS")]}),1.0]])],"derivedFrom":subQ2})])]}),makeQuery(id+"F5.opSweep","SWEPT_FACE",FACE,{"disambiguationData":[OSD([subQ3,subQ1,subQ0]),TDD([subQ4,makeQuery(id+"F4.imprint","IMPRINT",EDGE,{"disambiguationData":[TD([[makeQuery(id+"F4.imprint","INTERSECT",VERTEX,{"derivedFrom":[subQ2,sQuery(id+"F4.wireOp",EDGE,"E34.MirrorCS")]}),1.0]])],"derivedFrom":subQ2})])]}),makeQuery(id+"F5.opSweep","SWEPT_FACE",FACE,{"disambiguationData":[OSD([subQ3,subQ1,subQ0]),TDD([subQ4,makeQuery(id+"F4.imprint","IMPRINT",EDGE,{"disambiguationData":[TD([[makeQuery(id+"F4.imprint","INTERSECT",VERTEX,{"derivedFrom":[subQ2,sQuery(id+"F4.wireOp",EDGE,"E36.MirrorCS")]}),1.0]])],"derivedFrom":subQ2})])]}),makeQuery(id+"F5.opSweep","SWEPT_FACE",FACE,{"disambiguationData":[OSD([subQ3,subQ1,subQ0]),TDD([subQ4,makeQuery(id+"F4.imprint","IMPRINT",EDGE,{"disambiguationData":[TD([[makeQuery(id+"F4.imprint","INTERSECT",VERTEX,{"derivedFrom":[subQ2,sQuery(id+"F4.wireOp",EDGE,"E38.MirrorCS")]}),1.0]])],"derivedFrom":subQ2})])]}),makeQuery(id+"F5.opSweep","SWEPT_FACE",FACE,{"disambiguationData":[OSD([subQ3,subQ1,subQ0]),TDD([subQ4,makeQuery(id+"F4.imprint","IMPRINT",EDGE,{"disambiguationData":[TD([[makeQuery(id+"F4.imprint","INTERSECT",VERTEX,{"derivedFrom":[subQ2,sQuery(id+"F4.wireOp",EDGE,"E40.MirrorCS")]}),1.0]])],"derivedFrom":subQ2})])]}),makeQuery(id+"F5.opSweep","SWEPT_FACE",FACE,{"disambiguationData":[OSD([subQ3,subQ1,subQ0]),TDD([subQ4,makeQuery(id+"F4.imprint","IMPRINT",EDGE,{"disambiguationData":[TD([[makeQuery(id+"F4.imprint","INTERSECT",VERTEX,{"derivedFrom":[subQ2,sQuery(id+"F4.wireOp",EDGE,"E42.MirrorCS")]}),1.0]])],"derivedFrom":subQ2})])]})]})],"blendedInto":[makeQuery(id+"F5.boolean.opBoolean","MERGE",FACE,{"derivedFrom":[makeQuery(id+"F1.opExtrude","SWEPT_FACE",FACE,{"disambiguationData":[OSD([subQ1]),TDD([makeQuery(id+"F0.imprint","IMPRINT",EDGE,{"disambiguationData":[TD([[makeQuery(id+"F0.imprint","INTERSECT",VERTEX,{"derivedFrom":[subQ1,sQuery(id+"F0.wireOp",EDGE,"E14.MirrorCS")]}),1.0]])],"derivedFrom":subQ1})])]}),makeQuery(id+"F1.opExtrude","SWEPT_FACE",FACE,{"disambiguationData":[OSD([subQ1]),TDD([makeQuery(id+"F0.imprint","IMPRINT",EDGE,{"disambiguationData":[TD([[makeQuery(id+"F0.imprint","INTERSECT",VERTEX,{"derivedFrom":[subQ1,sQuery(id+"F0.wireOp",EDGE,"E12.MirrorCS")]}),1.0]])],"derivedFrom":subQ1})])]}),makeQuery(id+"F1.opExtrude","SWEPT_FACE",FACE,{"disambiguationData":[OSD([subQ1]),TDD([makeQuery(id+"F0.imprint","IMPRINT",EDGE,{"disambiguationData":[TD([[makeQuery(id+"F0.imprint","INTERSECT",VERTEX,{"derivedFrom":[subQ1,sQuery(id+"F0.wireOp",EDGE,"E3")]}),1.0]])],"derivedFrom":subQ1})])]}),makeQuery(id+"F1.opExtrude","SWEPT_FACE",FACE,{"disambiguationData":[OSD([subQ1]),TDD([makeQuery(id+"F0.imprint","IMPRINT",EDGE,{"disambiguationData":[TD([[makeQuery(id+"F0.imprint","INTERSECT",VERTEX,{"derivedFrom":[subQ1,sQuery(id+"F0.wireOp",EDGE,"E8")]}),1.0]])],"derivedFrom":subQ1})])]}),makeQuery(id+"F1.opExtrude","SWEPT_FACE",FACE,{"disambiguationData":[OSD([subQ1]),TDD([makeQuery(id+"F0.imprint","IMPRINT",EDGE,{"disambiguationData":[TD([[makeQuery(id+"F0.imprint","INTERSECT",VERTEX,{"derivedFrom":[subQ1,sQuery(id+"F0.wireOp",EDGE,"E6")]}),1.0]])],"derivedFrom":subQ1})])]}),makeQuery(id+"F1.opExtrude","SWEPT_FACE",FACE,{"disambiguationData":[OSD([subQ1]),TDD([makeQuery(id+"F0.imprint","IMPRINT",EDGE,{"disambiguationData":[TD([[makeQuery(id+"F0.imprint","INTERSECT",VERTEX,{"derivedFrom":[subQ1,sQuery(id+"F0.wireOp",EDGE,"E5")]}),-1.0]])],"derivedFrom":subQ1})])]}),makeQuery(id+"F1.opExtrude","SWEPT_FACE",FACE,{"disambiguationData":[OSD([subQ1]),TDD([makeQuery(id+"F0.imprint","IMPRINT",EDGE,{"disambiguationData":[TD([[makeQuery(id+"F0.imprint","INTERSECT",VERTEX,{"derivedFrom":[subQ1,sQuery(id+"F0.wireOp",EDGE,"E26.MirrorCS")]}),1.0]])],"derivedFrom":subQ1})])]}),makeQuery(id+"F1.opExtrude","SWEPT_FACE",FACE,{"disambiguationData":[OSD([subQ1]),TDD([makeQuery(id+"F0.imprint","IMPRINT",EDGE,{"disambiguationData":[TD([[makeQuery(id+"F0.imprint","INTERSECT",VERTEX,{"derivedFrom":[subQ1,sQuery(id+"F0.wireOp",EDGE,"E24.MirrorCS")]}),1.0]])],"derivedFrom":subQ1})])]}),makeQuery(id+"F1.opExtrude","SWEPT_FACE",FACE,{"disambiguationData":[OSD([subQ1]),TDD([makeQuery(id+"F0.imprint","IMPRINT",EDGE,{"disambiguationData":[TD([[makeQuery(id+"F0.imprint","INTERSECT",VERTEX,{"derivedFrom":[subQ1,sQuery(id+"F0.wireOp",EDGE,"E22.MirrorCS")]}),1.0]])],"derivedFrom":subQ1})])]}),makeQuery(id+"F1.opExtrude","SWEPT_FACE",FACE,{"disambiguationData":[OSD([subQ1]),TDD([makeQuery(id+"F0.imprint","IMPRINT",EDGE,{"disambiguationData":[TD([[makeQuery(id+"F0.imprint","INTERSECT",VERTEX,{"derivedFrom":[subQ1,sQuery(id+"F0.wireOp",EDGE,"E20.MirrorCS")]}),1.0]])],"derivedFrom":subQ1})])]}),makeQuery(id+"F1.opExtrude","SWEPT_FACE",FACE,{"disambiguationData":[OSD([subQ1]),TDD([makeQuery(id+"F0.imprint","IMPRINT",EDGE,{"disambiguationData":[TD([[makeQuery(id+"F0.imprint","INTERSECT",VERTEX,{"derivedFrom":[subQ1,sQuery(id+"F0.wireOp",EDGE,"E18.MirrorCS")]}),1.0]])],"derivedFrom":subQ1})])]}),makeQuery(id+"F1.opExtrude","SWEPT_FACE",FACE,{"disambiguationData":[OSD([subQ1]),TDD([makeQuery(id+"F0.imprint","IMPRINT",EDGE,{"disambiguationData":[TD([[makeQuery(id+"F0.imprint","INTERSECT",VERTEX,{"derivedFrom":[subQ1,sQuery(id+"F0.wireOp",EDGE,"E17.MirrorCS")]}),-1.0]])],"derivedFrom":subQ1})])]})],"fromTools":[makeQuery(id+"F5.opSweep","SWEPT_FACE",FACE,{"disambiguationData":[OSD([subQ3,subQ1,subQ0]),TDD([subQ4,makeQuery(id+"F4.imprint","IMPRINT",EDGE,{"disambiguationData":[TD([[makeQuery(id+"F4.imprint","INTERSECT",VERTEX,{"derivedFrom":[subQ2,sQuery(id+"F4.wireOp",EDGE,"E30")]}),1.0]])],"derivedFrom":subQ2})])]}),makeQuery(id+"F5.opSweep","SWEPT_FACE",FACE,{"disambiguationData":[OSD([subQ3,subQ1,subQ0]),TDD([subQ4,makeQuery(id+"F4.imprint","IMPRINT",EDGE,{"disambiguationData":[TD([[makeQuery(id+"F4.imprint","INTERSECT",VERTEX,{"derivedFrom":[subQ2,sQuery(id+"F4.wireOp",EDGE,"E32.MirrorCS")]}),1.0]])],"derivedFrom":subQ2})])]}),makeQuery(id+"F5.opSweep","SWEPT_FACE",FACE,{"disambiguationData":[OSD([subQ3,subQ1,subQ0]),TDD([subQ4,makeQuery(id+"F4.imprint","IMPRINT",EDGE,{"disambiguationData":[TD([[makeQuery(id+"F4.imprint","INTERSECT",VERTEX,{"derivedFrom":[subQ2,sQuery(id+"F4.wireOp",EDGE,"E34.MirrorCS")]}),1.0]])],"derivedFrom":subQ2})])]}),makeQuery(id+"F5.opSweep","SWEPT_FACE",FACE,{"disambiguationData":[OSD([subQ3,subQ1,subQ0]),TDD([subQ4,makeQuery(id+"F4.imprint","IMPRINT",EDGE,{"disambiguationData":[TD([[makeQuery(id+"F4.imprint","INTERSECT",VERTEX,{"derivedFrom":[subQ2,sQuery(id+"F4.wireOp",EDGE,"E36.MirrorCS")]}),1.0]])],"derivedFrom":subQ2})])]}),makeQuery(id+"F5.opSweep","SWEPT_FACE",FACE,{"disambiguationData":[OSD([subQ3,subQ1,subQ0]),TDD([subQ4,makeQuery(id+"F4.imprint","IMPRINT",EDGE,{"disambiguationData":[TD([[makeQuery(id+"F4.imprint","INTERSECT",VERTEX,{"derivedFrom":[subQ2,sQuery(id+"F4.wireOp",EDGE,"E38.MirrorCS")]}),1.0]])],"derivedFrom":subQ2})])]}),makeQuery(id+"F5.opSweep","SWEPT_FACE",FACE,{"disambiguationData":[OSD([subQ3,subQ1,subQ0]),TDD([subQ4,makeQuery(id+"F4.imprint","IMPRINT",EDGE,{"disambiguationData":[TD([[makeQuery(id+"F4.imprint","INTERSECT",VERTEX,{"derivedFrom":[subQ2,sQuery(id+"F4.wireOp",EDGE,"E40.MirrorCS")]}),1.0]])],"derivedFrom":subQ2})])]}),makeQuery(id+"F5.opSweep","SWEPT_FACE",FACE,{"disambiguationData":[OSD([subQ3,subQ1,subQ0]),TDD([subQ4,makeQuery(id+"F4.imprint","IMPRINT",EDGE,{"disambiguationData":[TD([[makeQuery(id+"F4.imprint","INTERSECT",VERTEX,{"derivedFrom":[subQ2,sQuery(id+"F4.wireOp",EDGE,"E42.MirrorCS")]}),1.0]])],"derivedFrom":subQ2})])]})]})]});}
            fillet(context, id + "F9", {"entities" : qUnion([Q0, Q1, Q2, Q3, Q4, Q5, Q6, Q7, Q8, Q9, Q10, Q11, Q12, Q13, Q14, Q15, Q16, Q17, Q18, Q19, Q20, Q21, Q22, Q23, Q24, Q25, Q26, Q27]), "radius" : 6 * mm, "tangentPropagation" : true, "allowEdgeOverflow" : false});
        }
    });
